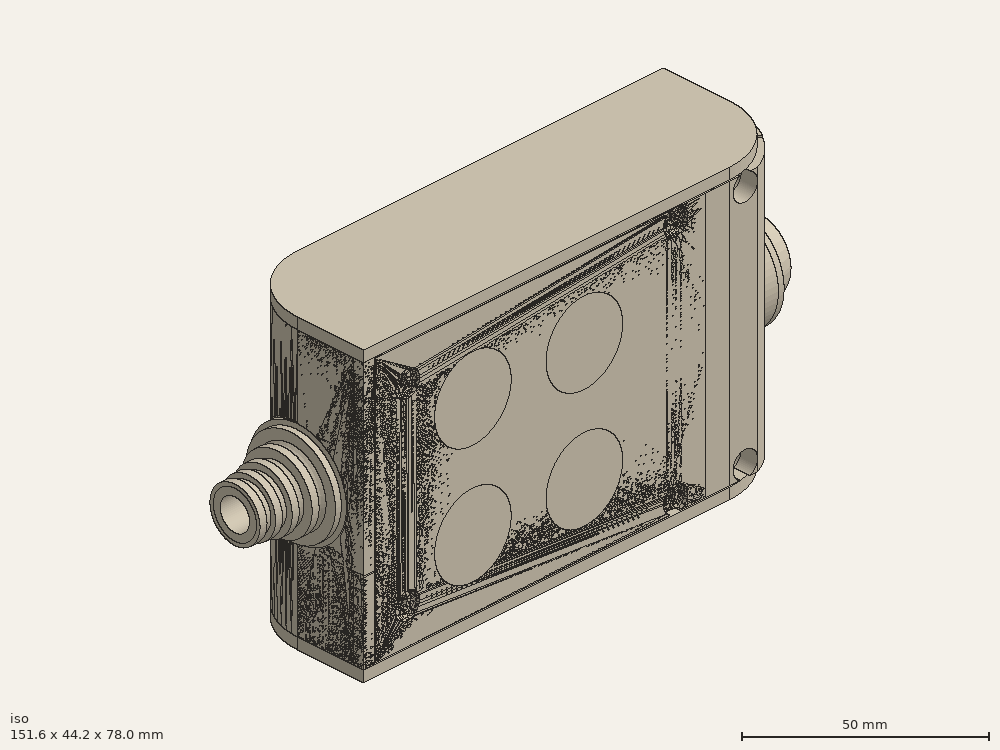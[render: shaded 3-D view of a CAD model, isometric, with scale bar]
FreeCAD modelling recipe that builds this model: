
FCSTD DOCUMENT  (FreeCAD 0.19R0.19.2)
Label: enclosure_159
License: All rights reserved
LicenseURL: http://en.wikipedia.org/wiki/All_rights_reserved
objects: Part::Feature×138, Part::Revolution×138, Part::MultiFuse×111, Sketcher::SketchObject×66, Part::Extrusion×51, Part::Cut×48, Part::Cylinder×44, Part::Fillet×43, Part::Box×28, App::MeasureDistance×4
note: 667 computed .brp shape members not serialized (recipe doc carries the construction recipe); baked Part::Feature solids carry a one-line shape summary decoded from their .brp

FEATURE [Sketcher::SketchObject] Sketch  label="topSketch"
  FullyConstrained = true
  sketch-geometry (20):
    g0: LineSegment StartX=5.21097e-06 StartY=3 StartZ=0 EndX=5.21097e-06 EndY=19 EndZ=0
    g1: ArcOfCircle CenterX=19 CenterY=19 CenterZ=0 NormalX=0 NormalY=0 NormalZ=1 AngleXU=0 Radius=19 StartAngle=1.5708 EndAngle=3.14159
    g2: ArcOfCircle CenterX=19 CenterY=19 CenterZ=0 NormalX=0 NormalY=0 NormalZ=1 AngleXU=0 Radius=16 StartAngle=1.5708 EndAngle=3.14159
    g3: LineSegment StartX=114 StartY=35 StartZ=0 EndX=19 EndY=35 EndZ=0
    g4: LineSegment StartX=5.21097e-06 StartY=3 StartZ=0 EndX=5.21097e-06 EndY=0 EndZ=0
    g5: LineSegment StartX=3 StartY=0 StartZ=0 EndX=5.21097e-06 EndY=0 EndZ=0
    g6: LineSegment StartX=3 StartY=19 StartZ=0 EndX=3 EndY=0 EndZ=0
    g7: LineSegment StartX=19 StartY=38 StartZ=0 EndX=124 EndY=38 EndZ=0
    g8: Circle CenterX=119 CenterY=35 CenterZ=0 NormalX=0 NormalY=0 NormalZ=1 AngleXU=0 Radius=1
    g9: Circle CenterX=121 CenterY=35 CenterZ=0 NormalX=0 NormalY=0 NormalZ=1 AngleXU=0 Radius=1
    g10: Circle CenterX=121 CenterY=33 CenterZ=0 NormalX=0 NormalY=0 NormalZ=1 AngleXU=0 Radius=1
    g11: BSplineCurve PolesCount=3 KnotsCount=2 Degree=2 IsPeriodic=0
    g12: GeomPoint X=119 Y=35 Z=0
    g13: GeomPoint X=121 Y=33 Z=0
    g14: LineSegment StartX=119 StartY=35 StartZ=0 EndX=114 EndY=35 EndZ=0
    g15: ArcOfCircle CenterX=105 CenterY=19 CenterZ=0 NormalX=0 NormalY=0 NormalZ=1 AngleXU=0 Radius=19 StartAngle=5.7297 EndAngle=6.28319
    g16: ArcOfCircle CenterX=105 CenterY=19 CenterZ=0 NormalX=0 NormalY=0 NormalZ=1 AngleXU=0 Radius=16 StartAngle=5.60905 EndAngle=6.28319
    g17: LineSegment StartX=121 StartY=33 StartZ=0 EndX=121 EndY=19 EndZ=0
    g18: LineSegment StartX=124 StartY=38 StartZ=0 EndX=124 EndY=19 EndZ=0
    g19: LineSegment StartX=117.5 StartY=9.01251 StartZ=0 EndX=121.163 EndY=9.0125 EndZ=0
  constraints (46):
    c: Vertical(g0)
    c: Block(g0)
    c: Coincident(g1,g0)
    c: Block(g1)
    c: Coincident(g2,g1)
    c: Block(g2)
    c: Coincident(g3,g2)
    c: Horizontal(g3)
    c: Tangent(g3,g2)
    c: Coincident(g4,g0)
    c: Distance(g4) = 3
    c: Vertical(g4)
    c: Coincident(g5,g4)
    c: Horizontal(g5)
    c: Coincident(g6,g2)
    c: Coincident(g6,g5)
    c: Vertical(g6)
    c: Horizontal(g7)
    c: Distance(g7) = 105
    c: Coincident(g7,g1)
    c: Block(g3)
    c: Weight(g8) = 1
    c: Equal(g8,g9)
    c: Equal(g8,g10)
    c: InternalAlignment(g8,g11)
    c: InternalAlignment(g9,g11)
    c: InternalAlignment(g10,g11)
    c: InternalAlignment(g12,g11)
    c: InternalAlignment(g13,g11)
    c: Block(g11)
    c: Coincident(g14,g11)
    c: Coincident(g14,g3)
    c: Horizontal(g14)
    c: Block(g15)
    c: Coincident(g16,g15)
    c: Block(g16)
    c: Coincident(g17,g11)
    c: Coincident(g17,g16)
    c: Vertical(g17)
    c: Distance(g17) = 14
    c: Coincident(g18,g7)
    c: Coincident(g18,g15)
    c: Vertical(g18)
    c: Distance(g18) = 19
    c: Coincident(g19,g16)
    c: Coincident(g19,g15)
FEATURE [Sketcher::SketchObject] Sketch001  label="bottomSketch"
  FullyConstrained = true
  sketch-geometry (32):
    g0: LineSegment StartX=3.3 StartY=-6.03275e-07 StartZ=0 EndX=98 EndY=-6.03275e-07 EndZ=0
    g1: ArcOfCircle CenterX=98 CenterY=19 CenterZ=0 NormalX=0 NormalY=0 NormalZ=1 AngleXU=0 Radius=19 StartAngle=4.71239 EndAngle=5.71103
    g2: LineSegment StartX=6.3 StartY=8 StartZ=0 EndX=3.3 EndY=8 EndZ=0
    g3: LineSegment StartX=3.3 StartY=8 StartZ=0 EndX=3.3 EndY=-6.03275e-07 EndZ=0
    g4: ArcOfCircle CenterX=8.3 CenterY=5 CenterZ=0 NormalX=0 NormalY=0 NormalZ=1 AngleXU=0 Radius=2 StartAngle=3.14159 EndAngle=4.71239
    g5: LineSegment StartX=6.3 StartY=8 StartZ=0 EndX=6.3 EndY=5 EndZ=0
    g6: ArcOfCircle CenterX=98 CenterY=19 CenterZ=0 NormalX=0 NormalY=0 NormalZ=1 AngleXU=0 Radius=12.7 StartAngle=4.71239 EndAngle=6.28319
    g7: LineSegment StartX=94.7 StartY=3 StartZ=0 EndX=8.3 EndY=3 EndZ=0
    g8-g12: Circle x5 (B-spline internal-alignment scaffolding for g13; pole/knot coordinates omitted)
    g13: BSplineCurve PolesCount=5 KnotsCount=3 Degree=3 IsPeriodic=0
    g14: GeomPoint X=98 Y=6.3 Z=0
    g15: GeomPoint X=96.3938 Y=4.71946 Z=0
    g16: GeomPoint X=94.7 Y=3 Z=0
    g17-g23: Circle x7 (B-spline internal-alignment scaffolding for g24; pole/knot coordinates omitted)
    g24: BSplineCurve PolesCount=7 KnotsCount=5 Degree=3 IsPeriodic=0
    g25-g29: GeomPoint x5 (B-spline internal-alignment scaffolding for g24; pole/knot coordinates omitted)
    g30: ArcOfCircle CenterX=98 CenterY=19 CenterZ=0 NormalX=0 NormalY=0 NormalZ=1 AngleXU=0 Radius=15.7 StartAngle=5.81226 EndAngle=6.28319
    g31: LineSegment StartX=110.7 StartY=19 StartZ=0 EndX=113.7 EndY=19 EndZ=0
  constraints (41):
    c: Horizontal(g0)
    c: Coincident(g1,g0)
    c: Block(g1)
    c: Horizontal(g2)
    c: Distance(g2) = 3
    c: Coincident(g3,g2)
    c: Vertical(g3)
    c: Coincident(g3,g0)
    c: Block(g4)
    c: Block(g2)
    c: Coincident(g5,g2)
    c: Coincident(g5,g4)
    c: Vertical(g5)
    c: Coincident(g6,g1)
    c: Block(g6)
    c: Coincident(g7,g4)
    c: Horizontal(g7)
    c: Block(g0)
    c: Block(g7)
    c: Block(g3)
    c: Coincident(g13,g6)
    c: Weight(g8) = 1
    c: Equal(g8, g9-g12) x4
    c: Coincident(g13,g7)
    c: InternalAlignment(g8-g12 -> g13) x5
    c: InternalAlignment(g14,g13)
    c: InternalAlignment(g15,g13)
    c: InternalAlignment(g16,g13)
    c: Block(g13)
    c: Weight(g17) = 1
    c: Equal(g17, g18-g23) x6
    c: Coincident(g24,g1)
    c: InternalAlignment(g17-g23 -> g24) x7
    c: InternalAlignment(g25-g29 -> g24) x5
    c: Block(g24)
    c: Coincident(g30,g24)
    c: Coincident(g31,g6)
    c: Coincident(g31,g30)
    c: Horizontal(g31)
    c: Block(g31)
    c: Block(g30)
FEATURE [Part::Extrusion] Extrude  label="top"
  Base = -> Sketch
  Dir = (0,0,1)
  DirMode = 2
  FaceMakerClass = Part::FaceMakerBullseye
  LengthFwd = 72
  LengthRev = 0
  Solid = true
  Symmetric = false
FEATURE [Part::Extrusion] Extrude001  label="bottom"
  Base = -> Sketch001
  Dir = (0,0,1)
  DirMode = 2
  FaceMakerClass = Part::FaceMakerBullseye
  LengthFwd = 71.4
  LengthRev = 0
  Placement = pos=(0,0,0.3) rot=(0,0,1;0rad)
  Solid = true
  Symmetric = false
FEATURE [Sketcher::SketchObject] Sketch002  label="topSketch001"
  FullyConstrained = true
  sketch-geometry (6):
    g0: ArcOfCircle CenterX=19 CenterY=19 CenterZ=0 NormalX=0 NormalY=0 NormalZ=1 AngleXU=0 Radius=19 StartAngle=1.5708 EndAngle=3.14159
    g1: LineSegment StartX=5.22862e-06 StartY=19 StartZ=0 EndX=5.22862e-06 EndY=1.19904e-11 EndZ=0
    g2: LineSegment StartX=19 StartY=38 StartZ=0 EndX=124 EndY=38 EndZ=0
    g3: LineSegment StartX=5.22862e-06 StartY=1.19904e-11 StartZ=0 EndX=105 EndY=1.19904e-11 EndZ=0
    g4: ArcOfCircle CenterX=105 CenterY=19 CenterZ=0 NormalX=0 NormalY=0 NormalZ=1 AngleXU=0 Radius=19 StartAngle=4.71239 EndAngle=6.28319
    g5: LineSegment StartX=124 StartY=38 StartZ=0 EndX=124 EndY=19 EndZ=0
  constraints (16):
    c: Block(g0)
    c: Coincident(g1,g0)
    c: Vertical(g1)
    c: Horizontal(g2)
    c: Distance(g2) = 105
    c: Coincident(g2,g0)
    c: Distance(g1) = 19
    c: Coincident(g3,g1)
    c: Horizontal(g3)
    c: Distance(g3) = 105
    c: Block(g4)
    c: Coincident(g4,g3)
    c: Coincident(g5,g2)
    c: Coincident(g5,g4)
    c: Vertical(g5)
    c: Distance(g5) = 19
FEATURE [Part::Extrusion] Extrude002  label="sideA"
  Base = -> Sketch002
  Dir = (0,0,1)
  DirMode = 2
  FaceMakerClass = Part::FaceMakerBullseye
  LengthFwd = 3
  LengthRev = 0
  Placement = pos=(0,0,-3) rot=(0,0,1;0rad)
  Solid = true
  Symmetric = false
FEATURE [Sketcher::SketchObject] Sketch003  label="topSketch002"
  FullyConstrained = true
  sketch-geometry (6):
    g0: LineSegment StartX=19 StartY=38 StartZ=0 EndX=117 EndY=38 EndZ=0
    g1: ArcOfCircle CenterX=19 CenterY=19 CenterZ=0 NormalX=0 NormalY=0 NormalZ=1 AngleXU=0 Radius=19 StartAngle=1.5708 EndAngle=3.14159
    g2: LineSegment StartX=117 StartY=38 StartZ=0 EndX=117 EndY=19 EndZ=0
    g3: LineSegment StartX=98 StartY=1.0161e-12 StartZ=0 EndX=5.22862e-06 EndY=1.0161e-12 EndZ=0
    g4: LineSegment StartX=5.22862e-06 StartY=19 StartZ=0 EndX=5.22862e-06 EndY=1.0161e-12 EndZ=0
    g5: ArcOfCircle CenterX=98 CenterY=19 CenterZ=0 NormalX=0 NormalY=0 NormalZ=1 AngleXU=0 Radius=19 StartAngle=4.71239 EndAngle=6.28319
  constraints (16):
    c: Horizontal(g0)
    c: Distance(g0) = 98
    c: Coincident(g1,g0)
    c: Block(g1)
    c: Coincident(g2,g0)
    c: Vertical(g2)
    c: Distance(g2) = 19
    c: Horizontal(g3)
    c: Coincident(g4,g1)
    c: Vertical(g4)
    c: Coincident(g3,g4)
    c: Block(g3)
    c: Coincident(g5,g2)
    c: Coincident(g5,g3)
    c: Block(g0)
    c: Block(g5)
FEATURE [Sketcher::SketchObject] Sketch004
  FullyConstrained = true
  MapMode = 3
  Placement = pos=(0,0,0) rot=(1,0,0;1.5708rad)
  Support = -> [Extrude]
  sketch-geometry (8):
    g0: Circle CenterX=80.351 CenterY=-67.6202 CenterZ=0 NormalX=0 NormalY=0 NormalZ=1 AngleXU=0 Radius=2
    g1: Circle CenterX=80.351 CenterY=-67.6202 CenterZ=0 NormalX=0 NormalY=0 NormalZ=1 AngleXU=0 Radius=3
    g2: Circle CenterX=80.351 CenterY=-4.92017 CenterZ=0 NormalX=0 NormalY=0 NormalZ=1 AngleXU=0 Radius=2
    g3: Circle CenterX=80.351 CenterY=-4.92017 CenterZ=0 NormalX=0 NormalY=0 NormalZ=1 AngleXU=0 Radius=3
    g4: Circle CenterX=23.851 CenterY=-4.92017 CenterZ=0 NormalX=0 NormalY=0 NormalZ=1 AngleXU=0 Radius=2
    g5: Circle CenterX=23.851 CenterY=-4.92017 CenterZ=0 NormalX=0 NormalY=0 NormalZ=1 AngleXU=0 Radius=3
    g6: Circle CenterX=23.851 CenterY=-67.6202 CenterZ=0 NormalX=0 NormalY=0 NormalZ=1 AngleXU=0 Radius=2
    g7: Circle CenterX=23.851 CenterY=-67.6202 CenterZ=0 NormalX=0 NormalY=0 NormalZ=1 AngleXU=0 Radius=3
  constraints (8):
    c: Block(g3)
    c: Block(g2)
    c: Block(g1)
    c: Block(g0)
    c: Block(g6)
    c: Block(g7)
    c: Block(g4)
    c: Block(g5)
FEATURE [Part::Extrusion] Extrude004
  Base = -> Sketch004
  Dir = (0,-1,2e-16)
  DirMode = 2
  FaceMakerClass = Part::FaceMakerBullseye
  LengthFwd = 6
  LengthRev = 0
  Placement = pos=(0,9,0) rot=(0,0,1;0rad)
  Solid = true
  Symmetric = false
FEATURE [Sketcher::SketchObject] Sketch005
  FullyConstrained = true
  MapMode = 3
  Placement = pos=(0,0,0) rot=(1,0,0;1.5708rad)
  Support = -> [Extrude]
  sketch-geometry (8):
    g0: Circle CenterX=80.351 CenterY=-67.6202 CenterZ=0 NormalX=0 NormalY=0 NormalZ=1 AngleXU=0 Radius=3
    g1: Circle CenterX=80.351 CenterY=-4.92017 CenterZ=0 NormalX=0 NormalY=0 NormalZ=1 AngleXU=0 Radius=3
    g2: Circle CenterX=23.851 CenterY=-4.92017 CenterZ=0 NormalX=0 NormalY=0 NormalZ=1 AngleXU=0 Radius=3
    g3: Circle CenterX=23.851 CenterY=-67.6202 CenterZ=0 NormalX=0 NormalY=0 NormalZ=1 AngleXU=0 Radius=3
    g4: Circle CenterX=23.851 CenterY=-67.6202 CenterZ=0 NormalX=0 NormalY=0 NormalZ=1 AngleXU=0 Radius=5
    g5: Circle CenterX=80.351 CenterY=-67.6202 CenterZ=0 NormalX=0 NormalY=0 NormalZ=1 AngleXU=0 Radius=5
    g6: Circle CenterX=23.851 CenterY=-4.92017 CenterZ=0 NormalX=0 NormalY=0 NormalZ=1 AngleXU=0 Radius=5
    g7: Circle CenterX=80.351 CenterY=-4.92017 CenterZ=0 NormalX=0 NormalY=0 NormalZ=1 AngleXU=0 Radius=5
  constraints (8):
    c: Block(g1)
    c: Block(g0)
    c: Block(g3)
    c: Block(g2)
    c: Block(g5)
    c: Block(g4)
    c: Block(g6)
    c: Block(g7)
FEATURE [Part::Extrusion] Extrude005
  Base = -> Sketch005
  Dir = (0,-1,2e-16)
  DirMode = 2
  FaceMakerClass = Part::FaceMakerBullseye
  LengthFwd = 2
  LengthRev = 0
  Solid = true
  Symmetric = false
FEATURE [Sketcher::SketchObject] Sketch006
  FullyConstrained = true
  MapMode = 3
  Placement = pos=(0,0,0) rot=(1,0,0;1.5708rad)
  sketch-geometry (8):
    g0: Circle CenterX=80.351 CenterY=-67.6202 CenterZ=0 NormalX=0 NormalY=0 NormalZ=1 AngleXU=0 Radius=3
    g1: Circle CenterX=80.351 CenterY=-4.92017 CenterZ=0 NormalX=0 NormalY=0 NormalZ=1 AngleXU=0 Radius=3
    g2: Circle CenterX=23.851 CenterY=-4.92017 CenterZ=0 NormalX=0 NormalY=0 NormalZ=1 AngleXU=0 Radius=3
    g3: Circle CenterX=23.851 CenterY=-67.6202 CenterZ=0 NormalX=0 NormalY=0 NormalZ=1 AngleXU=0 Radius=3
    g4: Circle CenterX=23.851 CenterY=-67.6202 CenterZ=0 NormalX=0 NormalY=0 NormalZ=1 AngleXU=0 Radius=5
    g5: Circle CenterX=80.351 CenterY=-67.6202 CenterZ=0 NormalX=0 NormalY=0 NormalZ=1 AngleXU=0 Radius=5
    g6: Circle CenterX=23.851 CenterY=-4.92017 CenterZ=0 NormalX=0 NormalY=0 NormalZ=1 AngleXU=0 Radius=5
    g7: Circle CenterX=80.351 CenterY=-4.92017 CenterZ=0 NormalX=0 NormalY=0 NormalZ=1 AngleXU=0 Radius=5
  constraints (8):
    c: Block(g1)
    c: Block(g0)
    c: Block(g3)
    c: Block(g2)
    c: Block(g5)
    c: Block(g4)
    c: Block(g6)
    c: Block(g7)
FEATURE [Part::Extrusion] Extrude007
  Base = -> Sketch006
  Dir = (0,-1,2e-16)
  DirMode = 2
  FaceMakerClass = Part::FaceMakerBullseye
  LengthFwd = 2
  LengthRev = 0
  Solid = true
  Symmetric = false
FEATURE [Part::Fillet] Fillet
  Base = -> Extrude007
  Edges = 4 edges r=1.99: [Edge6,Edge12,Edge18,Edge24]
FEATURE [Part::Cut] Cut
  Base = -> Extrude005
  Placement = pos=(0,5,0) rot=(0,0,1;0rad)
  Tool = -> Fillet
FEATURE [Part::MultiFuse] Fusion  label="pCBScrews"
  Placement = pos=(-2.5,0,72.3) rot=(0,0,1;0rad)
  Shapes = -> [Extrude004,Cut]
FEATURE [App::MeasureDistance] Distance  label="Distance: 0.69 mm"
  Distance = 0.685967
  P1 = (24.0138,2.9647,0.3)
  P2 = (23.8901,3,-0.373787)
FEATURE [App::MeasureDistance] Distance001  label="Distance: 0.53 mm"
  Distance = 0.533607
  P1 = (80.2939,3,72.2334)
  P2 = (80.281,2.99661,71.7)
FEATURE [Part::Fillet] Fillet001
  Base = -> Extrude001
  Edges = 1 edges r=2.4: [Edge17]
FEATURE [Part::Fillet] Fillet002  label="bottom001"
  Base = -> Fillet001
  Edges = 1 edges r=2.4: [Edge36]
FEATURE [Part::Fillet] Fillet003  label="top001"
  Base = -> Extrude
  Edges = 1 edges r=2: [Edge1]
FEATURE [Sketcher::SketchObject] Sketch007
  FullyConstrained = true
  sketch-geometry (16):
    g0: LineSegment StartX=4 StartY=0 StartZ=0 EndX=4 EndY=2.4 EndZ=0
    g1: LineSegment StartX=4 StartY=2.4 StartZ=0 EndX=7 EndY=2.4 EndZ=0
    g2: LineSegment StartX=4 StartY=0 StartZ=0 EndX=5.7 EndY=0 EndZ=0
    g3: LineSegment StartX=5.7 StartY=0 StartZ=0 EndX=5.7 EndY=-5.6 EndZ=0
    g4-g8: Circle x5 (B-spline internal-alignment scaffolding for g9; pole/knot coordinates omitted)
    g9: BSplineCurve PolesCount=5 KnotsCount=3 Degree=3 IsPeriodic=0
    g10: GeomPoint X=7 Y=2.4 Z=0
    g11: GeomPoint X=10.4582 Y=-1.55472 Z=0
    g12: GeomPoint X=14 Y=-5.6 Z=0
    g13: LineSegment StartX=14 StartY=-5.6 StartZ=0 EndX=14 EndY=-14.1 EndZ=0
    g14: LineSegment StartX=14 StartY=-14.1 StartZ=0 EndX=6.5 EndY=-14.1 EndZ=0
    g15: LineSegment StartX=5.7 StartY=-5.6 StartZ=0 EndX=6.5 EndY=-14.1 EndZ=0
  constraints (28):
    c: Distance(g0) = 2.4
    c: Vertical(g0)
    c: Block(g0)
    c: Coincident(g1,g0)
    c: Horizontal(g1)
    c: Distance(g1) = 3
    c: Coincident(g2,g0)
    c: Horizontal(g2)
    c: Distance(g2) = 1.7
    c: Coincident(g3,g2)
    c: Vertical(g3)
    c: Distance(g3) = 5.6
    c: Coincident(g9,g1)
    c: Weight(g4) = 1
    c: Equal(g4, g5-g8) x4
    c: InternalAlignment(g4-g8 -> g9) x5
    c: InternalAlignment(g10,g9)
    c: InternalAlignment(g11,g9)
    c: InternalAlignment(g12,g9)
    c: Block(g9)
    c: Coincident(g13,g9)
    c: Vertical(g13)
    c: Distance(g13) = 8.5
    c: Coincident(g14,g13)
    c: Horizontal(g14)
    c: Distance(g14) = 7.5
    c: Coincident(g15,g3)
    c: Coincident(g15,g14)
FEATURE [Part::Feature] Face
  shape: bbox 10 x 16.5 x 2e-07 mm, 1 faces, 0 solids (baked)
FEATURE [Part::Revolution] Revolve  label="plugHousing"
  Angle = 360
  Axis = (0,1,0)
  Base = (0,0,0)
  FaceMakerClass = Part::FaceMakerBullseye
  Placement = pos=(0,0,36.15) rot=(0,0,1;0rad)
  Solid = false
  Source = -> Face
  Symmetric = false
FEATURE [Part::Feature] Face001
  shape: bbox 10 x 16.5 x 2e-07 mm, 1 faces, 0 solids (baked)
FEATURE [Part::Revolution] Revolve001  label="plugHousing001"
  Angle = 360
  Axis = (0,1,0)
  Base = (0,0,0)
  FaceMakerClass = Part::FaceMakerBullseye
  Placement = pos=(0,0,36.15) rot=(0,0,1;0rad)
  Solid = false
  Source = -> Face001
  Symmetric = false
FEATURE [Part::MultiFuse] Fusion001  label="plugHousing002"
  Placement = pos=(0,0,0) rot=(0,0,1;1.5708rad)
  Shapes = -> [Revolve001,Revolve]
FEATURE [Part::Feature] Face002
  shape: bbox 10 x 16.5 x 2e-07 mm, 1 faces, 0 solids (baked)
FEATURE [Part::Revolution] Revolve003  label="plugHousing005"
  Angle = 360
  Axis = (0,1,0)
  Base = (0,0,0)
  FaceMakerClass = Part::FaceMakerBullseye
  Placement = pos=(0,0,36.15) rot=(0,0,1;0rad)
  Solid = false
  Source = -> Face002
  Symmetric = false
FEATURE [Part::Feature] Face003
  shape: bbox 10 x 16.5 x 2e-07 mm, 1 faces, 0 solids (baked)
FEATURE [Part::Revolution] Revolve002  label="plugHousing003"
  Angle = 360
  Axis = (0,1,0)
  Base = (0,0,0)
  FaceMakerClass = Part::FaceMakerBullseye
  Placement = pos=(0,0,36.15) rot=(0,0,1;0rad)
  Solid = false
  Source = -> Face003
  Symmetric = false
FEATURE [Part::MultiFuse] Fusion002  label="plugHousing004"
  Placement = pos=(0,0,0) rot=(0,0,1;1.5708rad)
  Shapes = -> [Revolve002,Revolve003]
FEATURE [Part::MultiFuse] Fusion003  label="plugHousing006"
  Placement = pos=(0,19,0) rot=(0,0,1;3.14159rad)
  Shapes = -> [Fusion002,Fusion001]
FEATURE [Part::Feature] Face004
  shape: bbox 10 x 16.5 x 2e-07 mm, 1 faces, 0 solids (baked)
FEATURE [Part::Revolution] Revolve006  label="plugHousing010"
  Angle = 360
  Axis = (0,1,0)
  Base = (0,0,0)
  FaceMakerClass = Part::FaceMakerBullseye
  Placement = pos=(0,0,36.15) rot=(0,0,1;0rad)
  Solid = false
  Source = -> Face004
  Symmetric = false
FEATURE [Part::Feature] Face005
  shape: bbox 10 x 16.5 x 2e-07 mm, 1 faces, 0 solids (baked)
FEATURE [Part::Revolution] Revolve007  label="plugHousing011"
  Angle = 360
  Axis = (0,1,0)
  Base = (0,0,0)
  FaceMakerClass = Part::FaceMakerBullseye
  Placement = pos=(0,0,36.15) rot=(0,0,1;0rad)
  Solid = false
  Source = -> Face005
  Symmetric = false
FEATURE [Part::Feature] Face006
  shape: bbox 10 x 16.5 x 2e-07 mm, 1 faces, 0 solids (baked)
FEATURE [Part::Revolution] Revolve004  label="plugHousing007"
  Angle = 360
  Axis = (0,1,0)
  Base = (0,0,0)
  FaceMakerClass = Part::FaceMakerBullseye
  Placement = pos=(0,0,36.15) rot=(0,0,1;0rad)
  Solid = false
  Source = -> Face006
  Symmetric = false
FEATURE [Part::MultiFuse] Fusion004  label="plugHousing009"
  Placement = pos=(0,0,0) rot=(0,0,1;1.5708rad)
  Shapes = -> [Revolve004,Revolve007]
FEATURE [Part::Feature] Face007
  shape: bbox 10 x 16.5 x 2e-07 mm, 1 faces, 0 solids (baked)
FEATURE [Part::Revolution] Revolve005  label="plugHousing008"
  Angle = 360
  Axis = (0,1,0)
  Base = (0,0,0)
  FaceMakerClass = Part::FaceMakerBullseye
  Placement = pos=(0,0,36.15) rot=(0,0,1;0rad)
  Solid = false
  Source = -> Face007
  Symmetric = false
FEATURE [Part::MultiFuse] Fusion005  label="plugHousing012"
  Placement = pos=(0,0,0) rot=(0,0,1;1.5708rad)
  Shapes = -> [Revolve006,Revolve005]
FEATURE [Part::MultiFuse] Fusion006  label="plugHousing013"
  Placement = pos=(0,19,0) rot=(0,0,1;3.14159rad)
  Shapes = -> [Fusion005,Fusion004]
FEATURE [Part::MultiFuse] Fusion007  label="plugHousing014"
  Placement = pos=(122.621,0,-0.15) rot=(0,0,1;0rad)
  Shapes = -> [Fusion003,Fusion006]
FEATURE [Part::Cylinder] Cylinder002
  Angle = 360
  AttacherType = Attacher::AttachEngine3D
  Height = 20
  Placement = pos=(0,0,36.15) rot=(0,0,1;0rad)
  Radius = 4
FEATURE [Part::Cylinder] Cylinder003
  Angle = 360
  AttacherType = Attacher::AttachEngine3D
  Height = 10
  Placement = pos=(0,0,36.15) rot=(0,0,1;0rad)
  Radius = 4
FEATURE [Part::MultiFuse] Fusion009  label="removeToCreateHoleForPlugHousing"
  Placement = pos=(70,19,36.15) rot=(0,1,0;1.5708rad)
  Shapes = -> [Cylinder002,Cylinder003]
FEATURE [Part::Cylinder] Cylinder004
  Angle = 360
  AttacherType = Attacher::AttachEngine3D
  Height = 20
  Placement = pos=(0,0,36.15) rot=(0,0,1;0rad)
  Radius = 4
FEATURE [Part::Cylinder] Cylinder005
  Angle = 360
  AttacherType = Attacher::AttachEngine3D
  Height = 10
  Placement = pos=(0,0,36.15) rot=(0,0,1;0rad)
  Radius = 4
FEATURE [Part::MultiFuse] Fusion010  label="removeToCreateHoleForPlugHousing001"
  Placement = pos=(70,19,36.15) rot=(0,1,0;1.5708rad)
  Shapes = -> [Cylinder004,Cylinder005]
FEATURE [Part::Cut] Cut001
  Base = -> Fillet003
  Tool = -> Fusion010
FEATURE [Part::Cut] Cut002  label="Bottom"
  Base = -> Fillet002
  Tool = -> Fusion009
FEATURE [Part::Feature] Face008
  shape: bbox 10 x 16.5 x 2e-07 mm, 1 faces, 0 solids (baked)
FEATURE [Part::Revolution] Revolve011  label="plugHousing021"
  Angle = 360
  Axis = (0,1,0)
  Base = (0,0,0)
  FaceMakerClass = Part::FaceMakerBullseye
  Placement = pos=(0,0,36.15) rot=(0,0,1;0rad)
  Solid = false
  Source = -> Face008
  Symmetric = false
FEATURE [Part::Feature] Face009
  shape: bbox 10 x 16.5 x 2e-07 mm, 1 faces, 0 solids (baked)
FEATURE [Part::Revolution] Revolve012  label="plugHousing022"
  Angle = 360
  Axis = (0,1,0)
  Base = (0,0,0)
  FaceMakerClass = Part::FaceMakerBullseye
  Placement = pos=(0,0,36.15) rot=(0,0,1;0rad)
  Solid = false
  Source = -> Face009
  Symmetric = false
FEATURE [Part::Feature] Face010 .. Face013  x4 (patterned run collapsed; names and placements below)
  shape: bbox 10 x 16.5 x 2e-07 mm, 1 faces, 0 solids (baked)
FEATURE [Part::Revolution] Revolve015  label="plugHousing027"
  Angle = 360
  Axis = (0,1,0)
  Base = (0,0,0)
  FaceMakerClass = Part::FaceMakerBullseye
  Placement = pos=(0,0,36.15) rot=(0,0,1;0rad)
  Solid = false
  Source = -> Face013
  Symmetric = false
FEATURE [Part::Feature] Face014
  shape: bbox 10 x 16.5 x 2e-07 mm, 1 faces, 0 solids (baked)
FEATURE [Part::Feature] Face015
  shape: bbox 10 x 16.5 x 2e-07 mm, 1 faces, 0 solids (baked)
FEATURE [Part::Feature] Face016
  shape: bbox 10 x 16.5 x 2e-07 mm, 1 faces, 0 solids (baked)
FEATURE [Part::Revolution] Revolve019  label="plugHousing033"
  Angle = 360
  Axis = (0,1,0)
  Base = (0,0,0)
  FaceMakerClass = Part::FaceMakerBullseye
  Placement = pos=(0,0,36.15) rot=(0,0,1;0rad)
  Solid = false
  Source = -> Face016
  Symmetric = false
FEATURE [Part::Feature] Face017
  shape: bbox 10 x 16.5 x 2e-07 mm, 1 faces, 0 solids (baked)
FEATURE [Part::Revolution] Revolve020  label="plugHousing034"
  Angle = 360
  Axis = (0,1,0)
  Base = (0,0,0)
  FaceMakerClass = Part::FaceMakerBullseye
  Placement = pos=(0,0,36.15) rot=(0,0,1;0rad)
  Solid = false
  Source = -> Face017
  Symmetric = false
FEATURE [Part::Feature] Face018
  shape: bbox 10 x 16.5 x 2e-07 mm, 1 faces, 0 solids (baked)
FEATURE [Part::Revolution] Revolve016  label="plugHousing030"
  Angle = 360
  Axis = (0,1,0)
  Base = (0,0,0)
  FaceMakerClass = Part::FaceMakerBullseye
  Placement = pos=(0,0,36.15) rot=(0,0,1;0rad)
  Solid = false
  Source = -> Face018
  Symmetric = false
FEATURE [Part::MultiFuse] Fusion020  label="plugHousing038"
  Placement = pos=(0,0,0) rot=(0,0,1;1.5708rad)
  Shapes = -> [Revolve016,Revolve020]
FEATURE [Part::Feature] Face019
  shape: bbox 10 x 16.5 x 2e-07 mm, 1 faces, 0 solids (baked)
FEATURE [Part::Feature] Face020
  shape: bbox 10 x 16.5 x 2e-07 mm, 1 faces, 0 solids (baked)
FEATURE [Part::Revolution] Revolve017  label="plugHousing031"
  Angle = 360
  Axis = (0,1,0)
  Base = (0,0,0)
  FaceMakerClass = Part::FaceMakerBullseye
  Placement = pos=(0,0,36.15) rot=(0,0,1;0rad)
  Solid = false
  Source = -> Face020
  Symmetric = false
FEATURE [Part::MultiFuse] Fusion021  label="plugHousing039"
  Placement = pos=(0,0,0) rot=(0,0,1;1.5708rad)
  Shapes = -> [Revolve019,Revolve017]
FEATURE [Part::MultiFuse] Fusion023  label="plugHousing041"
  Placement = pos=(0,19,0) rot=(0,0,1;3.14159rad)
  Shapes = -> [Fusion021,Fusion020]
FEATURE [Part::Revolution] Revolve022  label="plugHousing043"
  Angle = 360
  Axis = (0,1,0)
  Base = (0,0,0)
  FaceMakerClass = Part::FaceMakerBullseye
  Placement = pos=(0,0,36.15) rot=(0,0,1;0rad)
  Solid = false
  Source = -> Face019
  Symmetric = false
FEATURE [Part::Feature] Face021
  shape: bbox 10 x 16.5 x 2e-07 mm, 1 faces, 0 solids (baked)
FEATURE [Part::Revolution] Revolve023  label="plugHousing044"
  Angle = 360
  Axis = (0,1,0)
  Base = (0,0,0)
  FaceMakerClass = Part::FaceMakerBullseye
  Placement = pos=(0,0,36.15) rot=(0,0,1;0rad)
  Solid = false
  Source = -> Face021
  Symmetric = false
FEATURE [Part::Feature] Face022
  shape: bbox 10 x 16.5 x 2e-07 mm, 1 faces, 0 solids (baked)
FEATURE [Part::Revolution] Revolve018  label="plugHousing032"
  Angle = 360
  Axis = (0,1,0)
  Base = (0,0,0)
  FaceMakerClass = Part::FaceMakerBullseye
  Placement = pos=(0,0,36.15) rot=(0,0,1;0rad)
  Solid = false
  Source = -> Face022
  Symmetric = false
FEATURE [Part::MultiFuse] Fusion022  label="plugHousing040"
  Placement = pos=(0,0,0) rot=(0,0,1;1.5708rad)
  Shapes = -> [Revolve018,Revolve023]
FEATURE [Part::Feature] Face023
  shape: bbox 10 x 16.5 x 2e-07 mm, 1 faces, 0 solids (baked)
FEATURE [Part::Revolution] Revolve021  label="plugHousing035"
  Angle = 360
  Axis = (0,1,0)
  Base = (0,0,0)
  FaceMakerClass = Part::FaceMakerBullseye
  Placement = pos=(0,0,36.15) rot=(0,0,1;0rad)
  Solid = false
  Source = -> Face023
  Symmetric = false
FEATURE [Part::MultiFuse] Fusion018  label="plugHousing036"
  Placement = pos=(0,0,0) rot=(0,0,1;1.5708rad)
  Shapes = -> [Revolve022,Revolve021]
FEATURE [Part::MultiFuse] Fusion019  label="plugHousing037"
  Placement = pos=(0,19,0) rot=(0,0,1;3.14159rad)
  Shapes = -> [Fusion018,Fusion022]
FEATURE [Part::MultiFuse] Fusion024  label="plugHousing042"
  Placement = pos=(122.621,0,-0.15) rot=(0,0,1;0rad)
  Shapes = -> [Fusion023,Fusion019]
FEATURE [Part::Cylinder] Cylinder006
  Angle = 360
  AttacherType = Attacher::AttachEngine3D
  Height = 20
  Placement = pos=(0,0,36.15) rot=(0,0,1;0rad)
  Radius = 14.3
FEATURE [Part::Cylinder] Cylinder007
  Angle = 360
  AttacherType = Attacher::AttachEngine3D
  Height = 10
  Placement = pos=(0,0,36.15) rot=(0,0,1;0rad)
  Radius = 4
FEATURE [Part::MultiFuse] Fusion026  label="removeToCreteHoleForPlugHousing"
  Placement = pos=(70,19,36) rot=(0,1,0;1.5708rad)
  Shapes = -> [Cylinder006,Cylinder007]
FEATURE [Part::Box] Box001  label="Cube001"
  AttacherType = Attacher::AttachEngine3D
  Height = 28
  Length = 3
  Placement = pos=(110.7,19,22) rot=(0,0,1;0rad)
  Width = 15.7
FEATURE [Part::Cut] Cut003  label="top002"
  Base = -> Cut001
  Tool = -> Fusion007
FEATURE [Part::Revolution] Revolve008  label="plugHousing015"
  Angle = 360
  Axis = (0,1,0)
  Base = (0,0,0)
  FaceMakerClass = Part::FaceMakerBullseye
  Placement = pos=(0,0,36.15) rot=(0,0,1;0rad)
  Solid = false
  Source = -> Face010
  Symmetric = false
FEATURE [Part::MultiFuse] Fusion013  label="plugHousing020"
  Placement = pos=(0,0,0) rot=(0,0,1;1.5708rad)
  Shapes = -> [Revolve008,Revolve012]
FEATURE [Part::Cut] Cut004  label="top003"
  Base = -> Cut003
  Placement = pos=(1,0,0) rot=(0,0,1;0rad)
  Tool = -> Fusion026
FEATURE [Part::Cylinder] Cylinder008
  Angle = 360
  AttacherType = Attacher::AttachEngine3D
  Height = 20
  Placement = pos=(0,0,36.15) rot=(0,0,1;0rad)
  Radius = 10.3
FEATURE [Part::Cylinder] Cylinder009
  Angle = 360
  AttacherType = Attacher::AttachEngine3D
  Height = 10
  Placement = pos=(0,0,36.15) rot=(0,0,1;0rad)
  Radius = 4
FEATURE [Part::MultiFuse] Fusion027  label="removeToCreteHoleForPlugHousing001"
  Placement = pos=(70,19,36) rot=(0,1,0;1.5708rad)
  Shapes = -> [Cylinder008,Cylinder009]
FEATURE [Part::Cut] Cut005  label="plugHousingTab"
  Base = -> Box001
  Tool = -> Fusion027
FEATURE [Part::MultiFuse] Fusion028  label="plugHousing045"
  Shapes = -> [Fusion024,Cut005]
FEATURE [Part::Box] Box002  label="Cube002"
  AttacherType = Attacher::AttachEngine3D
  Height = 28.8
  Length = 3
  Placement = pos=(107.3,28,21.6) rot=(0,0,1;0rad)
  Width = 7
FEATURE [Part::Box] Box003  label="Cube003"
  AttacherType = Attacher::AttachEngine3D
  Height = 3
  Length = 6.4
  Placement = pos=(107.3,28,18.6) rot=(0,0,1;0rad)
  Width = 7
FEATURE [Part::Box] Box004  label="Cube004"
  AttacherType = Attacher::AttachEngine3D
  Height = 3
  Length = 6.4
  Placement = pos=(107.3,28,50.4) rot=(0,0,1;0rad)
  Width = 7
FEATURE [Part::MultiFuse] Fusion029  label="plugHousingBracketHolder"
  Shapes = -> [Box004,Box002,Box003]
FEATURE [Part::Cylinder] Cylinder010
  Angle = 360
  AttacherType = Attacher::AttachEngine3D
  Height = 20
  Placement = pos=(0,0,36.15) rot=(0,0,1;0rad)
  Radius = 14.3
FEATURE [Part::Cylinder] Cylinder011
  Angle = 360
  AttacherType = Attacher::AttachEngine3D
  Height = 10
  Placement = pos=(0,0,36.15) rot=(0,0,1;0rad)
  Radius = 4
FEATURE [Part::MultiFuse] Fusion030  label="removeToCreteHoleForPlugHousing002"
  Placement = pos=(70,19,36) rot=(0,1,0;1.5708rad)
  Shapes = -> [Cylinder010,Cylinder011]
FEATURE [Part::Cut] Cut006  label="plugHousingBracketHolder001"
  Base = -> Fusion029
  Tool = -> Fusion030
FEATURE [Part::Cylinder] Cylinder012
  Angle = 360
  AttacherType = Attacher::AttachEngine3D
  Height = 20
  Placement = pos=(0,0,36.15) rot=(0,0,1;0rad)
  Radius = 7
FEATURE [Part::Cylinder] Cylinder013
  Angle = 360
  AttacherType = Attacher::AttachEngine3D
  Height = 10
  Placement = pos=(0,0,36.15) rot=(0,0,1;0rad)
  Radius = 4
FEATURE [Part::MultiFuse] Fusion032  label="removeToCreteHoleForPlugHousing003"
  Placement = pos=(70,19,36) rot=(0,1,0;1.5708rad)
  Shapes = -> [Cylinder012,Cylinder013]
FEATURE [Part::Cut] Cut007  label="bottom002"
  Base = -> Cut002
  Tool = -> Fusion032
FEATURE [Sketcher::SketchObject] Sketch008
  FullyConstrained = true
  sketch-geometry (54):
    g0: LineSegment StartX=-4.2 StartY=0 StartZ=0 EndX=-6.2 EndY=0 EndZ=0
    g1: LineSegment StartX=-14 StartY=-18 StartZ=0 EndX=-14 EndY=-26.5 EndZ=0
    g2: LineSegment StartX=-4.2 StartY=0 StartZ=0 EndX=-4.2 EndY=-13.4877 EndZ=0
    g3: Circle CenterX=-4.2 CenterY=-13.4877 CenterZ=0 NormalX=0 NormalY=0 NormalZ=1 AngleXU=0 Radius=1
    g4: Circle CenterX=-4.2 CenterY=-26.5 CenterZ=0 NormalX=0 NormalY=0 NormalZ=1 AngleXU=0 Radius=1
    g5: Circle CenterX=-8.2 CenterY=-26.5 CenterZ=0 NormalX=0 NormalY=0 NormalZ=1 AngleXU=0 Radius=1
    g6: BSplineCurve PolesCount=3 KnotsCount=2 Degree=2 IsPeriodic=0
    g7: GeomPoint X=-4.2 Y=-13.4877 Z=0
    g8: GeomPoint X=-8.2 Y=-26.5 Z=0
    g9: LineSegment StartX=-14 StartY=-26.5 StartZ=0 EndX=-8.2 EndY=-26.5 EndZ=0
    g10: LineSegment StartX=-10.15 StartY=-12 StartZ=0 EndX=-10.15 EndY=-14 EndZ=0
    g11: LineSegment StartX=-12.8401 StartY=-16 StartZ=0 EndX=-10.1571 EndY=-16 EndZ=0
    g12: LineSegment StartX=-10.15 StartY=-14 StartZ=0 EndX=-8.70761 EndY=-14 EndZ=0
    g13: LineSegment StartX=-12.8401 StartY=-16 StartZ=0 EndX=-12.8401 EndY=-17.6958 EndZ=0
    g14: LineSegment StartX=-10.15 StartY=-12 StartZ=0 EndX=-7.79258 EndY=-12 EndZ=0
    g15: Circle CenterX=-6.2215 CenterY=-2 CenterZ=0 NormalX=0 NormalY=0 NormalZ=1 AngleXU=0 Radius=1
    g16: Circle CenterX=-6.22762 CenterY=-2.58724 CenterZ=0 NormalX=0 NormalY=0 NormalZ=1 AngleXU=0 Radius=1
    g17: Circle CenterX=-6.32538 CenterY=-4 CenterZ=0 NormalX=0 NormalY=0 NormalZ=1 AngleXU=0 Radius=1
    g18: BSplineCurve PolesCount=3 KnotsCount=2 Degree=2 IsPeriodic=0
    g19: GeomPoint X=-6.2215 Y=-2 Z=0
    g20: GeomPoint X=-6.32538 Y=-4 Z=0
    g21: Circle CenterX=-6.48644 CenterY=-5.99526 CenterZ=0 NormalX=0 NormalY=0 NormalZ=1 AngleXU=0 Radius=1
    g22: Circle CenterX=-6.58486 CenterY=-6.99526 CenterZ=0 NormalX=0 NormalY=0 NormalZ=1 AngleXU=0 Radius=1
    g23: Circle CenterX=-6.77343 CenterY=-8 CenterZ=0 NormalX=0 NormalY=0 NormalZ=1 AngleXU=0 Radius=1
    g24: BSplineCurve PolesCount=3 KnotsCount=2 Degree=2 IsPeriodic=0
    g25: GeomPoint X=-6.48644 Y=-5.99526 Z=0
    g26: GeomPoint X=-6.77343 Y=-8 Z=0
    g27: Circle CenterX=-7.19003 CenterY=-10 CenterZ=0 NormalX=0 NormalY=0 NormalZ=1 AngleXU=0 Radius=1
    g28: Circle CenterX=-7.44407 CenterY=-11.0915 CenterZ=0 NormalX=0 NormalY=0 NormalZ=1 AngleXU=0 Radius=1
    g29: Circle CenterX=-7.79258 CenterY=-12 CenterZ=0 NormalX=0 NormalY=0 NormalZ=1 AngleXU=0 Radius=1
    g30: BSplineCurve PolesCount=3 KnotsCount=2 Degree=2 IsPeriodic=0
    g31: GeomPoint X=-7.19003 Y=-10 Z=0
    g32: GeomPoint X=-7.79258 Y=-12 Z=0
    g33: Circle CenterX=-8.70761 CenterY=-14 CenterZ=0 NormalX=0 NormalY=0 NormalZ=1 AngleXU=0 Radius=1
    g34: Circle CenterX=-9.33087 CenterY=-15.1837 CenterZ=0 NormalX=0 NormalY=0 NormalZ=1 AngleXU=0 Radius=1
    g35: Circle CenterX=-10.1571 CenterY=-16 CenterZ=0 NormalX=0 NormalY=0 NormalZ=1 AngleXU=0 Radius=1
    g36: BSplineCurve PolesCount=3 KnotsCount=2 Degree=2 IsPeriodic=0
    g37: GeomPoint X=-8.70761 Y=-14 Z=0
    g38: GeomPoint X=-10.1571 Y=-16 Z=0
    g39: Circle CenterX=-12.8401 CenterY=-17.6958 CenterZ=0 NormalX=0 NormalY=0 NormalZ=1 AngleXU=0 Radius=1
    g40: Circle CenterX=-13.3521 CenterY=-17.9027 CenterZ=0 NormalX=0 NormalY=0 NormalZ=1 AngleXU=0 Radius=1
    g41: Circle CenterX=-14 CenterY=-18 CenterZ=0 NormalX=0 NormalY=0 NormalZ=1 AngleXU=0 Radius=1
    g42: BSplineCurve PolesCount=3 KnotsCount=2 Degree=2 IsPeriodic=0
    g43: GeomPoint X=-12.8401 Y=-17.6958 Z=0
    g44: GeomPoint X=-14 Y=-18 Z=0
    g45: LineSegment StartX=-6.2 StartY=0 StartZ=0 EndX=-7.2 EndY=0 EndZ=0
    g46: LineSegment StartX=-7.2 StartY=0 StartZ=0 EndX=-7.2 EndY=-2 EndZ=0
    g47: LineSegment StartX=-7.2 StartY=-2 StartZ=0 EndX=-6.2215 EndY=-2 EndZ=0
    g48: LineSegment StartX=-6.32538 StartY=-4 StartZ=0 EndX=-7.65538 EndY=-4 EndZ=0
    g49: LineSegment StartX=-7.65538 StartY=-4 StartZ=0 EndX=-7.65538 EndY=-5.99526 EndZ=0
    g50: LineSegment StartX=-7.65538 StartY=-5.99526 StartZ=0 EndX=-6.48644 EndY=-5.99526 EndZ=0
    g51: LineSegment StartX=-6.77343 StartY=-8 StartZ=0 EndX=-8.43343 EndY=-8 EndZ=0
    g52: LineSegment StartX=-8.43343 StartY=-8 StartZ=0 EndX=-8.43343 EndY=-10 EndZ=0
    g53: LineSegment StartX=-8.43343 StartY=-10 StartZ=0 EndX=-7.19003 EndY=-10 EndZ=0
  constraints (112):
    c: Horizontal(g0)
    c: Distance(g0) = 2
    c: Block(g0)
    c: Vertical(g1)
    c: Coincident(g2,g0)
    c: Vertical(g2)
    c: Block(g2)
    c: Coincident(g6,g2)
    c: Weight(g3) = 1
    c: Equal(g3,g4)
    c: Equal(g3,g5)
    c: InternalAlignment(g3,g6)
    c: InternalAlignment(g4,g6)
    c: InternalAlignment(g5,g6)
    c: InternalAlignment(g7,g6)
    c: InternalAlignment(g8,g6)
    c: Block(g6)
    c: Coincident(g9,g1)
    c: Coincident(g9,g6)
    c: Horizontal(g9)
    c: Vertical(g10)
    c: Block(g10)
    c: Horizontal(g11)
    c: Block(g11)
    c: Coincident(g12,g10)
    c: Horizontal(g12)
    c: Block(g12)
    c: Coincident(g13,g11)
    c: Vertical(g13)
    c: Block(g13)
    c: Coincident(g14,g10)
    c: Horizontal(g14)
    c: Block(g14)
    c: Block(g9)
    c: Block(g1)
    c: Weight(g15) = 1
    c: Equal(g15,g16)
    c: Equal(g15,g17)
    c: InternalAlignment(g15,g18)
    c: InternalAlignment(g16,g18)
    c: InternalAlignment(g17,g18)
    c: InternalAlignment(g19,g18)
    c: InternalAlignment(g20,g18)
    c: Weight(g21) = 1
    c: Equal(g21,g22)
    c: Equal(g21,g23)
    c: InternalAlignment(g21,g24)
    c: InternalAlignment(g22,g24)
    c: InternalAlignment(g23,g24)
    c: InternalAlignment(g25,g24)
    c: InternalAlignment(g26,g24)
    c: Weight(g27) = 1
    c: Equal(g27,g28)
    c: Equal(g27,g29)
    c: Coincident(g30,g14)
    c: InternalAlignment(g27,g30)
    c: InternalAlignment(g28,g30)
    c: InternalAlignment(g29,g30)
    c: InternalAlignment(g31,g30)
    c: InternalAlignment(g32,g30)
    c: Coincident(g36,g12)
    c: Weight(g33) = 1
    c: Equal(g33,g34)
    c: Equal(g33,g35)
    c: Coincident(g36,g11)
    c: InternalAlignment(g33,g36)
    c: InternalAlignment(g34,g36)
    c: InternalAlignment(g35,g36)
    c: InternalAlignment(g37,g36)
    c: InternalAlignment(g38,g36)
    c: Coincident(g42,g13)
    c: Weight(g39) = 1
    c: Equal(g39,g40)
    c: Equal(g39,g41)
    c: Coincident(g42,g1)
    c: InternalAlignment(g39,g42)
    c: InternalAlignment(g40,g42)
    c: InternalAlignment(g41,g42)
    c: InternalAlignment(g43,g42)
    c: InternalAlignment(g44,g42)
    c: Block(g18)
    c: Block(g24)
    c: Block(g30)
    c: Block(g36)
    c: Block(g42)
    c: Horizontal(g45)
    c: Coincident(g45,g0)
    c: Vertical(g46)
    c: Coincident(g46,g45)
    c: Coincident(g47,g46)
    c: Coincident(g47,g18)
    c: Horizontal(g47)
    c: Block(g46)
    c: Coincident(g48,g18)
    c: Horizontal(g48)
    c: Distance(g48) = 1.33
    c: Vertical(g49)
    c: Coincident(g49,g48)
    c: Coincident(g50,g49)
    c: Coincident(g50,g24)
    c: Horizontal(g50)
    c: Tangent(g50,g22)
    c: Horizontal(g51)
    c: Coincident(g51,g24)
    c: Block(g51)
    c: Vertical(g52)
    c: Block(g52)
    c: Coincident(g52,g51)
    c: Coincident(g53,g52)
    c: Coincident(g53,g30)
    c: Horizontal(g53)
    c: Distance(g1) = 8.5
FEATURE [Part::Feature] Face024
  shape: bbox 9.8 x 26.5 x 2e-07 mm, 1 faces, 0 solids (baked)
FEATURE [Part::Revolution] Revolve024
  Angle = 360
  Axis = (0,1,0)
  Base = (0,0,0)
  FaceMakerClass = Part::FaceMakerBullseye
  Placement = pos=(0,0,0) rot=(0,0,1;1.5708rad)
  Solid = false
  Source = -> Face024
  Symmetric = false
FEATURE [Part::Feature] Face025
  shape: bbox 9.8 x 26.5 x 2e-07 mm, 1 faces, 0 solids (baked)
FEATURE [Part::Revolution] Revolve025
  Angle = 360
  Axis = (0,1,0)
  Base = (0,0,0)
  FaceMakerClass = Part::FaceMakerBullseye
  Placement = pos=(0,0,0) rot=(0,0,1;1.5708rad)
  Solid = false
  Source = -> Face025
  Symmetric = false
FEATURE [Part::MultiFuse] Fusion033
  Placement = pos=(-18,19,36) rot=(0,0,1;0rad)
  Shapes = -> [Revolve025,Revolve024]
FEATURE [Part::Cylinder] Cylinder014
  Angle = 360
  AttacherType = Attacher::AttachEngine3D
  Height = 20
  Placement = pos=(0,0,36.15) rot=(0,0,1;0rad)
  Radius = 14.3
FEATURE [Part::Cylinder] Cylinder015
  Angle = 360
  AttacherType = Attacher::AttachEngine3D
  Height = 10
  Placement = pos=(0,0,36.15) rot=(0,0,1;0rad)
  Radius = 4
FEATURE [Part::MultiFuse] Fusion034  label="removeToCreteHoleForPlugHousing004"
  Placement = pos=(-42,19,36) rot=(0,1,0;1.5708rad)
  Shapes = -> [Cylinder014,Cylinder015]
FEATURE [Part::Cut] Cut008  label="top004"
  Base = -> Cut004
  Placement = pos=(-1,0,0) rot=(0,0,1;0rad)
  Tool = -> Fusion034
FEATURE [Part::Box] Box005  label="Cube005"
  AttacherType = Attacher::AttachEngine3D
  Height = 28
  Length = 3
  Placement = pos=(110.7,19,22) rot=(0,0,1;0rad)
  Width = 15.7
FEATURE [Part::Cylinder] Cylinder016
  Angle = 360
  AttacherType = Attacher::AttachEngine3D
  Height = 10
  Placement = pos=(0,0,36.15) rot=(0,0,1;0rad)
  Radius = 4
FEATURE [Part::Cylinder] Cylinder017
  Angle = 360
  AttacherType = Attacher::AttachEngine3D
  Height = 20
  Placement = pos=(0,0,36.15) rot=(0,0,1;0rad)
  Radius = 10.3
FEATURE [Part::MultiFuse] Fusion035  label="removeToCreteHoleForPlugHousing005"
  Placement = pos=(70,19,36) rot=(0,1,0;1.5708rad)
  Shapes = -> [Cylinder017,Cylinder016]
FEATURE [Part::Cut] Cut009  label="plugHousingTab001"
  Base = -> Box005
  Placement = pos=(-107.4,-14,0) rot=(0,0,1;0rad)
  Tool = -> Fusion035
FEATURE [Part::Box] Box006  label="Cube006"
  AttacherType = Attacher::AttachEngine3D
  Height = 28
  Length = 3
  Placement = pos=(110.7,19,22) rot=(0,0,1;0rad)
  Width = 15.7
FEATURE [Part::Cylinder] Cylinder018
  Angle = 360
  AttacherType = Attacher::AttachEngine3D
  Height = 10
  Placement = pos=(0,0,36.15) rot=(0,0,1;0rad)
  Radius = 4
FEATURE [Part::Cylinder] Cylinder019
  Angle = 360
  AttacherType = Attacher::AttachEngine3D
  Height = 20
  Placement = pos=(0,0,36.15) rot=(0,0,1;0rad)
  Radius = 10.3
FEATURE [Part::MultiFuse] Fusion036  label="removeToCreteHoleForPlugHousing006"
  Placement = pos=(70,19,36) rot=(0,1,0;1.5708rad)
  Shapes = -> [Cylinder019,Cylinder018]
FEATURE [Part::Cut] Cut010  label="plugHousingTab002"
  Base = -> Box006
  Placement = pos=(-107.4,-14,0) rot=(0,0,1;0rad)
  Tool = -> Fusion036
FEATURE [Part::MultiFuse] Fusion037
  Placement = pos=(9.6,23,0) rot=(0,0,1;3.14159rad)
  Shapes = -> [Cut009,Cut010]
FEATURE [Part::Box] Box  label="Cube"
  AttacherType = Attacher::AttachEngine3D
  Height = 10
  Length = 3
  Placement = pos=(3.3,4,12) rot=(0,0,1;0rad)
  Width = 10
FEATURE [Part::Fillet] Fillet004
  Base = -> Fusion028
  Edges = 1 edges r=2: [Edge25]
FEATURE [Part::Fillet] Fillet005  label="plugHousing046"
  Base = -> Fillet004
  Edges = 1 edges r=2: [Edge8]
FEATURE [Part::Fillet] Fillet006
  Base = -> Box
  Edges = 1 edges r=2: [Edge11]
FEATURE [Part::Box] Box007  label="Cube007"
  AttacherType = Attacher::AttachEngine3D
  Height = 10
  Length = 3
  Placement = pos=(3.3,4,50) rot=(0,0,1;0rad)
  Width = 10
FEATURE [Part::Fillet] Fillet007
  Base = -> Box007
  Edges = 1 edges r=2: [Edge12]
FEATURE [Part::Box] Box008  label="Cube008"
  AttacherType = Attacher::AttachEngine3D
  Height = 28
  Length = 4
  Placement = pos=(5,0,22) rot=(0,0,1;0rad)
  Width = 10
FEATURE [Part::Fillet] Fillet008
  Base = -> Box008
  Edges = 1 edges r=1: [Edge7]
FEATURE [Part::Fillet] Fillet009
  Base = -> Fillet008
  Edges = 1 edges r=2: [Edge5]
FEATURE [Part::Fillet] Fillet010
  Base = -> Fillet009
  Edges = 1 edges r=2: [Edge2]
FEATURE [Sketcher::SketchObject] Sketch009  label="topSketch003"
  FullyConstrained = true
  sketch-geometry (4):
    g0: LineSegment StartX=16.8446 StartY=31.512 StartZ=0 EndX=16.3251 EndY=34.4666 EndZ=0
    g1: ArcOfCircle CenterX=19 CenterY=19.2524 CenterZ=0 NormalX=0 NormalY=0 NormalZ=1 AngleXU=0 Radius=15.4476 StartAngle=1.74483 EndAngle=2.72717
    g2: ArcOfCircle CenterX=19 CenterY=19.2524 CenterZ=0 NormalX=0 NormalY=0 NormalZ=1 AngleXU=0 Radius=12.4476 StartAngle=1.74483 EndAngle=2.73189
    g3: LineSegment StartX=4.86004 StartY=25.4725 StartZ=0 EndX=7.58253 EndY=24.2107 EndZ=0
  constraints (7):
    c: Block(g0)
    c: Coincident(g1,g0)
    c: Coincident(g2,g0)
    c: Coincident(g3,g1)
    c: Coincident(g3,g2)
    c: Block(g1)
    c: Block(g2)
FEATURE [Part::Extrusion] Extrude008
  Base = -> Sketch009
  Dir = (0,0,1)
  DirMode = 2
  FaceMakerClass = Part::FaceMakerBullseye
  LengthFwd = 10
  LengthRev = 0
  Placement = pos=(0,0,31) rot=(0,0,1;0rad)
  Solid = true
  Symmetric = false
FEATURE [Part::Cylinder] Cylinder020
  Angle = 360
  AttacherType = Attacher::AttachEngine3D
  Height = 20
  Placement = pos=(0,0,36.15) rot=(0,0,1;0rad)
  Radius = 8.2
FEATURE [Part::Cylinder] Cylinder021
  Angle = 360
  AttacherType = Attacher::AttachEngine3D
  Height = 10
  Placement = pos=(0,0,36.15) rot=(0,0,1;0rad)
  Radius = 4
FEATURE [Part::MultiFuse] Fusion038  label="removeToCreteHoleForPlugHousing007"
  Placement = pos=(-42,19,36) rot=(0,1,0;1.5708rad)
  Shapes = -> [Cylinder020,Cylinder021]
FEATURE [Part::Cut] Cut011
  Base = -> Extrude008
  Tool = -> Fusion038
FEATURE [Part::Fillet] Fillet011
  Base = -> Cut011
  Edges = 1 edges r=2: [Edge1]
FEATURE [Part::Fillet] Fillet012
  Base = -> Fillet011
  Edges = 1 edges r=2.5: [Edge1]
FEATURE [Part::Fillet] Fillet013
  Base = -> Fillet012
  Edges = 1 edges r=2.5: [Edge2]
FEATURE [Part::Box] Box010  label="Cube010"
  AttacherType = Attacher::AttachEngine3D
  Height = 16
  Length = 8
  Placement = pos=(12.7,31.52,28) rot=(0,0,1;0rad)
  Width = 4
FEATURE [Sketcher::SketchObject] Sketch010  label="topSketch004"
  FullyConstrained = true
  sketch-geometry (4):
    g0: LineSegment StartX=16.8446 StartY=31.512 StartZ=0 EndX=16.3251 EndY=34.4666 EndZ=0
    g1: ArcOfCircle CenterX=19 CenterY=19.2524 CenterZ=0 NormalX=0 NormalY=0 NormalZ=1 AngleXU=0 Radius=15.4476 StartAngle=1.74483 EndAngle=2.72717
    g2: ArcOfCircle CenterX=19 CenterY=19.2524 CenterZ=0 NormalX=0 NormalY=0 NormalZ=1 AngleXU=0 Radius=12.4476 StartAngle=1.74483 EndAngle=2.73189
    g3: LineSegment StartX=4.86004 StartY=25.4725 StartZ=0 EndX=7.58253 EndY=24.2107 EndZ=0
  constraints (7):
    c: Block(g0)
    c: Coincident(g1,g0)
    c: Coincident(g2,g0)
    c: Coincident(g3,g1)
    c: Coincident(g3,g2)
    c: Block(g1)
    c: Block(g2)
FEATURE [Part::Cylinder] Cylinder022
  Angle = 360
  AttacherType = Attacher::AttachEngine3D
  Height = 10
  Placement = pos=(0,0,36.15) rot=(0,0,1;0rad)
  Radius = 4
FEATURE [Sketcher::SketchObject] Sketch011  label="topSketch005"
  FullyConstrained = true
  sketch-geometry (4):
    g0: LineSegment StartX=16.8446 StartY=31.512 StartZ=0 EndX=16.3251 EndY=34.4666 EndZ=0
    g1: ArcOfCircle CenterX=19 CenterY=19.2524 CenterZ=0 NormalX=0 NormalY=0 NormalZ=1 AngleXU=0 Radius=15.4476 StartAngle=1.74483 EndAngle=2.72717
    g2: ArcOfCircle CenterX=19 CenterY=19.2524 CenterZ=0 NormalX=0 NormalY=0 NormalZ=1 AngleXU=0 Radius=12.4476 StartAngle=1.74483 EndAngle=2.73189
    g3: LineSegment StartX=4.86004 StartY=25.4725 StartZ=0 EndX=7.58253 EndY=24.2107 EndZ=0
  constraints (7):
    c: Block(g0)
    c: Coincident(g1,g0)
    c: Coincident(g2,g0)
    c: Coincident(g3,g1)
    c: Coincident(g3,g2)
    c: Block(g1)
    c: Block(g2)
FEATURE [Part::Extrusion] Extrude010
  Base = -> Sketch011
  Dir = (0,0,1)
  DirMode = 2
  FaceMakerClass = Part::FaceMakerBullseye
  LengthFwd = 10.6
  LengthRev = 0
  Placement = pos=(0,0,31) rot=(0,0,1;0rad)
  Solid = true
  Symmetric = false
FEATURE [Part::Cylinder] Cylinder023
  Angle = 360
  AttacherType = Attacher::AttachEngine3D
  Height = 20
  Placement = pos=(0,0,36.15) rot=(0,0,1;0rad)
  Radius = 8.2
FEATURE [Part::MultiFuse] Fusion039  label="removeToCreteHoleForPlugHousing008"
  Placement = pos=(-42,19,36) rot=(0,1,0;1.5708rad)
  Shapes = -> [Cylinder023,Cylinder022]
FEATURE [Part::Cut] Cut012
  Base = -> Extrude010
  Placement = pos=(0,0,-0.3) rot=(0,0,1;0rad)
  Tool = -> Fusion039
FEATURE [Part::Cut] Cut013
  Base = -> Box010
  Tool = -> Cut012
FEATURE [Part::Fillet] Fillet014
  Base = -> Cut013
  Edges = 1 edges r=0.7: [Edge13]
FEATURE [Part::Fillet] Fillet015
  Base = -> Fillet014
  Edges = 1 edges r=0.7: [Edge13]
FEATURE [Part::Fillet] Fillet016
  Base = -> Fillet015
  Edges = 1 edges r=0.7: [Edge16]
FEATURE [Part::Fillet] Fillet017
  Base = -> Fillet016
  Edges = 1 edges r=0.7: [Edge11]
FEATURE [Part::Fillet] Fillet018
  Base = -> Fillet017
  Edges = 1 edges r=0.7: [Edge10]
FEATURE [Part::Fillet] Fillet019
  Base = -> Fillet018
  Edges = 1 edges r=1.2: [Edge5]
FEATURE [Part::Fillet] Fillet020
  Base = -> Fillet019
  Edges = 1 edges r=1.2: [Edge12]
FEATURE [Part::Fillet] Fillet021
  Base = -> Fillet020
  Edges = 1 edges r=2: [Edge1]
  Placement = pos=(0.3,0,0) rot=(0,0,1;0rad)
FEATURE [Part::MultiFuse] Fusion040  label="top005"
  Shapes = -> [Cut008,Fillet021]
FEATURE [Part::MultiFuse] Fusion041  label="wireHolder"
  Shapes = -> [Fusion033,Fillet013]
FEATURE [Part::MultiFuse] Fusion042
  Shapes = -> [Fillet007,Fusion041]
FEATURE [Part::MultiFuse] Fusion043  label="wireHolder001"
  Shapes = -> [Fusion042,Fillet010]
FEATURE [Part::MultiFuse] Fusion044  label="wireHolder002"
  Shapes = -> [Fillet006,Fusion037,Fusion043]
FEATURE [Part::Feature] Face026
  shape: bbox 11 x 6 x 2e-07 mm, 1 faces, 0 solids (baked)
FEATURE [Part::Revolution] Revolve026
  Angle = 360
  Axis = (0,1,0)
  Base = (0,0,0)
  FaceMakerClass = Part::FaceMakerBullseye
  Placement = pos=(30.3,-1,19.7) rot=(0,0,1;0rad)
  Solid = false
  Source = -> Face026
  Symmetric = false
FEATURE [Sketcher::SketchObject] Sketch013  label="topSketch006"
  FullyConstrained = true
  sketch-geometry (13):
    g0: LineSegment StartX=117 StartY=19 StartZ=0 EndX=117 EndY=38 EndZ=0
    g1: ArcOfCircle CenterX=98 CenterY=19 CenterZ=0 NormalX=0 NormalY=0 NormalZ=1 AngleXU=0 Radius=19 StartAngle=5.7297 EndAngle=6.28319
    g2: LineSegment StartX=0 StartY=3 StartZ=0 EndX=0 EndY=19 EndZ=0
    g3: LineSegment StartX=19 StartY=38 StartZ=0 EndX=117 EndY=38 EndZ=0
    g4: ArcOfCircle CenterX=19 CenterY=19 CenterZ=0 NormalX=0 NormalY=0 NormalZ=1 AngleXU=0 Radius=19 StartAngle=1.5708 EndAngle=3.14159
    g5: ArcOfCircle CenterX=19 CenterY=19 CenterZ=0 NormalX=0 NormalY=0 NormalZ=1 AngleXU=0 Radius=16 StartAngle=1.5708 EndAngle=3.14159
    g6: ArcOfCircle CenterX=98 CenterY=19 CenterZ=0 NormalX=0 NormalY=0 NormalZ=1 AngleXU=0 Radius=16 StartAngle=5.60905 EndAngle=6.28319
    g7: LineSegment StartX=114 StartY=19 StartZ=0 EndX=114 EndY=35 EndZ=0
    g8: LineSegment StartX=110.5 StartY=9.01251 StartZ=0 EndX=114.163 EndY=9.01251 EndZ=0
    g9: LineSegment StartX=114 StartY=35 StartZ=0 EndX=19 EndY=35 EndZ=0
    g10: LineSegment StartX=0 StartY=3 StartZ=0 EndX=0 EndY=0 EndZ=0
    g11: LineSegment StartX=3 StartY=0 StartZ=0 EndX=0 EndY=0 EndZ=0
    g12: LineSegment StartX=3 StartY=19 StartZ=0 EndX=3 EndY=0 EndZ=0
  constraints (33):
    c: Vertical(g0)
    c: Distance(g0) = 19
    c: Block(g0)
    c: Coincident(g1,g0)
    c: Block(g1)
    c: Vertical(g2)
    c: Block(g2)
    c: Coincident(g3,g0)
    c: Horizontal(g3)
    c: Distance(g3) = 98
    c: Coincident(g4,g3)
    c: Coincident(g4,g2)
    c: Block(g4)
    c: Coincident(g5,g4)
    c: Coincident(g6,g1)
    c: Block(g6)
    c: Block(g5)
    c: Coincident(g7,g6)
    c: Vertical(g7)
    c: Coincident(g8,g6)
    c: Coincident(g8,g1)
    c: Coincident(g9,g7)
    c: Coincident(g9,g5)
    c: Horizontal(g9)
    c: Tangent(g9,g5)
    c: Coincident(g10,g2)
    c: Distance(g10) = 3
    c: Vertical(g10)
    c: Coincident(g11,g10)
    c: Horizontal(g11)
    c: Coincident(g12,g5)
    c: Coincident(g12,g11)
    c: Vertical(g12)
FEATURE [Part::Extrusion] Extrude011  label="top006"
  Base = -> Sketch013
  Dir = (0,0,1)
  DirMode = 2
  FaceMakerClass = Part::FaceMakerBullseye
  LengthFwd = 72
  LengthRev = 0
  Solid = true
  Symmetric = false
FEATURE [Sketcher::SketchObject] Sketch014
  FullyConstrained = true
  MapMode = 3
  Placement = pos=(0,0,0) rot=(1,0,0;1.5708rad)
  Support = -> [Extrude011]
  sketch-geometry (8):
    g0: Circle CenterX=80.351 CenterY=-67.6202 CenterZ=0 NormalX=0 NormalY=0 NormalZ=1 AngleXU=0 Radius=2
    g1: Circle CenterX=80.351 CenterY=-67.6202 CenterZ=0 NormalX=0 NormalY=0 NormalZ=1 AngleXU=0 Radius=3
    g2: Circle CenterX=80.351 CenterY=-4.92017 CenterZ=0 NormalX=0 NormalY=0 NormalZ=1 AngleXU=0 Radius=2
    g3: Circle CenterX=80.351 CenterY=-4.92017 CenterZ=0 NormalX=0 NormalY=0 NormalZ=1 AngleXU=0 Radius=3
    g4: Circle CenterX=23.851 CenterY=-4.92017 CenterZ=0 NormalX=0 NormalY=0 NormalZ=1 AngleXU=0 Radius=2
    g5: Circle CenterX=23.851 CenterY=-4.92017 CenterZ=0 NormalX=0 NormalY=0 NormalZ=1 AngleXU=0 Radius=3
    g6: Circle CenterX=23.851 CenterY=-67.6202 CenterZ=0 NormalX=0 NormalY=0 NormalZ=1 AngleXU=0 Radius=2
    g7: Circle CenterX=23.851 CenterY=-67.6202 CenterZ=0 NormalX=0 NormalY=0 NormalZ=1 AngleXU=0 Radius=3
  constraints (8):
    c: Block(g3)
    c: Block(g2)
    c: Block(g1)
    c: Block(g0)
    c: Block(g6)
    c: Block(g7)
    c: Block(g4)
    c: Block(g5)
FEATURE [Part::Feature] Face027
  shape: bbox 11 x 6 x 2e-07 mm, 1 faces, 0 solids (baked)
FEATURE [Part::Revolution] Revolve027
  Angle = 360
  Axis = (0,1,0)
  Base = (0,0,0)
  FaceMakerClass = Part::FaceMakerBullseye
  Placement = pos=(30.3,-1,51.7) rot=(0,0,1;0rad)
  Solid = false
  Source = -> Face027
  Symmetric = false
FEATURE [Part::Feature] Face028
  shape: bbox 11 x 6 x 2e-07 mm, 1 faces, 0 solids (baked)
FEATURE [Part::Revolution] Revolve028
  Angle = 360
  Axis = (0,1,0)
  Base = (0,0,0)
  FaceMakerClass = Part::FaceMakerBullseye
  Placement = pos=(62.3,-1,19.7) rot=(0,0,1;0rad)
  Solid = false
  Source = -> Face028
  Symmetric = false
FEATURE [Part::Feature] Face029
  shape: bbox 11 x 6 x 2e-07 mm, 1 faces, 0 solids (baked)
FEATURE [Part::Revolution] Revolve029
  Angle = 360
  Axis = (0,1,0)
  Base = (0,0,0)
  FaceMakerClass = Part::FaceMakerBullseye
  Placement = pos=(62.3,-1,51.7) rot=(0,0,1;0rad)
  Solid = false
  Source = -> Face029
  Symmetric = false
FEATURE [Part::Feature] Wire
  shape: bbox 11 x 5.2 x 2e-07 mm, 0 faces, 0 solids (baked)
FEATURE [Part::Revolution] Revolve030
  Angle = 360
  Axis = (0,1,0)
  Base = (0,0,0)
  FaceMakerClass = Part::FaceMakerBullseye
  Placement = pos=(30.3,38,19.7) rot=(0,0,1;0rad)
  Solid = true
  Source = -> Wire
  Symmetric = false
FEATURE [Part::Feature] Wire001
  shape: bbox 11 x 5.2 x 2e-07 mm, 0 faces, 0 solids (baked)
FEATURE [Part::Revolution] Revolve031
  Angle = 360
  Axis = (0,1,0)
  Base = (0,0,0)
  FaceMakerClass = Part::FaceMakerBullseye
  Placement = pos=(30.3,38,51.7) rot=(0,0,1;0rad)
  Solid = true
  Source = -> Wire001
  Symmetric = false
FEATURE [Part::Feature] Wire002
  shape: bbox 11 x 5.2 x 2e-07 mm, 0 faces, 0 solids (baked)
FEATURE [Part::Revolution] Revolve032
  Angle = 360
  Axis = (0,1,0)
  Base = (0,0,0)
  FaceMakerClass = Part::FaceMakerBullseye
  Placement = pos=(62.3,38,51.7) rot=(0,0,1;0rad)
  Solid = true
  Source = -> Wire002
  Symmetric = false
FEATURE [Part::Feature] Wire003
  shape: bbox 11 x 5.2 x 2e-07 mm, 0 faces, 0 solids (baked)
FEATURE [Part::Revolution] Revolve033
  Angle = 360
  Axis = (0,1,0)
  Base = (0,0,0)
  FaceMakerClass = Part::FaceMakerBullseye
  Placement = pos=(62.3,38,19.7) rot=(0,0,1;0rad)
  Solid = true
  Source = -> Wire003
  Symmetric = false
FEATURE [Part::MultiFuse] Fusion045  label="altRandScrewHousing"
  Shapes = -> [Revolve029,Revolve027,Revolve028,Revolve026]
FEATURE [Part::MultiFuse] Fusion046  label="fanScrewHousing"
  Shapes = -> [Revolve033,Revolve032,Revolve031,Revolve030]
FEATURE [Sketcher::SketchObject] Sketch015
  FullyConstrained = true
  sketch-geometry (17):
    g0: Circle CenterX=-3.5 CenterY=23.5 CenterZ=0 NormalX=0 NormalY=0 NormalZ=1 AngleXU=0 Radius=1
    g1: Circle CenterX=-1 CenterY=15.25 CenterZ=0 NormalX=0 NormalY=0 NormalZ=1 AngleXU=0 Radius=1
    g2: Circle CenterX=-3.5 CenterY=7 CenterZ=0 NormalX=0 NormalY=0 NormalZ=1 AngleXU=0 Radius=1
    g3: BSplineCurve PolesCount=3 KnotsCount=2 Degree=2 IsPeriodic=0
    g4: GeomPoint X=-3.5 Y=23.5 Z=0
    g5: GeomPoint X=-3.5 Y=7 Z=0
    g6: Circle CenterX=-4.8 CenterY=30.5 CenterZ=0 NormalX=0 NormalY=0 NormalZ=1 AngleXU=0 Radius=1
    g7: Circle CenterX=-3.5 CenterY=30.5 CenterZ=0 NormalX=0 NormalY=0 NormalZ=1 AngleXU=0 Radius=1
    g8: Circle CenterX=-3.5 CenterY=29.2 CenterZ=0 NormalX=0 NormalY=0 NormalZ=1 AngleXU=0 Radius=1
    g9: BSplineCurve PolesCount=3 KnotsCount=2 Degree=2 IsPeriodic=0
    g10: GeomPoint X=-4.8 Y=30.5 Z=0
    g11: GeomPoint X=-3.5 Y=29.2 Z=0
    g12: LineSegment StartX=-3.5 StartY=29.2 StartZ=0 EndX=-3.5 EndY=23.5 EndZ=0
    g13: LineSegment StartX=-4.8 StartY=30.5 StartZ=0 EndX=0 EndY=30.5 EndZ=0
    g14: LineSegment StartX=-3.5 StartY=0.3 StartZ=0 EndX=0 EndY=0.3 EndZ=0
    g15: LineSegment StartX=-3.5 StartY=0.3 StartZ=0 EndX=-3.5 EndY=7 EndZ=0
    g16: LineSegment StartX=0 StartY=0.3 StartZ=0 EndX=0 EndY=30.5 EndZ=0
  constraints (33):
    c: Weight(g0) = 1
    c: Equal(g0,g1)
    c: Equal(g0,g2)
    c: InternalAlignment(g0,g3)
    c: InternalAlignment(g1,g3)
    c: InternalAlignment(g2,g3)
    c: InternalAlignment(g4,g3)
    c: InternalAlignment(g5,g3)
    c: Block(g3)
    c: Weight(g6) = 1
    c: Equal(g6,g7)
    c: Equal(g6,g8)
    c: InternalAlignment(g6,g9)
    c: InternalAlignment(g7,g9)
    c: InternalAlignment(g8,g9)
    c: InternalAlignment(g10,g9)
    c: InternalAlignment(g11,g9)
    c: Block(g9)
    c: Coincident(g12,g9)
    c: Coincident(g12,g3)
    c: Vertical(g12)
    c: Coincident(g13,g9)
    c: Horizontal(g13)
    c: Distance(g13) = 4.8
    c: Horizontal(g14)
    c: Block(g14)
    c: Coincident(g15,g14)
    c: Coincident(g15,g3)
    c: Vertical(g15)
    c: Coincident(g16,g14)
    c: Coincident(g16,g13)
    c: Vertical(g16)
    c: Tangent(g16,g1)
FEATURE [Sketcher::SketchObject] Sketch016
  FullyConstrained = true
  sketch-geometry (16):
    g0: Circle CenterX=-3.5 CenterY=23.5 CenterZ=0 NormalX=0 NormalY=0 NormalZ=1 AngleXU=0 Radius=1
    g1: Circle CenterX=-1 CenterY=15.25 CenterZ=0 NormalX=0 NormalY=0 NormalZ=1 AngleXU=0 Radius=1
    g2: Circle CenterX=-3.5 CenterY=7 CenterZ=0 NormalX=0 NormalY=0 NormalZ=1 AngleXU=0 Radius=1
    g3: BSplineCurve PolesCount=3 KnotsCount=2 Degree=2 IsPeriodic=0
    g4: GeomPoint X=-3.5 Y=23.5 Z=0
    g5: GeomPoint X=-3.5 Y=7 Z=0
    g6: LineSegment StartX=-3.5 StartY=28.2 StartZ=0 EndX=-3.5 EndY=23.5 EndZ=0
    g7: LineSegment StartX=0 StartY=29.5 StartZ=0 EndX=0 EndY=30 EndZ=0
    g8: LineSegment StartX=-3.5 StartY=28.2 StartZ=0 EndX=-3.5 EndY=30 EndZ=0
    g9: LineSegment StartX=0 StartY=30 StartZ=0 EndX=0 EndY=30.5 EndZ=0
    g10: LineSegment StartX=0 StartY=30.5 StartZ=0 EndX=-3.5 EndY=30.5 EndZ=0
    g11: LineSegment StartX=-3.5 StartY=30.5 StartZ=0 EndX=-3.5 EndY=30 EndZ=0
    g12: LineSegment StartX=0 StartY=29.5 StartZ=0 EndX=0 EndY=5 EndZ=0
    g13: LineSegment StartX=-3.5 StartY=0.3 StartZ=0 EndX=-3.5 EndY=7 EndZ=0
    g14: LineSegment StartX=-3.5 StartY=0.3 StartZ=0 EndX=0 EndY=0.3 EndZ=0
    g15: LineSegment StartX=0 StartY=5 StartZ=0 EndX=0 EndY=0.3 EndZ=0
  constraints (39):
    c: Weight(g0) = 1
    c: Equal(g0,g1)
    c: Equal(g0,g2)
    c: InternalAlignment(g0,g3)
    c: InternalAlignment(g1,g3)
    c: InternalAlignment(g2,g3)
    c: InternalAlignment(g4,g3)
    c: InternalAlignment(g5,g3)
    c: Block(g3)
    c: Coincident(g6,g3)
    c: Vertical(g6)
    c: Vertical(g7)
    c: Distance(g7) = 0.5
    c: Coincident(g8,g6)
    c: Vertical(g8)
    c: Block(g6)
    c: Block(g7)
    c: Vertical(g9)
    c: Equal(g7,g9) = 0.5
    c: Block(g9)
    c: Coincident(g9,g7)
    c: Horizontal(g10)
    c: Coincident(g10,g9)
    c: Coincident(g11,g10)
    c: Coincident(g11,g8)
    c: Vertical(g11)
    c: Block(g11)
    c: Coincident(g12,g7)
    c: Vertical(g12)
    c: Coincident(g13,g3)
    c: Vertical(g13)
    c: Distance(g13) = 6.7
    c: Coincident(g14,g13)
    c: Horizontal(g14)
    c: Block(g14)
    c: Coincident(g15,g12)
    c: Coincident(g15,g14)
    c: Vertical(g15)
    c: Block(g15)
FEATURE [Sketcher::SketchObject] Sketch017
  FullyConstrained = true
  sketch-geometry (11):
    g0: LineSegment StartX=-3.5 StartY=1e-16 StartZ=0 EndX=-1.6 EndY=1e-16 EndZ=0
    g1: LineSegment StartX=-1.6 StartY=1e-16 StartZ=0 EndX=-1.6 EndY=1.5 EndZ=0
    g2: LineSegment StartX=-3.5 StartY=1.5 StartZ=0 EndX=-1.6 EndY=1.5 EndZ=0
    g3: LineSegment StartX=-3.5 StartY=1e-16 StartZ=0 EndX=-4.8 EndY=1e-16 EndZ=0
    g4: Circle CenterX=-3.5 CenterY=1.3 CenterZ=0 NormalX=0 NormalY=0 NormalZ=1 AngleXU=0 Radius=1
    g5: Circle CenterX=-3.5 CenterY=1e-16 CenterZ=0 NormalX=0 NormalY=0 NormalZ=1 AngleXU=0 Radius=1
    g6: Circle CenterX=-4.8 CenterY=1e-16 CenterZ=0 NormalX=0 NormalY=0 NormalZ=1 AngleXU=0 Radius=1
    g7: BSplineCurve PolesCount=3 KnotsCount=2 Degree=2 IsPeriodic=0
    g8: GeomPoint X=-3.5 Y=1.3 Z=0
    g9: GeomPoint X=-4.8 Y=1e-16 Z=0
    g10: LineSegment StartX=-3.5 StartY=1.3 StartZ=0 EndX=-3.5 EndY=1.5 EndZ=0
  constraints (24):
    c: Horizontal(g0)
    c: Distance(g0) = 1.9
    c: Block(g0)
    c: Coincident(g1,g0)
    c: Vertical(g1)
    c: Coincident(g2,g1)
    c: Horizontal(g2)
    c: Coincident(g3,g0)
    c: Horizontal(g3)
    c: Distance(g3) = 1.3
    c: Weight(g4) = 1
    c: Equal(g4,g5)
    c: Coincident(g5,g0)
    c: Equal(g4,g6)
    c: Coincident(g7,g3)
    c: InternalAlignment(g4,g7)
    c: InternalAlignment(g5,g7)
    c: InternalAlignment(g6,g7)
    c: InternalAlignment(g8,g7)
    c: InternalAlignment(g9,g7)
    c: Coincident(g10,g7)
    c: Coincident(g10,g2)
    c: Vertical(g10)
    c: Block(g10)
FEATURE [Part::Feature] Face035
  shape: bbox 3.2 x 1.5 x 2e-07 mm, 1 faces, 0 solids (baked)
FEATURE [Part::Revolution] Revolve039  label="backCaseScrewRetainer"
  Angle = 360
  Axis = (0,1,0)
  Base = (0,0,0)
  FaceMakerClass = Part::FaceMakerBullseye
  Placement = pos=(12.5,3,62) rot=(0,0,1;0rad)
  Solid = false
  Source = -> Face035
  Symmetric = false
FEATURE [Part::Feature] Face036
  shape: bbox 3.2 x 1.5 x 2e-07 mm, 1 faces, 0 solids (baked)
FEATURE [Part::Feature] Face039
  shape: bbox 4.8 x 30.2 x 2e-07 mm, 1 faces, 0 solids (baked)
FEATURE [Part::Revolution] Revolve043  label="frontCaseScrewPost002"
  Angle = 360
  Axis = (0,1,0)
  Base = (0,0,0)
  FaceMakerClass = Part::FaceMakerBullseye
  Placement = pos=(89.5,4.5,3.5) rot=(0,0,1;0rad)
  Solid = false
  Source = -> Face039
  Symmetric = false
FEATURE [Part::Feature] Face042
  shape: bbox 4.8 x 30.2 x 2e-07 mm, 1 faces, 0 solids (baked)
FEATURE [Part::Revolution] Revolve046  label="frontCaseScrewPost003"
  Angle = 360
  Axis = (0,1,0)
  Base = (0,0,0)
  FaceMakerClass = Part::FaceMakerBullseye
  Placement = pos=(89.5,4.5,68.5) rot=(0,0,1;0rad)
  Solid = false
  Source = -> Face042
  Symmetric = false
FEATURE [Part::Feature] Face043
  shape: bbox 3.2 x 1.5 x 2e-07 mm, 1 faces, 0 solids (baked)
FEATURE [Part::Revolution] Revolve047  label="frontCaseScrewRetainer002"
  Angle = 360
  Axis = (0,1,0)
  Base = (0,0,0)
  FaceMakerClass = Part::FaceMakerBullseye
  Placement = pos=(89.5,3,68.5) rot=(0,0,1;0rad)
  Solid = false
  Source = -> Face043
  Symmetric = false
FEATURE [Part::Feature] Face044
  shape: bbox 3.2 x 1.5 x 2e-07 mm, 1 faces, 0 solids (baked)
FEATURE [Part::Revolution] Revolve048  label="frontCaseScrewRetainer003"
  Angle = 360
  Axis = (0,1,0)
  Base = (0,0,0)
  FaceMakerClass = Part::FaceMakerBullseye
  Placement = pos=(89.5,3,3.5) rot=(0,0,1;0rad)
  Solid = false
  Source = -> Face044
  Symmetric = false
FEATURE [App::MeasureDistance] Distance002  label="Distance: 1.67 mm"
  Distance = 1.66921
  P1 = (99.2361,4.7524,71.7)
  P2 = (99.2347,6.42161,71.7)
FEATURE [Sketcher::SketchObject] Sketch018
  FullyConstrained = true
  sketch-geometry (7):
    g0: LineSegment StartX=0 StartY=0 StartZ=0 EndX=0 EndY=6 EndZ=0
    g1: Circle CenterX=0 CenterY=0 CenterZ=0 NormalX=0 NormalY=0 NormalZ=1 AngleXU=0 Radius=1
    g2: Circle CenterX=8 CenterY=6 CenterZ=0 NormalX=0 NormalY=0 NormalZ=1 AngleXU=0 Radius=1
    g3: BSplineCurve PolesCount=3 KnotsCount=2 Degree=2 IsPeriodic=0
    g4: GeomPoint X=0 Y=0 Z=0
    g5: GeomPoint X=8 Y=6 Z=0
    g6: LineSegment StartX=0 StartY=6 StartZ=0 EndX=8 EndY=6 EndZ=0
  constraints (14):
    c: Coincident(g0,g-1)
    c: Distance(g0) = 6
    c: Vertical(g0)
    c: Coincident(g3,g0)
    c: Weight(g1) = 1
    c: Equal(g1,g2)
    c: InternalAlignment(g1,g3)
    c: InternalAlignment(g2,g3)
    c: InternalAlignment(g4,g3)
    c: InternalAlignment(g5,g3)
    c: Block(g3)
    c: Coincident(g6,g0)
    c: Coincident(g6,g3)
    c: Horizontal(g6)
FEATURE [Part::Extrusion] Extrude012  label="caseScrewPillarBracket"
  Base = -> Sketch018
  Dir = (0,0,1)
  DirMode = 2
  FaceMakerClass = Part::FaceMakerBullseye
  LengthFwd = 2.4
  LengthRev = 0
  Placement = pos=(15.76,29,8.8) rot=(0,1,0;0rad)
  Solid = true
  Symmetric = false
FEATURE [Sketcher::SketchObject] Sketch019
  FullyConstrained = true
  sketch-geometry (7):
    g0: LineSegment StartX=0 StartY=0 StartZ=0 EndX=0 EndY=6 EndZ=0
    g1: Circle CenterX=0 CenterY=0 CenterZ=0 NormalX=0 NormalY=0 NormalZ=1 AngleXU=0 Radius=1
    g2: Circle CenterX=8 CenterY=6 CenterZ=0 NormalX=0 NormalY=0 NormalZ=1 AngleXU=0 Radius=1
    g3: BSplineCurve PolesCount=3 KnotsCount=2 Degree=2 IsPeriodic=0
    g4: GeomPoint X=0 Y=0 Z=0
    g5: GeomPoint X=8 Y=6 Z=0
    g6: LineSegment StartX=0 StartY=6 StartZ=0 EndX=8 EndY=6 EndZ=0
  constraints (14):
    c: Coincident(g0,g-1)
    c: Distance(g0) = 6
    c: Vertical(g0)
    c: Coincident(g3,g0)
    c: Weight(g1) = 1
    c: Equal(g1,g2)
    c: InternalAlignment(g1,g3)
    c: InternalAlignment(g2,g3)
    c: InternalAlignment(g4,g3)
    c: InternalAlignment(g5,g3)
    c: Block(g3)
    c: Coincident(g6,g0)
    c: Coincident(g6,g3)
    c: Horizontal(g6)
FEATURE [Part::Extrusion] Extrude013  label="caseScrewPillarBracket001"
  Base = -> Sketch019
  Dir = (0,0,1)
  DirMode = 2
  FaceMakerClass = Part::FaceMakerBullseye
  LengthFwd = 2.4
  LengthRev = 0
  Placement = pos=(15.76,29,60.8) rot=(0,0,1;0rad)
  Solid = true
  Symmetric = false
FEATURE [Sketcher::SketchObject] Sketch020
  FullyConstrained = true
  sketch-geometry (7):
    g0: LineSegment StartX=0 StartY=0 StartZ=0 EndX=0 EndY=6 EndZ=0
    g1: Circle CenterX=0 CenterY=0 CenterZ=0 NormalX=0 NormalY=0 NormalZ=1 AngleXU=0 Radius=1
    g2: Circle CenterX=8 CenterY=6 CenterZ=0 NormalX=0 NormalY=0 NormalZ=1 AngleXU=0 Radius=1
    g3: BSplineCurve PolesCount=3 KnotsCount=2 Degree=2 IsPeriodic=0
    g4: GeomPoint X=0 Y=0 Z=0
    g5: GeomPoint X=8 Y=6 Z=0
    g6: LineSegment StartX=0 StartY=6 StartZ=0 EndX=8 EndY=6 EndZ=0
  constraints (14):
    c: Coincident(g0,g-1)
    c: Distance(g0) = 6
    c: Vertical(g0)
    c: Coincident(g3,g0)
    c: Weight(g1) = 1
    c: Equal(g1,g2)
    c: InternalAlignment(g1,g3)
    c: InternalAlignment(g2,g3)
    c: InternalAlignment(g4,g3)
    c: InternalAlignment(g5,g3)
    c: Block(g3)
    c: Coincident(g6,g0)
    c: Coincident(g6,g3)
    c: Horizontal(g6)
FEATURE [Part::Extrusion] Extrude014  label="caseScrewPillarBracket002"
  Base = -> Sketch020
  Dir = (0,0,1)
  DirMode = 2
  FaceMakerClass = Part::FaceMakerBullseye
  LengthFwd = 2.4
  LengthRev = 0
  Placement = pos=(13.7,29,13.26) rot=(0,-1,0;1.5708rad)
  Solid = true
  Symmetric = false
FEATURE [Sketcher::SketchObject] Sketch021
  FullyConstrained = true
  sketch-geometry (7):
    g0: LineSegment StartX=0 StartY=0 StartZ=0 EndX=0 EndY=6 EndZ=0
    g1: Circle CenterX=0 CenterY=0 CenterZ=0 NormalX=0 NormalY=0 NormalZ=1 AngleXU=0 Radius=1
    g2: Circle CenterX=8 CenterY=6 CenterZ=0 NormalX=0 NormalY=0 NormalZ=1 AngleXU=0 Radius=1
    g3: BSplineCurve PolesCount=3 KnotsCount=2 Degree=2 IsPeriodic=0
    g4: GeomPoint X=0 Y=0 Z=0
    g5: GeomPoint X=8 Y=6 Z=0
    g6: LineSegment StartX=0 StartY=6 StartZ=0 EndX=8 EndY=6 EndZ=0
  constraints (14):
    c: Coincident(g0,g-1)
    c: Distance(g0) = 6
    c: Vertical(g0)
    c: Coincident(g3,g0)
    c: Weight(g1) = 1
    c: Equal(g1,g2)
    c: InternalAlignment(g1,g3)
    c: InternalAlignment(g2,g3)
    c: InternalAlignment(g4,g3)
    c: InternalAlignment(g5,g3)
    c: Block(g3)
    c: Coincident(g6,g0)
    c: Coincident(g6,g3)
    c: Horizontal(g6)
FEATURE [Part::Extrusion] Extrude015  label="caseScrewPillarBracket003"
  Base = -> Sketch021
  Dir = (0,0,1)
  DirMode = 2
  FaceMakerClass = Part::FaceMakerBullseye
  LengthFwd = 2.4
  LengthRev = 0
  Placement = pos=(11.3,29,58.74) rot=(0,1,0;1.5708rad)
  Solid = true
  Symmetric = false
FEATURE [Sketcher::SketchObject] Sketch022
  FullyConstrained = true
  sketch-geometry (7):
    g0: LineSegment StartX=0 StartY=0 StartZ=0 EndX=0 EndY=6 EndZ=0
    g1: Circle CenterX=0 CenterY=0 CenterZ=0 NormalX=0 NormalY=0 NormalZ=1 AngleXU=0 Radius=1
    g2: Circle CenterX=8 CenterY=6 CenterZ=0 NormalX=0 NormalY=0 NormalZ=1 AngleXU=0 Radius=1
    g3: BSplineCurve PolesCount=3 KnotsCount=2 Degree=2 IsPeriodic=0
    g4: GeomPoint X=0 Y=0 Z=0
    g5: GeomPoint X=8 Y=6 Z=0
    g6: LineSegment StartX=0 StartY=6 StartZ=0 EndX=8 EndY=6 EndZ=0
  constraints (14):
    c: Coincident(g0,g-1)
    c: Distance(g0) = 6
    c: Vertical(g0)
    c: Coincident(g3,g0)
    c: Weight(g1) = 1
    c: Equal(g1,g2)
    c: InternalAlignment(g1,g3)
    c: InternalAlignment(g2,g3)
    c: InternalAlignment(g4,g3)
    c: InternalAlignment(g5,g3)
    c: Block(g3)
    c: Coincident(g6,g0)
    c: Coincident(g6,g3)
    c: Horizontal(g6)
FEATURE [Part::Extrusion] Extrude016  label="caseScrewPillarBracket004"
  Base = -> Sketch022
  Dir = (0,0,1)
  DirMode = 2
  FaceMakerClass = Part::FaceMakerBullseye
  LengthFwd = 2.4
  LengthRev = 0
  Placement = pos=(88.3,29,65.23) rot=(0,1,0;1.5708rad)
  Solid = true
  Symmetric = false
FEATURE [Sketcher::SketchObject] Sketch023
  FullyConstrained = true
  sketch-geometry (7):
    g0: LineSegment StartX=0 StartY=0 StartZ=0 EndX=0 EndY=6 EndZ=0
    g1: Circle CenterX=0 CenterY=0 CenterZ=0 NormalX=0 NormalY=0 NormalZ=1 AngleXU=0 Radius=1
    g2: Circle CenterX=8 CenterY=6 CenterZ=0 NormalX=0 NormalY=0 NormalZ=1 AngleXU=0 Radius=1
    g3: BSplineCurve PolesCount=3 KnotsCount=2 Degree=2 IsPeriodic=0
    g4: GeomPoint X=0 Y=0 Z=0
    g5: GeomPoint X=8 Y=6 Z=0
    g6: LineSegment StartX=0 StartY=6 StartZ=0 EndX=8 EndY=6 EndZ=0
  constraints (14):
    c: Coincident(g0,g-1)
    c: Distance(g0) = 6
    c: Vertical(g0)
    c: Coincident(g3,g0)
    c: Weight(g1) = 1
    c: Equal(g1,g2)
    c: InternalAlignment(g1,g3)
    c: InternalAlignment(g2,g3)
    c: InternalAlignment(g4,g3)
    c: InternalAlignment(g5,g3)
    c: Block(g3)
    c: Coincident(g6,g0)
    c: Coincident(g6,g3)
    c: Horizontal(g6)
FEATURE [Part::Extrusion] Extrude017  label="caseScrewPillarBracket005"
  Base = -> Sketch023
  Dir = (0,0,1)
  DirMode = 2
  FaceMakerClass = Part::FaceMakerBullseye
  LengthFwd = 2.4
  LengthRev = 0
  Placement = pos=(90.7,29,6.77) rot=(0,-1,0;1.5708rad)
  Solid = true
  Symmetric = false
FEATURE [Sketcher::SketchObject] Sketch024
  FullyConstrained = true
  sketch-geometry (7):
    g0: LineSegment StartX=0 StartY=0 StartZ=0 EndX=0 EndY=6 EndZ=0
    g1: Circle CenterX=0 CenterY=0 CenterZ=0 NormalX=0 NormalY=0 NormalZ=1 AngleXU=0 Radius=1
    g2: Circle CenterX=8 CenterY=6 CenterZ=0 NormalX=0 NormalY=0 NormalZ=1 AngleXU=0 Radius=1
    g3: BSplineCurve PolesCount=3 KnotsCount=2 Degree=2 IsPeriodic=0
    g4: GeomPoint X=0 Y=0 Z=0
    g5: GeomPoint X=8 Y=6 Z=0
    g6: LineSegment StartX=0 StartY=6 StartZ=0 EndX=8 EndY=6 EndZ=0
  constraints (14):
    c: Coincident(g0,g-1)
    c: Distance(g0) = 6
    c: Vertical(g0)
    c: Coincident(g3,g0)
    c: Weight(g1) = 1
    c: Equal(g1,g2)
    c: InternalAlignment(g1,g3)
    c: InternalAlignment(g2,g3)
    c: InternalAlignment(g4,g3)
    c: InternalAlignment(g5,g3)
    c: Block(g3)
    c: Coincident(g6,g0)
    c: Coincident(g6,g3)
    c: Horizontal(g6)
FEATURE [Part::Extrusion] Extrude018  label="caseScrewPillarBracket006"
  Base = -> Sketch024
  Dir = (0,0,1)
  DirMode = 2
  FaceMakerClass = Part::FaceMakerBullseye
  LengthFwd = 2.4
  LengthRev = 0
  Placement = pos=(103.7,29,6.77) rot=(0,-1,0;1.5708rad)
  Solid = true
  Symmetric = false
FEATURE [Sketcher::SketchObject] Sketch025
  FullyConstrained = true
  sketch-geometry (7):
    g0: LineSegment StartX=0 StartY=0 StartZ=0 EndX=0 EndY=6 EndZ=0
    g1: Circle CenterX=0 CenterY=0 CenterZ=0 NormalX=0 NormalY=0 NormalZ=1 AngleXU=0 Radius=1
    g2: Circle CenterX=8 CenterY=6 CenterZ=0 NormalX=0 NormalY=0 NormalZ=1 AngleXU=0 Radius=1
    g3: BSplineCurve PolesCount=3 KnotsCount=2 Degree=2 IsPeriodic=0
    g4: GeomPoint X=0 Y=0 Z=0
    g5: GeomPoint X=8 Y=6 Z=0
    g6: LineSegment StartX=0 StartY=6 StartZ=0 EndX=8 EndY=6 EndZ=0
  constraints (14):
    c: Coincident(g0,g-1)
    c: Distance(g0) = 6
    c: Vertical(g0)
    c: Coincident(g3,g0)
    c: Weight(g1) = 1
    c: Equal(g1,g2)
    c: InternalAlignment(g1,g3)
    c: InternalAlignment(g2,g3)
    c: InternalAlignment(g4,g3)
    c: InternalAlignment(g5,g3)
    c: Block(g3)
    c: Coincident(g6,g0)
    c: Coincident(g6,g3)
    c: Horizontal(g6)
FEATURE [Part::Extrusion] Extrude019  label="caseScrewPillarBracket007"
  Base = -> Sketch025
  Dir = (0,0,1)
  DirMode = 2
  FaceMakerClass = Part::FaceMakerBullseye
  LengthFwd = 2.4
  LengthRev = 0
  Placement = pos=(101.3,29,65.23) rot=(0,1,0;1.5708rad)
  Solid = true
  Symmetric = false
FEATURE [Part::Box] Box011  label="frontCaseScrewPillarBracket"
  AttacherType = Attacher::AttachEngine3D
  Height = 2.4
  Length = 16
  Placement = pos=(87,28,2.3) rot=(0,0,1;0rad)
  Width = 7
FEATURE [Part::Box] Box012  label="frontCaseScrewPillarBracket001"
  AttacherType = Attacher::AttachEngine3D
  Height = 2.4
  Length = 16
  Placement = pos=(87,28,67.3) rot=(0,0,1;0rad)
  Width = 7
FEATURE [Sketcher::SketchObject] Sketch026
  FullyConstrained = true
  sketch-geometry (17):
    g0: Circle CenterX=-3.5 CenterY=23.5 CenterZ=0 NormalX=0 NormalY=0 NormalZ=1 AngleXU=0 Radius=1
    g1: Circle CenterX=-1 CenterY=15.25 CenterZ=0 NormalX=0 NormalY=0 NormalZ=1 AngleXU=0 Radius=1
    g2: Circle CenterX=-3.5 CenterY=7 CenterZ=0 NormalX=0 NormalY=0 NormalZ=1 AngleXU=0 Radius=1
    g3: BSplineCurve PolesCount=3 KnotsCount=2 Degree=2 IsPeriodic=0
    g4: GeomPoint X=-3.5 Y=23.5 Z=0
    g5: GeomPoint X=-3.5 Y=7 Z=0
    g6: Circle CenterX=-4.8 CenterY=30.5 CenterZ=0 NormalX=0 NormalY=0 NormalZ=1 AngleXU=0 Radius=1
    g7: Circle CenterX=-3.5 CenterY=30.5 CenterZ=0 NormalX=0 NormalY=0 NormalZ=1 AngleXU=0 Radius=1
    g8: Circle CenterX=-3.5 CenterY=29.2 CenterZ=0 NormalX=0 NormalY=0 NormalZ=1 AngleXU=0 Radius=1
    g9: BSplineCurve PolesCount=3 KnotsCount=2 Degree=2 IsPeriodic=0
    g10: GeomPoint X=-4.8 Y=30.5 Z=0
    g11: GeomPoint X=-3.5 Y=29.2 Z=0
    g12: LineSegment StartX=-3.5 StartY=29.2 StartZ=0 EndX=-3.5 EndY=23.5 EndZ=0
    g13: LineSegment StartX=-4.8 StartY=30.5 StartZ=0 EndX=0 EndY=30.5 EndZ=0
    g14: LineSegment StartX=-3.5 StartY=5 StartZ=0 EndX=-3.5 EndY=7 EndZ=0
    g15: LineSegment StartX=0 StartY=5 StartZ=0 EndX=0 EndY=30.5 EndZ=0
    g16: LineSegment StartX=-3.5 StartY=5 StartZ=0 EndX=0 EndY=5 EndZ=0
  constraints (33):
    c: Weight(g0) = 1
    c: Equal(g0,g1)
    c: Equal(g0,g2)
    c: InternalAlignment(g0,g3)
    c: InternalAlignment(g1,g3)
    c: InternalAlignment(g2,g3)
    c: InternalAlignment(g4,g3)
    c: InternalAlignment(g5,g3)
    c: Block(g3)
    c: Weight(g6) = 1
    c: Equal(g6,g7)
    c: Equal(g6,g8)
    c: InternalAlignment(g6,g9)
    c: InternalAlignment(g7,g9)
    c: InternalAlignment(g8,g9)
    c: InternalAlignment(g10,g9)
    c: InternalAlignment(g11,g9)
    c: Block(g9)
    c: Coincident(g12,g9)
    c: Coincident(g12,g3)
    c: Vertical(g12)
    c: Coincident(g13,g9)
    c: Horizontal(g13)
    c: Distance(g13) = 4.8
    c: Coincident(g14,g3)
    c: Vertical(g14)
    c: Coincident(g15,g13)
    c: Vertical(g15)
    c: Tangent(g15,g1)
    c: Distance(g14) = 2
    c: Coincident(g16,g14)
    c: Horizontal(g16)
    c: Coincident(g15,g16)
FEATURE [Part::Feature] Face050
  shape: bbox 4.8 x 25.5 x 2e-07 mm, 1 faces, 0 solids (baked)
FEATURE [Part::Revolution] Revolve054  label="moreFrontCaseScrewPost001"
  Angle = 360
  Axis = (0,1,0)
  Base = (0,0,0)
  FaceMakerClass = Part::FaceMakerBullseye
  Placement = pos=(102.5,4.5,3.5) rot=(0,0,1;0rad)
  Solid = false
  Source = -> Face050
  Symmetric = false
FEATURE [Part::Feature] Face051
  shape: bbox 4.8 x 25.5 x 2e-07 mm, 1 faces, 0 solids (baked)
FEATURE [Part::Revolution] Revolve055  label="moreFrontCaseScrewPost002"
  Angle = 360
  Axis = (0,1,0)
  Base = (0,0,0)
  FaceMakerClass = Part::FaceMakerBullseye
  Placement = pos=(102.5,4.5,68.5) rot=(0,0,1;0rad)
  Solid = false
  Source = -> Face051
  Symmetric = false
FEATURE [Sketcher::SketchObject] Sketch027
  FullyConstrained = true
  sketch-geometry (10):
    g0: LineSegment StartX=-1.6 StartY=4.7 StartZ=0 EndX=-1.6 EndY=1.7 EndZ=0
    g1: LineSegment StartX=-3.5 StartY=4.7 StartZ=0 EndX=-1.6 EndY=4.7 EndZ=0
    g2: LineSegment StartX=-1.6 StartY=1.7 StartZ=0 EndX=-1.6 EndY=1.5 EndZ=0
    g3: LineSegment StartX=-1.6 StartY=1.5 StartZ=0 EndX=-5.2 EndY=1.5 EndZ=0
    g4: Circle CenterX=-3.5 CenterY=4.7 CenterZ=0 NormalX=0 NormalY=0 NormalZ=1 AngleXU=0 Radius=1
    g5: Circle CenterX=-3.59627 CenterY=2.99743 CenterZ=0 NormalX=0 NormalY=0 NormalZ=1 AngleXU=0 Radius=1
    g6: Circle CenterX=-5.2 CenterY=1.5 CenterZ=0 NormalX=0 NormalY=0 NormalZ=1 AngleXU=0 Radius=1
    g7: BSplineCurve PolesCount=3 KnotsCount=2 Degree=2 IsPeriodic=0
    g8: GeomPoint X=-3.5 Y=4.7 Z=0
    g9: GeomPoint X=-5.2 Y=1.5 Z=0
  constraints (23):
    c: Vertical(g0)
    c: Distance(g0) = 3
    c: Coincident(g1,g0)
    c: Horizontal(g1)
    c: Block(g0)
    c: Block(g1)
    c: Coincident(g2,g0)
    c: Vertical(g2)
    c: Distance(g2) = 0.2
    c: Coincident(g3,g2)
    c: Horizontal(g3)
    c: Block(g3)
    c: Coincident(g7,g1)
    c: Weight(g4) = 1
    c: Equal(g4,g5)
    c: Equal(g4,g6)
    c: Coincident(g7,g3)
    c: InternalAlignment(g4,g7)
    c: InternalAlignment(g5,g7)
    c: InternalAlignment(g6,g7)
    c: InternalAlignment(g8,g7)
    c: InternalAlignment(g9,g7)
    c: Block(g7)
FEATURE [Sketcher::SketchObject] Sketch028
  FullyConstrained = true
  sketch-geometry (18):
    g0: LineSegment StartX=0 StartY=3e-16 StartZ=0 EndX=0 EndY=1.7 EndZ=0
    g1: LineSegment StartX=-3.5 StartY=0 StartZ=0 EndX=-3.5 EndY=0.9 EndZ=0
    g2: Circle CenterX=-2.7 CenterY=1.7 CenterZ=0 NormalX=0 NormalY=0 NormalZ=1 AngleXU=0 Radius=1
    g3: Circle CenterX=-3.5 CenterY=1.7 CenterZ=0 NormalX=0 NormalY=0 NormalZ=1 AngleXU=0 Radius=1
    g4: Circle CenterX=-3.5 CenterY=0.9 CenterZ=0 NormalX=0 NormalY=0 NormalZ=1 AngleXU=0 Radius=1
    g5: BSplineCurve PolesCount=3 KnotsCount=2 Degree=2 IsPeriodic=0
    g6: GeomPoint X=-2.7 Y=1.7 Z=0
    g7: GeomPoint X=-3.5 Y=0.9 Z=0
    g8: LineSegment StartX=-3.5 StartY=0 StartZ=0 EndX=-3.5 EndY=-7 EndZ=0
    g9: LineSegment StartX=0 StartY=3e-16 StartZ=0 EndX=0 EndY=-7 EndZ=0
    g10: LineSegment StartX=-3.5 StartY=-7 StartZ=0 EndX=0 EndY=-7 EndZ=0
    g11: LineSegment StartX=-2.7 StartY=1.7 StartZ=0 EndX=-1.6 EndY=1.7 EndZ=0
    g12: LineSegment StartX=0 StartY=1.7 StartZ=0 EndX=0 EndY=4.5 EndZ=0
    g13: LineSegment StartX=0 StartY=4.5 StartZ=0 EndX=0 EndY=10.8 EndZ=0
    g14: LineSegment StartX=0 StartY=10.8 StartZ=0 EndX=-2 EndY=10.8 EndZ=0
    g15: LineSegment StartX=-1.6 StartY=4.7 StartZ=0 EndX=-1.6 EndY=1.7 EndZ=0
    g16: LineSegment StartX=-1.6 StartY=4.7 StartZ=0 EndX=-2 EndY=4.7 EndZ=0
    g17: LineSegment StartX=-2 StartY=4.7 StartZ=0 EndX=-2 EndY=10.8 EndZ=0
  constraints (44):
    c: Vertical(g0)
    c: Vertical(g1)
    c: Distance(g1) = 0.9
    c: Block(g0)
    c: Distance(g0) = 1.7
    c: Weight(g2) = 1
    c: Equal(g2,g3)
    c: Equal(g2,g4)
    c: Coincident(g5,g1)
    c: InternalAlignment(g2,g5)
    c: InternalAlignment(g3,g5)
    c: InternalAlignment(g4,g5)
    c: InternalAlignment(g6,g5)
    c: InternalAlignment(g7,g5)
    c: Block(g5)
    c: Coincident(g8,g1)
    c: Vertical(g8)
    c: Distance(g8) = 7
    c: Vertical(g9)
    c: Equal(g8,g9) = 7
    c: Coincident(g9,g0)
    c: Coincident(g10,g8)
    c: Coincident(g10,g9)
    c: Horizontal(g10)
    c: Coincident(g11,g5)
    c: Horizontal(g11)
    c: Coincident(g12,g0)
    c: Vertical(g12)
    c: Distance(g12) = 2.8
    c: Coincident(g13,g12)
    c: Vertical(g13)
    c: Distance(g13) = 6.3
    c: Coincident(g14,g13)
    c: Horizontal(g14)
    c: Distance(g14) = 2
    c: Vertical(g15)
    c: Distance(g15) = 3
    c: Block(g11)
    c: Coincident(g15,g11)
    c: Coincident(g16,g15)
    c: Horizontal(g16)
    c: Coincident(g17,g16)
    c: Coincident(g17,g14)
    c: Vertical(g17)
FEATURE [Part::Revolution] Revolve040  label="backCaseScrewRetainer001"
  Angle = 360
  Axis = (0,1,0)
  Base = (0,0,0)
  FaceMakerClass = Part::FaceMakerBullseye
  Placement = pos=(12.5,3,10) rot=(0,0,1;0rad)
  Solid = false
  Source = -> Face036
  Symmetric = false
FEATURE [Part::Feature] Face055
  shape: bbox 3.5 x 30.2 x 2e-07 mm, 1 faces, 0 solids (baked)
FEATURE [Part::Revolution] Revolve059  label="backCaseScrewPost"
  Angle = 360
  Axis = (0,1,0)
  Base = (0,0,0)
  FaceMakerClass = Part::FaceMakerBullseye
  Placement = pos=(12.5,4.5,10) rot=(0,0,1;0rad)
  Solid = false
  Source = -> Face055
  Symmetric = false
FEATURE [Part::Feature] Face056
  shape: bbox 3.5 x 30.2 x 2e-07 mm, 1 faces, 0 solids (baked)
FEATURE [Part::Revolution] Revolve060  label="backCaseScrewPost001"
  Angle = 360
  Axis = (0,1,0)
  Base = (0,0,0)
  FaceMakerClass = Part::FaceMakerBullseye
  Placement = pos=(12.5,4.5,62) rot=(0,0,1;0rad)
  Solid = false
  Source = -> Face056
  Symmetric = false
FEATURE [Part::Feature] Face057
  shape: bbox 3.5 x 17.8 x 2e-07 mm, 1 faces, 0 solids (baked)
FEATURE [Part::Revolution] Revolve061  label="removeToCreateScrewAndThreadedInsertHole"
  Angle = 360
  Axis = (0,1,0)
  Base = (0,0,0)
  FaceMakerClass = Part::FaceMakerBullseye
  Placement = pos=(12.5,0,10) rot=(0,0,1;0rad)
  Solid = false
  Source = -> Face057
  Symmetric = false
FEATURE [Part::Feature] Face058
  shape: bbox 3.5 x 17.8 x 2e-07 mm, 1 faces, 0 solids (baked)
FEATURE [Part::Revolution] Revolve062  label="removeToCreateScrewAndThreadedInsertHole001"
  Angle = 360
  Axis = (0,1,0)
  Base = (0,0,0)
  FaceMakerClass = Part::FaceMakerBullseye
  Placement = pos=(12.5,0,62) rot=(0,0,1;0rad)
  Solid = false
  Source = -> Face058
  Symmetric = false
FEATURE [Part::Feature] Face059
  shape: bbox 3.5 x 17.8 x 2e-07 mm, 1 faces, 0 solids (baked)
FEATURE [Part::Revolution] Revolve063  label="removeToCreateScrewAndThreadedInsertHole002"
  Angle = 360
  Axis = (0,1,0)
  Base = (0,0,0)
  FaceMakerClass = Part::FaceMakerBullseye
  Placement = pos=(89.5,0,68.5) rot=(0,0,1;0rad)
  Solid = false
  Source = -> Face059
  Symmetric = false
FEATURE [Part::Feature] Face060
  shape: bbox 3.5 x 17.8 x 2e-07 mm, 1 faces, 0 solids (baked)
FEATURE [Part::Revolution] Revolve064  label="removeToCreateScrewAndThreadedInsertHole003"
  Angle = 360
  Axis = (0,1,0)
  Base = (0,0,0)
  FaceMakerClass = Part::FaceMakerBullseye
  Placement = pos=(89.5,0,3.5) rot=(0,0,1;0rad)
  Solid = false
  Source = -> Face060
  Symmetric = false
FEATURE [Part::Feature] Face061
  shape: bbox 3.5 x 17.8 x 2e-07 mm, 1 faces, 0 solids (baked)
FEATURE [Part::Revolution] Revolve065  label="removeToCreateScrewAndThreadedInsertHole004"
  Angle = 360
  Axis = (0,1,0)
  Base = (0,0,0)
  FaceMakerClass = Part::FaceMakerBullseye
  Placement = pos=(102.5,4.7,3.5) rot=(0,0,1;0rad)
  Solid = false
  Source = -> Face061
  Symmetric = false
FEATURE [Part::Feature] Face062
  shape: bbox 3.5 x 17.8 x 2e-07 mm, 1 faces, 0 solids (baked)
FEATURE [Part::Revolution] Revolve066  label="removeToCreateScrewAndThreadedInsertHole005"
  Angle = 360
  Axis = (0,1,0)
  Base = (0,0,0)
  FaceMakerClass = Part::FaceMakerBullseye
  Placement = pos=(102.5,4.7,68.5) rot=(0,0,1;0rad)
  Solid = false
  Source = -> Face062
  Symmetric = false
FEATURE [Part::MultiFuse] Fusion047  label="makeHoles"
  Shapes = -> [Revolve066,Revolve065,Revolve064,Revolve063,Revolve062,Revolve061]
FEATURE [Part::Feature] Face063
  shape: bbox 3.6 x 3.2 x 2e-07 mm, 1 faces, 0 solids (baked)
FEATURE [Part::Revolution] Revolve067  label="moreFrontCaseScrewRetainer002"
  Angle = 360
  Axis = (0,1,0)
  Base = (0,0,0)
  FaceMakerClass = Part::FaceMakerBullseye
  Placement = pos=(102.5,4.5,68.5) rot=(0,0,1;0rad)
  Solid = false
  Source = -> Face063
  Symmetric = false
FEATURE [Part::Feature] Face064
  shape: bbox 3.6 x 3.2 x 2e-07 mm, 1 faces, 0 solids (baked)
FEATURE [Part::Revolution] Revolve068  label="moreFrontCaseScrewRetainer003"
  Angle = 360
  Axis = (0,1,0)
  Base = (0,0,0)
  FaceMakerClass = Part::FaceMakerBullseye
  Placement = pos=(102.5,4.5,3.5) rot=(0,0,1;0rad)
  Solid = false
  Source = -> Face064
  Symmetric = false
FEATURE [Part::Feature] Face065
  shape: bbox 3.5 x 17.8 x 2e-07 mm, 1 faces, 0 solids (baked)
FEATURE [Part::Revolution] Revolve069  label="removeToCreateScrewAndThreadedInsertHole006"
  Angle = 360
  Axis = (0,1,0)
  Base = (0,0,0)
  FaceMakerClass = Part::FaceMakerBullseye
  Placement = pos=(12.5,0,10) rot=(0,0,1;0rad)
  Solid = false
  Source = -> Face065
  Symmetric = false
FEATURE [Part::Feature] Face066
  shape: bbox 3.5 x 17.8 x 2e-07 mm, 1 faces, 0 solids (baked)
FEATURE [Part::Revolution] Revolve070  label="removeToCreateScrewAndThreadedInsertHole007"
  Angle = 360
  Axis = (0,1,0)
  Base = (0,0,0)
  FaceMakerClass = Part::FaceMakerBullseye
  Placement = pos=(12.5,0,62) rot=(0,0,1;0rad)
  Solid = false
  Source = -> Face066
  Symmetric = false
FEATURE [Part::Feature] Face067
  shape: bbox 3.5 x 17.8 x 2e-07 mm, 1 faces, 0 solids (baked)
FEATURE [Part::Revolution] Revolve071  label="removeToCreateScrewAndThreadedInsertHole008"
  Angle = 360
  Axis = (0,1,0)
  Base = (0,0,0)
  FaceMakerClass = Part::FaceMakerBullseye
  Placement = pos=(89.5,0,68.5) rot=(0,0,1;0rad)
  Solid = false
  Source = -> Face067
  Symmetric = false
FEATURE [Part::Feature] Face068
  shape: bbox 3.5 x 17.8 x 2e-07 mm, 1 faces, 0 solids (baked)
FEATURE [Part::Revolution] Revolve072  label="removeToCreateScrewAndThreadedInsertHole009"
  Angle = 360
  Axis = (0,1,0)
  Base = (0,0,0)
  FaceMakerClass = Part::FaceMakerBullseye
  Placement = pos=(89.5,0,3.5) rot=(0,0,1;0rad)
  Solid = false
  Source = -> Face068
  Symmetric = false
FEATURE [Part::Feature] Face069
  shape: bbox 3.5 x 17.8 x 2e-07 mm, 1 faces, 0 solids (baked)
FEATURE [Part::Feature] Face070
  shape: bbox 3.5 x 17.8 x 2e-07 mm, 1 faces, 0 solids (baked)
FEATURE [Part::Revolution] Revolve073  label="removeToCreateScrewAndThreadedInsertHole010"
  Angle = 360
  Axis = (0,1,0)
  Base = (0,0,0)
  FaceMakerClass = Part::FaceMakerBullseye
  Placement = pos=(102.5,4.7,3.5) rot=(0,0,1;0rad)
  Solid = false
  Source = -> Face069
  Symmetric = false
FEATURE [Part::Revolution] Revolve074  label="removeToCreateScrewAndThreadedInsertHole011"
  Angle = 360
  Axis = (0,1,0)
  Base = (0,0,0)
  FaceMakerClass = Part::FaceMakerBullseye
  Placement = pos=(102.5,4.7,68.5) rot=(0,0,1;0rad)
  Solid = false
  Source = -> Face070
  Symmetric = false
FEATURE [Part::MultiFuse] Fusion048  label="makeHoles001"
  Shapes = -> [Revolve074,Revolve073,Revolve072,Revolve071,Revolve070,Revolve069]
FEATURE [Part::MultiFuse] Fusion049  label="caseScrewRetainers"
  Shapes = -> [Revolve067,Revolve068,Revolve048,Revolve047,Revolve039,Revolve040]
FEATURE [Part::Cut] Cut015  label="caseScrewRetainers001"
  Base = -> Fusion049
  Tool = -> Fusion048
FEATURE [Part::MultiFuse] Fusion050  label="casePillars"
  Shapes = -> [Revolve055,Revolve054,Revolve043,Revolve046,Revolve059,Revolve060]
FEATURE [Part::Feature] Face071 .. Face076  x6 (patterned run collapsed; names and placements below)
  shape: bbox 3.5 x 17.8 x 2e-07 mm, 1 faces, 0 solids (baked)
FEATURE [Part::Revolution] Revolve075  label="removeToCreateScrewAndThreadedInsertHole012"
  Angle = 360
  Axis = (0,1,0)
  Base = (0,0,0)
  FaceMakerClass = Part::FaceMakerBullseye
  Placement = pos=(12.5,0,10) rot=(0,0,1;0rad)
  Solid = false
  Source = -> Face071
  Symmetric = false
FEATURE [Part::Revolution] Revolve076  label="removeToCreateScrewAndThreadedInsertHole013"
  Angle = 360
  Axis = (0,1,0)
  Base = (0,0,0)
  FaceMakerClass = Part::FaceMakerBullseye
  Placement = pos=(12.5,0,62) rot=(0,0,1;0rad)
  Solid = false
  Source = -> Face072
  Symmetric = false
FEATURE [Part::Revolution] Revolve077  label="removeToCreateScrewAndThreadedInsertHole014"
  Angle = 360
  Axis = (0,1,0)
  Base = (0,0,0)
  FaceMakerClass = Part::FaceMakerBullseye
  Placement = pos=(89.5,0,68.5) rot=(0,0,1;0rad)
  Solid = false
  Source = -> Face073
  Symmetric = false
FEATURE [Part::Revolution] Revolve078  label="removeToCreateScrewAndThreadedInsertHole015"
  Angle = 360
  Axis = (0,1,0)
  Base = (0,0,0)
  FaceMakerClass = Part::FaceMakerBullseye
  Placement = pos=(89.5,0,3.5) rot=(0,0,1;0rad)
  Solid = false
  Source = -> Face074
  Symmetric = false
FEATURE [Part::Revolution] Revolve079  label="removeToCreateScrewAndThreadedInsertHole016"
  Angle = 360
  Axis = (0,1,0)
  Base = (0,0,0)
  FaceMakerClass = Part::FaceMakerBullseye
  Placement = pos=(102.5,4.7,3.5) rot=(0,0,1;0rad)
  Solid = false
  Source = -> Face075
  Symmetric = false
FEATURE [Part::Revolution] Revolve080  label="removeToCreateScrewAndThreadedInsertHole017"
  Angle = 360
  Axis = (0,1,0)
  Base = (0,0,0)
  FaceMakerClass = Part::FaceMakerBullseye
  Placement = pos=(102.5,4.7,68.5) rot=(0,0,1;0rad)
  Solid = false
  Source = -> Face076
  Symmetric = false
FEATURE [Part::MultiFuse] Fusion051  label="makeHoles002"
  Shapes = -> [Revolve080,Revolve079,Revolve078,Revolve077,Revolve076,Revolve075]
FEATURE [Part::Cut] Cut016  label="caesPillars"
  Base = -> Fusion050
  Tool = -> Fusion051
FEATURE [Part::Revolution] Revolve009  label="plugHousing016"
  Angle = 360
  Axis = (0,1,0)
  Base = (0,0,0)
  FaceMakerClass = Part::FaceMakerBullseye
  Placement = pos=(0,0,36.15) rot=(0,0,1;0rad)
  Solid = false
  Source = -> Face012
  Symmetric = false
FEATURE [Part::MultiFuse] Fusion014  label="plugHousing023"
  Placement = pos=(0,0,0) rot=(0,0,1;1.5708rad)
  Shapes = -> [Revolve011,Revolve009]
FEATURE [Part::Revolution] Revolve010  label="plugHousing017"
  Angle = 360
  Axis = (0,1,0)
  Base = (0,0,0)
  FaceMakerClass = Part::FaceMakerBullseye
  Placement = pos=(0,0,36.15) rot=(0,0,1;0rad)
  Solid = false
  Source = -> Face014
  Symmetric = false
FEATURE [Part::MultiFuse] Fusion015  label="plugHousing024"
  Placement = pos=(0,0,0) rot=(0,0,1;1.5708rad)
  Shapes = -> [Revolve010,Revolve015]
FEATURE [Part::Revolution] Revolve014  label="plugHousing026"
  Angle = 360
  Axis = (0,1,0)
  Base = (0,0,0)
  FaceMakerClass = Part::FaceMakerBullseye
  Placement = pos=(0,0,36.15) rot=(0,0,1;0rad)
  Solid = false
  Source = -> Face011
  Symmetric = false
FEATURE [Part::Revolution] Revolve013  label="plugHousing025"
  Angle = 360
  Axis = (0,1,0)
  Base = (0,0,0)
  FaceMakerClass = Part::FaceMakerBullseye
  Placement = pos=(0,0,36.15) rot=(0,0,1;0rad)
  Solid = false
  Source = -> Face015
  Symmetric = false
FEATURE [Part::MultiFuse] Fusion016  label="plugHousing028"
  Placement = pos=(0,19,0) rot=(0,0,1;3.14159rad)
  Shapes = -> [Fusion014,Fusion013]
FEATURE [Part::MultiFuse] Fusion011  label="plugHousing018"
  Placement = pos=(0,0,0) rot=(0,0,1;1.5708rad)
  Shapes = -> [Revolve014,Revolve013]
FEATURE [Part::MultiFuse] Fusion012  label="plugHousing019"
  Placement = pos=(0,19,0) rot=(0,0,1;3.14159rad)
  Shapes = -> [Fusion011,Fusion015]
FEATURE [Part::MultiFuse] Fusion017  label="plugHousing029"
  Placement = pos=(122.621,0,-0.15) rot=(0,0,1;0rad)
  Shapes = -> [Fusion016,Fusion012]
FEATURE [Part::MultiFuse] Fusion052  label="casePillarRetainers"
  Shapes = -> [Extrude012,Extrude013,Extrude014,Extrude015,Extrude016,Extrude017,Extrude018,Extrude019,Box011,Box012]
FEATURE [Part::Feature] Face077
  shape: bbox 3.5 x 17.8 x 2e-07 mm, 1 faces, 0 solids (baked)
FEATURE [Part::Revolution] Revolve081  label="removeToCreateScrewAndThreadedInsertHole018"
  Angle = 360
  Axis = (0,1,0)
  Base = (0,0,0)
  FaceMakerClass = Part::FaceMakerBullseye
  Placement = pos=(62.3,30.3,19.7) rot=(0,0,1;0rad)
  Solid = false
  Source = -> Face077
  Symmetric = false
FEATURE [Part::Feature] Face078
  shape: bbox 3.5 x 17.8 x 2e-07 mm, 1 faces, 0 solids (baked)
FEATURE [Part::Revolution] Revolve082  label="removeToCreateScrewAndThreadedInsertHole019"
  Angle = 360
  Axis = (0,1,0)
  Base = (0,0,0)
  FaceMakerClass = Part::FaceMakerBullseye
  Placement = pos=(62.3,30.3,51.7) rot=(0,0,1;0rad)
  Solid = false
  Source = -> Face078
  Symmetric = false
FEATURE [Part::Feature] Face079
  shape: bbox 3.5 x 17.8 x 2e-07 mm, 1 faces, 0 solids (baked)
FEATURE [Part::Revolution] Revolve083  label="removeToCreateScrewAndThreadedInsertHole020"
  Angle = 360
  Axis = (0,1,0)
  Base = (0,0,0)
  FaceMakerClass = Part::FaceMakerBullseye
  Placement = pos=(30.3,30.3,19.7) rot=(0,0,1;0rad)
  Solid = false
  Source = -> Face079
  Symmetric = false
FEATURE [Part::Feature] Face080
  shape: bbox 3.5 x 17.8 x 2e-07 mm, 1 faces, 0 solids (baked)
FEATURE [Part::Revolution] Revolve084  label="removeToCreateScrewAndThreadedInsertHole021"
  Angle = 360
  Axis = (0,1,0)
  Base = (0,0,0)
  FaceMakerClass = Part::FaceMakerBullseye
  Placement = pos=(30.3,30.3,51.7) rot=(0,0,1;0rad)
  Solid = false
  Source = -> Face080
  Symmetric = false
FEATURE [Part::MultiFuse] Fusion053  label="createThreadedInsertHolesForFan"
  Shapes = -> [Revolve081,Revolve082,Revolve083,Revolve084]
FEATURE [Part::Cut] Cut017  label="fanScrewHousing001"
  Base = -> Fusion046
  Tool = -> Fusion053
FEATURE [Part::Feature] Face081
  shape: bbox 3.5 x 17.8 x 2e-07 mm, 1 faces, 0 solids (baked)
FEATURE [Part::Revolution] Revolve085  label="removeToCreateScrewAndThreadedInsertHole022"
  Angle = 360
  Axis = (0,1,0)
  Base = (0,0,0)
  FaceMakerClass = Part::FaceMakerBullseye
  Placement = pos=(62.3,30.3,19.7) rot=(0,0,1;0rad)
  Solid = false
  Source = -> Face081
  Symmetric = false
FEATURE [Part::Feature] Face082
  shape: bbox 3.5 x 17.8 x 2e-07 mm, 1 faces, 0 solids (baked)
FEATURE [Part::Revolution] Revolve086  label="removeToCreateScrewAndThreadedInsertHole023"
  Angle = 360
  Axis = (0,1,0)
  Base = (0,0,0)
  FaceMakerClass = Part::FaceMakerBullseye
  Placement = pos=(62.3,30.3,51.7) rot=(0,0,1;0rad)
  Solid = false
  Source = -> Face082
  Symmetric = false
FEATURE [Part::Feature] Face083
  shape: bbox 3.5 x 17.8 x 2e-07 mm, 1 faces, 0 solids (baked)
FEATURE [Part::Revolution] Revolve087  label="removeToCreateScrewAndThreadedInsertHole024"
  Angle = 360
  Axis = (0,1,0)
  Base = (0,0,0)
  FaceMakerClass = Part::FaceMakerBullseye
  Placement = pos=(30.3,30.3,19.7) rot=(0,0,1;0rad)
  Solid = false
  Source = -> Face083
  Symmetric = false
FEATURE [Part::Feature] Face084
  shape: bbox 3.5 x 17.8 x 2e-07 mm, 1 faces, 0 solids (baked)
FEATURE [Part::Revolution] Revolve088  label="removeToCreateScrewAndThreadedInsertHole025"
  Angle = 360
  Axis = (0,1,0)
  Base = (0,0,0)
  FaceMakerClass = Part::FaceMakerBullseye
  Placement = pos=(30.3,30.3,51.7) rot=(0,0,1;0rad)
  Solid = false
  Source = -> Face084
  Symmetric = false
FEATURE [Part::MultiFuse] Fusion054  label="createThreadedInsertHolesForFan001"
  Shapes = -> [Revolve085,Revolve086,Revolve087,Revolve088]
FEATURE [Part::Cut] Cut018  label="top007"
  Base = -> Fusion040
  Tool = -> Fusion054
FEATURE [Sketcher::SketchObject] Sketch029
  FullyConstrained = false
  Placement = pos=(0,0,0) rot=(1,0,0;1.5708rad)
  sketch-geometry (24):
    g0: ArcOfCircle CenterX=-4 CenterY=-10.5 CenterZ=0 NormalX=0 NormalY=0 NormalZ=1 AngleXU=0 Radius=1.5 StartAngle=6e-16 EndAngle=3.14159
    g1: ArcOfCircle CenterX=-34.2 CenterY=-10.5 CenterZ=0 NormalX=0 NormalY=0 NormalZ=1 AngleXU=0 Radius=1.5 StartAngle=0 EndAngle=3.14159
    g2: ArcOfCircle CenterX=-34.2 CenterY=-27.7 CenterZ=0 NormalX=0 NormalY=0 NormalZ=1 AngleXU=0 Radius=1.5 StartAngle=3.14159 EndAngle=6.28319
    g3: ArcOfCircle CenterX=-4 CenterY=-27.7 CenterZ=0 NormalX=0 NormalY=0 NormalZ=1 AngleXU=0 Radius=1.5 StartAngle=3.1416 EndAngle=6.28319
    g4: ArcOfCircle CenterX=-10 CenterY=-4.3 CenterZ=0 NormalX=0 NormalY=0 NormalZ=1 AngleXU=0 Radius=1.5 StartAngle=2e-16 EndAngle=3.14159
    g5: ArcOfCircle CenterX=-16.1 CenterY=-1.8 CenterZ=0 NormalX=0 NormalY=0 NormalZ=1 AngleXU=0 Radius=1.5 StartAngle=5e-16 EndAngle=3.14159
    g6: ArcOfCircle CenterX=-22.1 CenterY=-1.8 CenterZ=0 NormalX=0 NormalY=0 NormalZ=1 AngleXU=0 Radius=1.5 StartAngle=5e-16 EndAngle=3.14159
    g7: ArcOfCircle CenterX=-28.2 CenterY=-4.3 CenterZ=0 NormalX=0 NormalY=0 NormalZ=1 AngleXU=0 Radius=1.5 StartAngle=2e-16 EndAngle=3.14159
    g8: ArcOfCircle CenterX=-10 CenterY=-33.9 CenterZ=0 NormalX=0 NormalY=0 NormalZ=1 AngleXU=0 Radius=1.5 StartAngle=3.14159 EndAngle=6.28319
    g9: ArcOfCircle CenterX=-16.1 CenterY=-36.4 CenterZ=0 NormalX=0 NormalY=0 NormalZ=1 AngleXU=0 Radius=1.5 StartAngle=3.14159 EndAngle=6.28319
    g10: ArcOfCircle CenterX=-22.1 CenterY=-36.4 CenterZ=0 NormalX=0 NormalY=0 NormalZ=1 AngleXU=0 Radius=1.5 StartAngle=3.14159 EndAngle=6.28319
    g11: ArcOfCircle CenterX=-28.2 CenterY=-33.9 CenterZ=0 NormalX=0 NormalY=0 NormalZ=1 AngleXU=0 Radius=1.5 StartAngle=3.14159 EndAngle=6.28319
    g12: LineSegment StartX=-35.7 StartY=-10.5 StartZ=0 EndX=-35.7 EndY=-27.7 EndZ=0
    g13: LineSegment StartX=-32.7 StartY=-10.5 StartZ=0 EndX=-32.7 EndY=-27.7 EndZ=0
    g14: LineSegment StartX=-29.7 StartY=-33.9 StartZ=0 EndX=-29.7 EndY=-4.3 EndZ=0
    g15: LineSegment StartX=-26.7 StartY=-33.9 StartZ=0 EndX=-26.7 EndY=-4.3 EndZ=0
    g16: LineSegment StartX=-2.5 StartY=-10.5 StartZ=0 EndX=-2.5 EndY=-27.7 EndZ=0
    g17: LineSegment StartX=-8.5 StartY=-4.3 StartZ=0 EndX=-8.5 EndY=-33.9 EndZ=0
    g18: LineSegment StartX=-5.5 StartY=-10.5 StartZ=0 EndX=-5.5 EndY=-27.7 EndZ=0
    g19: LineSegment StartX=-11.5 StartY=-4.3 StartZ=0 EndX=-11.5 EndY=-33.9 EndZ=0
    g20: LineSegment StartX=-14.6 StartY=-1.8 StartZ=0 EndX=-14.6 EndY=-36.4 EndZ=0
    g21: LineSegment StartX=-17.6 StartY=-1.8 StartZ=0 EndX=-17.6 EndY=-36.4 EndZ=0
    g22: LineSegment StartX=-20.6 StartY=-36.4 StartZ=0 EndX=-20.6 EndY=-1.8 EndZ=0
    g23: LineSegment StartX=-23.6 StartY=-1.8 StartZ=0 EndX=-23.6 EndY=-36.4 EndZ=0
  constraints (48):
    c: Block(g0)
    c: Block(g1)
    c: Block(g2)
    c: Block(g3)
    c: Block(g4)
    c: Block(g5)
    c: Block(g6)
    c: Block(g7)
    c: Block(g8)
    c: Block(g9)
    c: Block(g10)
    c: Block(g11)
    c: Coincident(g12,g1)
    c: Coincident(g12,g2)
    c: Vertical(g12)
    c: Coincident(g13,g1)
    c: Coincident(g13,g2)
    c: Vertical(g13)
    c: Coincident(g14,g11)
    c: Coincident(g14,g7)
    c: Vertical(g14)
    c: Coincident(g15,g11)
    c: Coincident(g15,g7)
    c: Vertical(g15)
    c: Coincident(g16,g0)
    c: Coincident(g16,g3)
    c: Vertical(g16)
    c: Coincident(g17,g4)
    c: Coincident(g17,g8)
    c: Vertical(g17)
    c: Coincident(g18,g0)
    c: Coincident(g18,g3)
    c: Vertical(g18)
    c: Coincident(g19,g4)
    c: Coincident(g19,g8)
    c: Vertical(g19)
    c: Coincident(g20,g5)
    c: Coincident(g20,g9)
    c: Vertical(g20)
    c: Coincident(g21,g5)
    c: Coincident(g21,g9)
    c: Vertical(g21)
    c: Coincident(g22,g10)
    c: Coincident(g22,g6)
    c: Vertical(g22)
    c: Coincident(g23,g6)
    c: Coincident(g23,g10)
    c: Vertical(g23)
FEATURE [Part::Extrusion] Extrude020  label="removeToCreateFanGrillHoles"
  Base = -> Sketch029
  Dir = (0,-1,6e-16)
  DirMode = 2
  FaceMakerClass = Part::FaceMakerBullseye
  LengthFwd = 10
  LengthRev = 0
  Placement = pos=(65.4,44,54.82) rot=(0,0,1;0rad)
  Solid = true
  Symmetric = false
FEATURE [Part::MultiFuse] Fusion055  label="top008"
  Shapes = -> [Cut017,Cut018]
FEATURE [Part::Cut] Cut019  label="top009"
  Base = -> Fusion055
  Tool = -> Extrude020
FEATURE [App::MeasureDistance] Distance003  label="Distance: 71.95 mm"
  Distance = 71.9513
  P1 = (117,38,72)
  P2 = (117,38,0.0487319)
FEATURE [Sketcher::SketchObject] Sketch030
  FullyConstrained = true
  Placement = pos=(117,19,0) rot=(0.57735,0.57735,0.57735;2.0944rad)
  sketch-geometry (48):
    g0: LineSegment StartX=-49.19 StartY=69.25 StartZ=0 EndX=-49.19 EndY=66.25 EndZ=0
    g1: LineSegment StartX=-49.19 StartY=63.5 StartZ=0 EndX=-49.19 EndY=60.5 EndZ=0
    g2: LineSegment StartX=-49.19 StartY=57.75 StartZ=0 EndX=-49.19 EndY=54.75 EndZ=0
    g3: LineSegment StartX=-49.19 StartY=52 StartZ=0 EndX=-49.19 EndY=49 EndZ=0
    g4: LineSegment StartX=-49.19 StartY=46.25 StartZ=0 EndX=-49.19 EndY=43.25 EndZ=0
    g5: LineSegment StartX=-49.19 StartY=40.5 StartZ=0 EndX=-49.19 EndY=37.5 EndZ=0
    g6: LineSegment StartX=-49.19 StartY=34.5 StartZ=0 EndX=-49.19 EndY=31.5 EndZ=0
    g7: LineSegment StartX=-49.19 StartY=28.75 StartZ=0 EndX=-49.19 EndY=25.75 EndZ=0
    g8: LineSegment StartX=-49.19 StartY=23 StartZ=0 EndX=-49.19 EndY=20 EndZ=0
    g9: LineSegment StartX=-49.19 StartY=17.25 StartZ=0 EndX=-49.19 EndY=14.25 EndZ=0
    g10: LineSegment StartX=-49.19 StartY=11.5 StartZ=0 EndX=-49.19 EndY=8.5 EndZ=0
    g11: LineSegment StartX=-49.19 StartY=5.75 StartZ=0 EndX=-49.19 EndY=2.75 EndZ=0
    g12: ArcOfCircle CenterX=-1.5 CenterY=67.75 CenterZ=0 NormalX=0 NormalY=0 NormalZ=1 AngleXU=0 Radius=1.5 StartAngle=4.71239 EndAngle=7.85398
    g13: ArcOfCircle CenterX=-1.5 CenterY=62 CenterZ=0 NormalX=0 NormalY=0 NormalZ=1 AngleXU=0 Radius=1.5 StartAngle=4.71239 EndAngle=7.85398
    g14: ArcOfCircle CenterX=-1.5 CenterY=56.25 CenterZ=0 NormalX=0 NormalY=0 NormalZ=1 AngleXU=0 Radius=1.5 StartAngle=4.71239 EndAngle=7.85398
    g15: ArcOfCircle CenterX=-11.49 CenterY=50.5 CenterZ=0 NormalX=0 NormalY=0 NormalZ=1 AngleXU=0 Radius=1.5 StartAngle=4.71239 EndAngle=7.85398
    g16: ArcOfCircle CenterX=-16.28 CenterY=44.75 CenterZ=0 NormalX=0 NormalY=0 NormalZ=1 AngleXU=0 Radius=1.5 StartAngle=4.71239 EndAngle=7.85398
    g17: ArcOfCircle CenterX=-18.2337 CenterY=39 CenterZ=0 NormalX=0 NormalY=0 NormalZ=1 AngleXU=0 Radius=1.5 StartAngle=4.71485 EndAngle=7.85398
    g18: ArcOfCircle CenterX=-16.2837 CenterY=27.25 CenterZ=0 NormalX=0 NormalY=0 NormalZ=1 AngleXU=0 Radius=1.5 StartAngle=4.71485 EndAngle=7.85398
    g19: ArcOfCircle CenterX=-18.2337 CenterY=33 CenterZ=0 NormalX=0 NormalY=0 NormalZ=1 AngleXU=0 Radius=1.5 StartAngle=4.71485 EndAngle=7.85398
    g20: ArcOfCircle CenterX=-11.49 CenterY=21.5 CenterZ=0 NormalX=0 NormalY=0 NormalZ=1 AngleXU=0 Radius=1.5 StartAngle=4.71239 EndAngle=7.85398
    g21: ArcOfCircle CenterX=-1.5 CenterY=4.25 CenterZ=0 NormalX=0 NormalY=0 NormalZ=1 AngleXU=0 Radius=1.5 StartAngle=4.71239 EndAngle=7.85398
    g22: ArcOfCircle CenterX=-1.5 CenterY=10 CenterZ=0 NormalX=0 NormalY=0 NormalZ=1 AngleXU=0 Radius=1.5 StartAngle=4.71239 EndAngle=7.85398
    g23: ArcOfCircle CenterX=-1.5 CenterY=15.75 CenterZ=0 NormalX=0 NormalY=0 NormalZ=1 AngleXU=0 Radius=1.5 StartAngle=4.71239 EndAngle=7.85398
    g24: LineSegment StartX=-49.19 StartY=69.25 StartZ=0 EndX=-1.5 EndY=69.25 EndZ=0
    g25: LineSegment StartX=-49.19 StartY=66.25 StartZ=0 EndX=-1.5 EndY=66.25 EndZ=0
    g26: LineSegment StartX=-49.19 StartY=63.5 StartZ=0 EndX=-1.5 EndY=63.5 EndZ=0
    g27: LineSegment StartX=-49.19 StartY=60.5 StartZ=0 EndX=-1.5 EndY=60.5 EndZ=0
    g28: LineSegment StartX=-49.19 StartY=57.75 StartZ=0 EndX=-1.5 EndY=57.75 EndZ=0
    g29: LineSegment StartX=-49.19 StartY=54.75 StartZ=0 EndX=-1.5 EndY=54.75 EndZ=0
    g30: LineSegment StartX=-49.19 StartY=52 StartZ=0 EndX=-11.49 EndY=52 EndZ=0
    g31: LineSegment StartX=-49.19 StartY=49 StartZ=0 EndX=-11.49 EndY=49 EndZ=0
    g32: LineSegment StartX=-49.19 StartY=46.25 StartZ=0 EndX=-16.28 EndY=46.25 EndZ=0
    g33: LineSegment StartX=-49.19 StartY=43.25 StartZ=0 EndX=-16.28 EndY=43.25 EndZ=0
    g34: LineSegment StartX=-49.19 StartY=40.5 StartZ=0 EndX=-18.2337 EndY=40.5 EndZ=0
    g35: LineSegment StartX=-49.19 StartY=37.5 StartZ=0 EndX=-18.23 EndY=37.5 EndZ=0
    g36: LineSegment StartX=-49.19 StartY=34.5 StartZ=0 EndX=-18.2337 EndY=34.5 EndZ=0
    g37: LineSegment StartX=-49.19 StartY=31.5 StartZ=0 EndX=-18.23 EndY=31.5 EndZ=0
    g38: LineSegment StartX=-49.19 StartY=28.75 StartZ=0 EndX=-16.2837 EndY=28.75 EndZ=0
    g39: LineSegment StartX=-49.19 StartY=25.75 StartZ=0 EndX=-16.28 EndY=25.75 EndZ=0
    g40: LineSegment StartX=-49.19 StartY=23 StartZ=0 EndX=-11.49 EndY=23 EndZ=0
    g41: LineSegment StartX=-49.19 StartY=20 StartZ=0 EndX=-11.49 EndY=20 EndZ=0
    g42: LineSegment StartX=-49.19 StartY=17.25 StartZ=0 EndX=-1.5 EndY=17.25 EndZ=0
    g43: LineSegment StartX=-49.19 StartY=14.25 StartZ=0 EndX=-1.5 EndY=14.25 EndZ=0
    g44: LineSegment StartX=-49.19 StartY=11.5 StartZ=0 EndX=-1.5 EndY=11.5 EndZ=0
    g45: LineSegment StartX=-49.19 StartY=8.5 StartZ=0 EndX=-1.5 EndY=8.5 EndZ=0
    g46: LineSegment StartX=-49.19 StartY=5.75 StartZ=0 EndX=-1.5 EndY=5.75 EndZ=0
    g47: LineSegment StartX=-49.19 StartY=2.75 StartZ=0 EndX=-1.5 EndY=2.75 EndZ=0
  constraints (120):
    c: Vertical(g0)
    c: Distance(g0) = 3
    c: Block(g0)
    c: Vertical(g1)
    c: Distance(g1) = 3
    c: Vertical(g2)
    c: Equal(g0,g2) = 3
    c: Block(g2)
    c: Vertical(g3)
    c: Equal(g1,g3) = 3
    c: Vertical(g4)
    c: Equal(g0,g4) = 3
    c: Block(g4)
    c: Vertical(g5)
    c: Equal(g1,g5) = 3
    c: Vertical(g6)
    c: Equal(g0,g6) = 3
    c: Block(g6)
    c: Vertical(g7)
    c: Equal(g1,g7) = 3
    c: Vertical(g8)
    c: Equal(g0,g8) = 3
    c: Block(g8)
    c: Vertical(g9)
    c: Equal(g1,g9) = 3
    c: Vertical(g10)
    c: Equal(g0,g10) = 3
    c: Block(g10)
    c: Vertical(g11)
    c: Equal(g1,g11) = 3
    c: Block(g12)
    c: Block(g13)
    c: Block(g14)
    c: Block(g15)
    c: Block(g16)
    c: Block(g17)
    c: Block(g18)
    c: Block(g19)
    c: Block(g20)
    c: Block(g21)
    c: Block(g22)
    c: Block(g23)
    c: Block(g11)
    c: Block(g9)
    c: Block(g7)
    c: Block(g5)
    c: Block(g3)
    c: Block(g1)
    c: Coincident(g24,g0)
    c: Coincident(g24,g12)
    c: Horizontal(g24)
    c: Coincident(g25,g0)
    c: Coincident(g25,g12)
    c: Horizontal(g25)
    c: Coincident(g26,g1)
    c: Coincident(g26,g13)
    c: Horizontal(g26)
    c: Coincident(g27,g1)
    c: Coincident(g27,g13)
    c: Horizontal(g27)
    c: Coincident(g28,g2)
    c: Coincident(g28,g14)
    c: Horizontal(g28)
    c: Coincident(g29,g2)
    c: Coincident(g29,g14)
    c: Horizontal(g29)
    c: Coincident(g30,g3)
    c: Coincident(g30,g15)
    c: Horizontal(g30)
    c: Coincident(g31,g3)
    c: Coincident(g31,g15)
    c: Horizontal(g31)
    c: Coincident(g32,g4)
    c: Coincident(g32,g16)
    c: Horizontal(g32)
    c: Coincident(g33,g4)
    c: Coincident(g33,g16)
    c: Horizontal(g33)
    c: Coincident(g34,g5)
    c: Coincident(g34,g17)
    c: Horizontal(g34)
    c: Coincident(g35,g5)
    c: Coincident(g35,g17)
    c: Horizontal(g35)
    c: Coincident(g36,g6)
    c: Coincident(g36,g19)
    c: Horizontal(g36)
    c: Coincident(g37,g6)
    c: Coincident(g37,g19)
    c: Horizontal(g37)
    c: Coincident(g38,g7)
    c: Coincident(g38,g18)
    c: Horizontal(g38)
    c: Coincident(g39,g7)
    c: Coincident(g39,g18)
    c: Horizontal(g39)
    c: Coincident(g40,g8)
    c: Coincident(g40,g20)
    c: Horizontal(g40)
    c: Coincident(g41,g8)
    c: Coincident(g41,g20)
    c: Horizontal(g41)
    c: Coincident(g42,g9)
    c: Coincident(g42,g23)
    c: Horizontal(g42)
    c: Coincident(g43,g9)
    c: Coincident(g43,g23)
    c: Horizontal(g43)
    c: Coincident(g44,g10)
    c: Coincident(g44,g22)
    c: Horizontal(g44)
    c: Coincident(g45,g10)
    c: Coincident(g45,g22)
    c: Horizontal(g45)
    c: Coincident(g46,g11)
    c: Coincident(g46,g21)
    c: Horizontal(g46)
    c: Coincident(g47,g11)
    c: Coincident(g47,g21)
    c: Horizontal(g47)
FEATURE [Sketcher::SketchObject] Sketch031
  FullyConstrained = true
  Placement = pos=(117,19,0) rot=(0.57735,0.57735,0.57735;2.0944rad)
  sketch-geometry (24):
    g0: ArcOfCircle CenterX=-49.19 CenterY=67.75 CenterZ=0 NormalX=0 NormalY=0 NormalZ=1 AngleXU=0 Radius=1.5 StartAngle=1.5708 EndAngle=4.71239
    g1: ArcOfCircle CenterX=-49.19 CenterY=62 CenterZ=0 NormalX=0 NormalY=0 NormalZ=1 AngleXU=0 Radius=1.5 StartAngle=1.5708 EndAngle=4.71239
    g2: ArcOfCircle CenterX=-49.19 CenterY=56.25 CenterZ=0 NormalX=0 NormalY=0 NormalZ=1 AngleXU=0 Radius=1.5 StartAngle=1.5708 EndAngle=4.71239
    g3: ArcOfCircle CenterX=-49.19 CenterY=50.5 CenterZ=0 NormalX=0 NormalY=0 NormalZ=1 AngleXU=0 Radius=1.5 StartAngle=1.5708 EndAngle=4.71239
    g4: ArcOfCircle CenterX=-49.19 CenterY=44.75 CenterZ=0 NormalX=0 NormalY=0 NormalZ=1 AngleXU=0 Radius=1.5 StartAngle=1.5708 EndAngle=4.71239
    g5: ArcOfCircle CenterX=-49.19 CenterY=39 CenterZ=0 NormalX=0 NormalY=0 NormalZ=1 AngleXU=0 Radius=1.5 StartAngle=1.5708 EndAngle=4.71239
    g6: ArcOfCircle CenterX=-49.19 CenterY=33 CenterZ=0 NormalX=0 NormalY=0 NormalZ=1 AngleXU=0 Radius=1.5 StartAngle=1.5708 EndAngle=4.71239
    g7: ArcOfCircle CenterX=-49.19 CenterY=27.25 CenterZ=0 NormalX=0 NormalY=0 NormalZ=1 AngleXU=0 Radius=1.5 StartAngle=1.5708 EndAngle=4.71239
    g8: ArcOfCircle CenterX=-49.19 CenterY=21.5 CenterZ=0 NormalX=0 NormalY=0 NormalZ=1 AngleXU=0 Radius=1.5 StartAngle=1.5708 EndAngle=4.71239
    g9: ArcOfCircle CenterX=-49.19 CenterY=15.75 CenterZ=0 NormalX=0 NormalY=0 NormalZ=1 AngleXU=0 Radius=1.5 StartAngle=1.5708 EndAngle=4.71239
    g10: ArcOfCircle CenterX=-49.19 CenterY=10 CenterZ=0 NormalX=0 NormalY=0 NormalZ=1 AngleXU=0 Radius=1.5 StartAngle=1.5708 EndAngle=4.71239
    g11: ArcOfCircle CenterX=-49.19 CenterY=4.25 CenterZ=0 NormalX=0 NormalY=0 NormalZ=1 AngleXU=0 Radius=1.5 StartAngle=1.5708 EndAngle=4.71239
    g12: LineSegment StartX=-49.19 StartY=69.25 StartZ=0 EndX=-49.19 EndY=66.25 EndZ=0
    g13: LineSegment StartX=-49.19 StartY=63.5 StartZ=0 EndX=-49.19 EndY=60.5 EndZ=0
    g14: LineSegment StartX=-49.19 StartY=57.75 StartZ=0 EndX=-49.19 EndY=54.75 EndZ=0
    g15: LineSegment StartX=-49.19 StartY=52 StartZ=0 EndX=-49.19 EndY=49 EndZ=0
    g16: LineSegment StartX=-49.19 StartY=46.25 StartZ=0 EndX=-49.19 EndY=43.25 EndZ=0
    g17: LineSegment StartX=-49.19 StartY=40.5 StartZ=0 EndX=-49.19 EndY=37.5 EndZ=0
    g18: LineSegment StartX=-49.19 StartY=34.5 StartZ=0 EndX=-49.19 EndY=31.5 EndZ=0
    g19: LineSegment StartX=-49.19 StartY=28.75 StartZ=0 EndX=-49.19 EndY=25.75 EndZ=0
    g20: LineSegment StartX=-49.19 StartY=23 StartZ=0 EndX=-49.19 EndY=20 EndZ=0
    g21: LineSegment StartX=-49.19 StartY=17.25 StartZ=0 EndX=-49.19 EndY=14.25 EndZ=0
    g22: LineSegment StartX=-49.19 StartY=11.5 StartZ=0 EndX=-49.19 EndY=8.5 EndZ=0
    g23: LineSegment StartX=-49.19 StartY=5.75 StartZ=0 EndX=-49.19 EndY=2.75 EndZ=0
  constraints (48):
    c: Block(g0)
    c: Block(g1)
    c: Block(g2)
    c: Block(g3)
    c: Block(g4)
    c: Block(g5)
    c: Block(g6)
    c: Block(g7)
    c: Block(g8)
    c: Block(g9)
    c: Block(g10)
    c: Block(g11)
    c: Coincident(g12,g0)
    c: Coincident(g12,g0)
    c: Vertical(g12)
    c: Vertical(g13)
    c: Coincident(g13,g1)
    c: Vertical(g14)
    c: Coincident(g14,g2)
    c: Vertical(g15)
    c: Coincident(g15,g3)
    c: Vertical(g16)
    c: Coincident(g16,g4)
    c: Vertical(g17)
    c: Coincident(g17,g5)
    c: Vertical(g18)
    c: Coincident(g18,g6)
    c: Vertical(g19)
    c: Coincident(g19,g7)
    c: Vertical(g20)
    c: Coincident(g20,g8)
    c: Vertical(g21)
    c: Coincident(g21,g9)
    c: Vertical(g22)
    c: Coincident(g22,g10)
    c: Vertical(g23)
    c: Coincident(g23,g11)
    c: Block(g23)
    c: Block(g22)
    c: Block(g21)
    c: Block(g20)
    c: Block(g13)
    c: Block(g14)
    c: Block(g15)
    c: Block(g16)
    c: Block(g17)
    c: Block(g18)
    c: Block(g19)
FEATURE [Part::Extrusion] Extrude022
  Base = -> Sketch030
  Dir = (1,-2e-16,2e-16)
  DirMode = 2
  FaceMakerClass = Part::FaceMakerBullseye
  LengthFwd = 19
  LengthRev = 0
  Placement = pos=(-19,0,0) rot=(0,0,1;0rad)
  Solid = true
  Symmetric = false
FEATURE [Part::Fillet] Fillet022
  Base = -> Extrude022
  Edges = 24 edges r=1.49: [Edge6,Edge11,Edge18,Edge23,Edge30,Edge35,Edge42,Edge47,Edge54,Edge59,Edge66,Edge71,Edge78,Edge83,Edge90,Edge95,Edge102,Edge107,Edge114,Edge119,Edge126,Edge131,Edge138,Edge143]
FEATURE [Part::Cut] Cut020  label="top010"
  Base = -> Cut019
  Tool = -> Fillet022
FEATURE [Sketcher::SketchObject] Sketch032
  FullyConstrained = true
  Placement = pos=(117,19,0) rot=(0.57735,0.57735,0.57735;2.0944rad)
  sketch-geometry (48):
    g0: LineSegment StartX=-49.19 StartY=69.25 StartZ=0 EndX=-49.19 EndY=66.25 EndZ=0
    g1: LineSegment StartX=-49.19 StartY=63.5 StartZ=0 EndX=-49.19 EndY=60.5 EndZ=0
    g2: LineSegment StartX=-49.19 StartY=57.75 StartZ=0 EndX=-49.19 EndY=54.75 EndZ=0
    g3: LineSegment StartX=-49.19 StartY=52 StartZ=0 EndX=-49.19 EndY=49 EndZ=0
    g4: LineSegment StartX=-49.19 StartY=46.25 StartZ=0 EndX=-49.19 EndY=43.25 EndZ=0
    g5: LineSegment StartX=-49.19 StartY=40.5 StartZ=0 EndX=-49.19 EndY=37.5 EndZ=0
    g6: LineSegment StartX=-49.19 StartY=34.5 StartZ=0 EndX=-49.19 EndY=31.5 EndZ=0
    g7: LineSegment StartX=-49.19 StartY=28.75 StartZ=0 EndX=-49.19 EndY=25.75 EndZ=0
    g8: LineSegment StartX=-49.19 StartY=23 StartZ=0 EndX=-49.19 EndY=20 EndZ=0
    g9: LineSegment StartX=-49.19 StartY=17.25 StartZ=0 EndX=-49.19 EndY=14.25 EndZ=0
    g10: LineSegment StartX=-49.19 StartY=11.5 StartZ=0 EndX=-49.19 EndY=8.5 EndZ=0
    g11: LineSegment StartX=-49.19 StartY=5.75 StartZ=0 EndX=-49.19 EndY=2.75 EndZ=0
    g12: ArcOfCircle CenterX=-1.5 CenterY=67.75 CenterZ=0 NormalX=0 NormalY=0 NormalZ=1 AngleXU=0 Radius=1.5 StartAngle=4.71239 EndAngle=7.85398
    g13: ArcOfCircle CenterX=-1.5 CenterY=62 CenterZ=0 NormalX=0 NormalY=0 NormalZ=1 AngleXU=0 Radius=1.5 StartAngle=4.71239 EndAngle=7.85398
    g14: ArcOfCircle CenterX=-1.5 CenterY=56.25 CenterZ=0 NormalX=0 NormalY=0 NormalZ=1 AngleXU=0 Radius=1.5 StartAngle=4.71239 EndAngle=7.85398
    g15: ArcOfCircle CenterX=-11.49 CenterY=50.5 CenterZ=0 NormalX=0 NormalY=0 NormalZ=1 AngleXU=0 Radius=1.5 StartAngle=4.71239 EndAngle=7.85398
    g16: ArcOfCircle CenterX=-16.28 CenterY=44.75 CenterZ=0 NormalX=0 NormalY=0 NormalZ=1 AngleXU=0 Radius=1.5 StartAngle=4.71239 EndAngle=7.85398
    g17: ArcOfCircle CenterX=-18.2337 CenterY=39 CenterZ=0 NormalX=0 NormalY=0 NormalZ=1 AngleXU=0 Radius=1.5 StartAngle=4.71485 EndAngle=7.85398
    g18: ArcOfCircle CenterX=-16.2837 CenterY=27.25 CenterZ=0 NormalX=0 NormalY=0 NormalZ=1 AngleXU=0 Radius=1.5 StartAngle=4.71485 EndAngle=7.85398
    g19: ArcOfCircle CenterX=-18.2337 CenterY=33 CenterZ=0 NormalX=0 NormalY=0 NormalZ=1 AngleXU=0 Radius=1.5 StartAngle=4.71485 EndAngle=7.85398
    g20: ArcOfCircle CenterX=-11.49 CenterY=21.5 CenterZ=0 NormalX=0 NormalY=0 NormalZ=1 AngleXU=0 Radius=1.5 StartAngle=4.71239 EndAngle=7.85398
    g21: ArcOfCircle CenterX=-1.5 CenterY=4.25 CenterZ=0 NormalX=0 NormalY=0 NormalZ=1 AngleXU=0 Radius=1.5 StartAngle=4.71239 EndAngle=7.85398
    g22: ArcOfCircle CenterX=-1.5 CenterY=10 CenterZ=0 NormalX=0 NormalY=0 NormalZ=1 AngleXU=0 Radius=1.5 StartAngle=4.71239 EndAngle=7.85398
    g23: ArcOfCircle CenterX=-1.5 CenterY=15.75 CenterZ=0 NormalX=0 NormalY=0 NormalZ=1 AngleXU=0 Radius=1.5 StartAngle=4.71239 EndAngle=7.85398
    g24: LineSegment StartX=-49.19 StartY=69.25 StartZ=0 EndX=-1.5 EndY=69.25 EndZ=0
    g25: LineSegment StartX=-49.19 StartY=66.25 StartZ=0 EndX=-1.5 EndY=66.25 EndZ=0
    g26: LineSegment StartX=-49.19 StartY=63.5 StartZ=0 EndX=-1.5 EndY=63.5 EndZ=0
    g27: LineSegment StartX=-49.19 StartY=60.5 StartZ=0 EndX=-1.5 EndY=60.5 EndZ=0
    g28: LineSegment StartX=-49.19 StartY=57.75 StartZ=0 EndX=-1.5 EndY=57.75 EndZ=0
    g29: LineSegment StartX=-49.19 StartY=54.75 StartZ=0 EndX=-1.5 EndY=54.75 EndZ=0
    g30: LineSegment StartX=-49.19 StartY=52 StartZ=0 EndX=-11.49 EndY=52 EndZ=0
    g31: LineSegment StartX=-49.19 StartY=49 StartZ=0 EndX=-11.49 EndY=49 EndZ=0
    g32: LineSegment StartX=-49.19 StartY=46.25 StartZ=0 EndX=-16.28 EndY=46.25 EndZ=0
    g33: LineSegment StartX=-49.19 StartY=43.25 StartZ=0 EndX=-16.28 EndY=43.25 EndZ=0
    g34: LineSegment StartX=-49.19 StartY=40.5 StartZ=0 EndX=-18.2337 EndY=40.5 EndZ=0
    g35: LineSegment StartX=-49.19 StartY=37.5 StartZ=0 EndX=-18.23 EndY=37.5 EndZ=0
    g36: LineSegment StartX=-49.19 StartY=34.5 StartZ=0 EndX=-18.2337 EndY=34.5 EndZ=0
    g37: LineSegment StartX=-49.19 StartY=31.5 StartZ=0 EndX=-18.23 EndY=31.5 EndZ=0
    g38: LineSegment StartX=-49.19 StartY=28.75 StartZ=0 EndX=-16.2837 EndY=28.75 EndZ=0
    g39: LineSegment StartX=-49.19 StartY=25.75 StartZ=0 EndX=-16.28 EndY=25.75 EndZ=0
    g40: LineSegment StartX=-49.19 StartY=23 StartZ=0 EndX=-11.49 EndY=23 EndZ=0
    g41: LineSegment StartX=-49.19 StartY=20 StartZ=0 EndX=-11.49 EndY=20 EndZ=0
    g42: LineSegment StartX=-49.19 StartY=17.25 StartZ=0 EndX=-1.5 EndY=17.25 EndZ=0
    g43: LineSegment StartX=-49.19 StartY=14.25 StartZ=0 EndX=-1.5 EndY=14.25 EndZ=0
    g44: LineSegment StartX=-49.19 StartY=11.5 StartZ=0 EndX=-1.5 EndY=11.5 EndZ=0
    g45: LineSegment StartX=-49.19 StartY=8.5 StartZ=0 EndX=-1.5 EndY=8.5 EndZ=0
    g46: LineSegment StartX=-49.19 StartY=5.75 StartZ=0 EndX=-1.5 EndY=5.75 EndZ=0
    g47: LineSegment StartX=-49.19 StartY=2.75 StartZ=0 EndX=-1.5 EndY=2.75 EndZ=0
  constraints (120):
    c: Vertical(g0)
    c: Distance(g0) = 3
    c: Block(g0)
    c: Vertical(g1)
    c: Distance(g1) = 3
    c: Vertical(g2)
    c: Equal(g0,g2) = 3
    c: Block(g2)
    c: Vertical(g3)
    c: Equal(g1,g3) = 3
    c: Vertical(g4)
    c: Equal(g0,g4) = 3
    c: Block(g4)
    c: Vertical(g5)
    c: Equal(g1,g5) = 3
    c: Vertical(g6)
    c: Equal(g0,g6) = 3
    c: Block(g6)
    c: Vertical(g7)
    c: Equal(g1,g7) = 3
    c: Vertical(g8)
    c: Equal(g0,g8) = 3
    c: Block(g8)
    c: Vertical(g9)
    c: Equal(g1,g9) = 3
    c: Vertical(g10)
    c: Equal(g0,g10) = 3
    c: Block(g10)
    c: Vertical(g11)
    c: Equal(g1,g11) = 3
    c: Block(g12)
    c: Block(g13)
    c: Block(g14)
    c: Block(g15)
    c: Block(g16)
    c: Block(g17)
    c: Block(g18)
    c: Block(g19)
    c: Block(g20)
    c: Block(g21)
    c: Block(g22)
    c: Block(g23)
    c: Block(g11)
    c: Block(g9)
    c: Block(g7)
    c: Block(g5)
    c: Block(g3)
    c: Block(g1)
    c: Coincident(g24,g0)
    c: Coincident(g24,g12)
    c: Horizontal(g24)
    c: Coincident(g25,g0)
    c: Coincident(g25,g12)
    c: Horizontal(g25)
    c: Coincident(g26,g1)
    c: Coincident(g26,g13)
    c: Horizontal(g26)
    c: Coincident(g27,g1)
    c: Coincident(g27,g13)
    c: Horizontal(g27)
    c: Coincident(g28,g2)
    c: Coincident(g28,g14)
    c: Horizontal(g28)
    c: Coincident(g29,g2)
    c: Coincident(g29,g14)
    c: Horizontal(g29)
    c: Coincident(g30,g3)
    c: Coincident(g30,g15)
    c: Horizontal(g30)
    c: Coincident(g31,g3)
    c: Coincident(g31,g15)
    c: Horizontal(g31)
    c: Coincident(g32,g4)
    c: Coincident(g32,g16)
    c: Horizontal(g32)
    c: Coincident(g33,g4)
    c: Coincident(g33,g16)
    c: Horizontal(g33)
    c: Coincident(g34,g5)
    c: Coincident(g34,g17)
    c: Horizontal(g34)
    c: Coincident(g35,g5)
    c: Coincident(g35,g17)
    c: Horizontal(g35)
    c: Coincident(g36,g6)
    c: Coincident(g36,g19)
    c: Horizontal(g36)
    c: Coincident(g37,g6)
    c: Coincident(g37,g19)
    c: Horizontal(g37)
    c: Coincident(g38,g7)
    c: Coincident(g38,g18)
    c: Horizontal(g38)
    c: Coincident(g39,g7)
    c: Coincident(g39,g18)
    c: Horizontal(g39)
    c: Coincident(g40,g8)
    c: Coincident(g40,g20)
    c: Horizontal(g40)
    c: Coincident(g41,g8)
    c: Coincident(g41,g20)
    c: Horizontal(g41)
    c: Coincident(g42,g9)
    c: Coincident(g42,g23)
    c: Horizontal(g42)
    c: Coincident(g43,g9)
    c: Coincident(g43,g23)
    c: Horizontal(g43)
    c: Coincident(g44,g10)
    c: Coincident(g44,g22)
    c: Horizontal(g44)
    c: Coincident(g45,g10)
    c: Coincident(g45,g22)
    c: Horizontal(g45)
    c: Coincident(g46,g11)
    c: Coincident(g46,g21)
    c: Horizontal(g46)
    c: Coincident(g47,g11)
    c: Coincident(g47,g21)
    c: Horizontal(g47)
FEATURE [Part::Extrusion] Extrude023
  Base = -> Sketch032
  Dir = (1,-2e-16,2e-16)
  DirMode = 2
  FaceMakerClass = Part::FaceMakerBullseye
  LengthFwd = 19
  LengthRev = 0
  Placement = pos=(-19,0,0) rot=(0,0,1;0rad)
  Solid = true
  Symmetric = false
FEATURE [Part::Fillet] Fillet023
  Base = -> Extrude023
  Edges = <same value as first occurrence — deduplicated (x4 in doc)>
  Placement = pos=(0,0.05,0) rot=(0,0,1;0rad)
FEATURE [Part::Cut] Cut014  label="bottom003"
  Base = -> Cut007
  Tool = -> Fusion047
FEATURE [Part::Cut] Cut021  label="bottom004"
  Base = -> Cut014
  Tool = -> Fillet023
FEATURE [Sketcher::SketchObject] Sketch033
  FullyConstrained = true
  Placement = pos=(117,19,0) rot=(0.57735,0.57735,0.57735;2.0944rad)
  sketch-geometry (8):
    g0: LineSegment StartX=-49.19 StartY=69.25 StartZ=0 EndX=-49.19 EndY=66.25 EndZ=0
    g1: LineSegment StartX=-49.19 StartY=5.75 StartZ=0 EndX=-49.19 EndY=2.75 EndZ=0
    g2: ArcOfCircle CenterX=-1.5 CenterY=67.75 CenterZ=0 NormalX=0 NormalY=0 NormalZ=1 AngleXU=0 Radius=1.5 StartAngle=4.71239 EndAngle=7.85398
    g3: ArcOfCircle CenterX=-1.5 CenterY=4.25 CenterZ=0 NormalX=0 NormalY=0 NormalZ=1 AngleXU=0 Radius=1.5 StartAngle=4.71239 EndAngle=7.85398
    g4: LineSegment StartX=-49.19 StartY=69.25 StartZ=0 EndX=-1.5 EndY=69.25 EndZ=0
    g5: LineSegment StartX=-49.19 StartY=66.25 StartZ=0 EndX=-1.5 EndY=66.25 EndZ=0
    g6: LineSegment StartX=-49.19 StartY=5.75 StartZ=0 EndX=-1.5 EndY=5.75 EndZ=0
    g7: LineSegment StartX=-49.19 StartY=2.75 StartZ=0 EndX=-1.5 EndY=2.75 EndZ=0
  constraints (19):
    c: Vertical(g0)
    c: Distance(g0) = 3
    c: Block(g0)
    c: Vertical(g1)
    c: Block(g2)
    c: Block(g3)
    c: Block(g1)
    c: Coincident(g4,g0)
    c: Coincident(g4,g2)
    c: Horizontal(g4)
    c: Coincident(g5,g0)
    c: Coincident(g5,g2)
    c: Horizontal(g5)
    c: Coincident(g6,g1)
    c: Coincident(g6,g3)
    c: Horizontal(g6)
    c: Coincident(g7,g1)
    c: Coincident(g7,g3)
    c: Horizontal(g7)
FEATURE [Sketcher::SketchObject] Sketch034
  FullyConstrained = true
  Placement = pos=(117,19,0) rot=(0.57735,0.57735,0.57735;2.0944rad)
  sketch-geometry (8):
    g0: LineSegment StartX=-49.19 StartY=63.5 StartZ=0 EndX=-49.19 EndY=60.5 EndZ=0
    g1: LineSegment StartX=-49.19 StartY=11.5 StartZ=0 EndX=-49.19 EndY=8.5 EndZ=0
    g2: ArcOfCircle CenterX=-1.5 CenterY=62 CenterZ=0 NormalX=0 NormalY=0 NormalZ=1 AngleXU=0 Radius=1.5 StartAngle=4.71239 EndAngle=7.85398
    g3: ArcOfCircle CenterX=-1.5 CenterY=10 CenterZ=0 NormalX=0 NormalY=0 NormalZ=1 AngleXU=0 Radius=1.5 StartAngle=4.71239 EndAngle=7.85398
    g4: LineSegment StartX=-49.19 StartY=63.5 StartZ=0 EndX=-1.5 EndY=63.5 EndZ=0
    g5: LineSegment StartX=-49.19 StartY=60.5 StartZ=0 EndX=-1.5 EndY=60.5 EndZ=0
    g6: LineSegment StartX=-49.19 StartY=11.5 StartZ=0 EndX=-1.5 EndY=11.5 EndZ=0
    g7: LineSegment StartX=-49.19 StartY=8.5 StartZ=0 EndX=-1.5 EndY=8.5 EndZ=0
  constraints (19):
    c: Vertical(g0)
    c: Distance(g0) = 3
    c: Vertical(g1)
    c: Block(g1)
    c: Block(g2)
    c: Block(g3)
    c: Block(g0)
    c: Coincident(g4,g0)
    c: Coincident(g4,g2)
    c: Horizontal(g4)
    c: Coincident(g5,g0)
    c: Coincident(g5,g2)
    c: Horizontal(g5)
    c: Coincident(g6,g1)
    c: Coincident(g6,g3)
    c: Horizontal(g6)
    c: Coincident(g7,g1)
    c: Coincident(g7,g3)
    c: Horizontal(g7)
FEATURE [Part::Extrusion] Extrude024
  Base = -> Sketch033
  Dir = (1,0,0)
  DirMode = 2
  FaceMakerClass = Part::FaceMakerBullseye
  LengthFwd = 10
  LengthRev = 0
  Solid = true
  Symmetric = false
FEATURE [Part::Extrusion] Extrude025
  Base = -> Sketch034
  Dir = (1,0,0)
  DirMode = 2
  FaceMakerClass = Part::FaceMakerBullseye
  LengthFwd = 10
  LengthRev = 0
  Solid = true
  Symmetric = false
FEATURE [Part::Fillet] Fillet024  label="removeFromtMoreFrontCaseScrewRetainers"
  Base = -> Extrude024
  Edges = 4 edges r=1.49: [Edge6,Edge11,Edge18,Edge23]
  Placement = pos=(-11,0,0) rot=(0,0,1;0rad)
FEATURE [Part::Fillet] Fillet025  label="removeFromtMoreFrontCaseScrewRetainers001"
  Base = -> Extrude025
  Edges = 4 edges r=1.49: [Edge6,Edge11,Edge18,Edge23]
  Placement = pos=(-19,0,0) rot=(0,0,1;0rad)
FEATURE [Part::Cut] Cut022
  Base = -> Cut015
  Tool = -> Fillet025
FEATURE [Part::Cut] Cut023  label="screwRetainers"
  Base = -> Cut022
  Tool = -> Fillet024
FEATURE [Part::MultiFuse] Fusion056  label="bottom005"
  Shapes = -> [Fusion044,Cut021]
FEATURE [Part::MultiFuse] Fusion057  label="casePillars001"
  Shapes = -> [Cut016,Fusion052]
FEATURE [Part::MultiFuse] Fusion058  label="bottom006"
  Shapes = -> [Fusion056,Cut023]
FEATURE [Part::MultiFuse] Fusion059  label="bottom007"
  Shapes = -> [Fusion058,Fillet005]
FEATURE [Part::MultiFuse] Fusion060  label="bottom008"
  Shapes = -> [Fusion059,Fusion]
FEATURE [Part::MultiFuse] Fusion061  label="top011"
  Shapes = -> [Cut006,Cut020]
FEATURE [Part::MultiFuse] Fusion062  label="top012"
  Shapes = -> [Fusion057,Fusion061]
FEATURE [Sketcher::SketchObject] Sketch035  label="topSketch007"
  FullyConstrained = true
  sketch-geometry (6):
    g0: LineSegment StartX=19 StartY=38 StartZ=0 EndX=117 EndY=38 EndZ=0
    g1: ArcOfCircle CenterX=19 CenterY=19 CenterZ=0 NormalX=0 NormalY=0 NormalZ=1 AngleXU=0 Radius=19 StartAngle=1.5708 EndAngle=3.14159
    g2: LineSegment StartX=117 StartY=38 StartZ=0 EndX=117 EndY=19 EndZ=0
    g3: LineSegment StartX=98 StartY=1.0161e-12 StartZ=0 EndX=5.22862e-06 EndY=1.0161e-12 EndZ=0
    g4: LineSegment StartX=5.22862e-06 StartY=19 StartZ=0 EndX=5.22862e-06 EndY=1.0161e-12 EndZ=0
    g5: ArcOfCircle CenterX=98 CenterY=19 CenterZ=0 NormalX=0 NormalY=0 NormalZ=1 AngleXU=0 Radius=19 StartAngle=4.71239 EndAngle=6.28319
  constraints (16):
    c: Horizontal(g0)
    c: Distance(g0) = 98
    c: Coincident(g1,g0)
    c: Block(g1)
    c: Coincident(g2,g0)
    c: Vertical(g2)
    c: Distance(g2) = 19
    c: Horizontal(g3)
    c: Coincident(g4,g1)
    c: Vertical(g4)
    c: Coincident(g3,g4)
    c: Block(g3)
    c: Coincident(g5,g2)
    c: Coincident(g5,g3)
    c: Block(g0)
    c: Block(g5)
FEATURE [Part::Extrusion] Extrude026  label="sideA001"
  Base = -> Sketch035
  Dir = (0,0,1)
  DirMode = 2
  FaceMakerClass = Part::FaceMakerBullseye
  LengthFwd = 3
  LengthRev = 0
  Placement = pos=(0,0,-2.7) rot=(0,0,1;0rad)
  Solid = true
  Symmetric = false
FEATURE [Sketcher::SketchObject] Sketch036  label="topSketch008"
  FullyConstrained = true
  sketch-geometry (6):
    g0: LineSegment StartX=19 StartY=38 StartZ=0 EndX=117 EndY=38 EndZ=0
    g1: ArcOfCircle CenterX=19 CenterY=19 CenterZ=0 NormalX=0 NormalY=0 NormalZ=1 AngleXU=0 Radius=19 StartAngle=1.5708 EndAngle=3.14159
    g2: LineSegment StartX=117 StartY=38 StartZ=0 EndX=117 EndY=19 EndZ=0
    g3: LineSegment StartX=98 StartY=1.0161e-12 StartZ=0 EndX=5.22862e-06 EndY=1.0161e-12 EndZ=0
    g4: LineSegment StartX=5.22862e-06 StartY=19 StartZ=0 EndX=5.22862e-06 EndY=1.0161e-12 EndZ=0
    g5: ArcOfCircle CenterX=98 CenterY=19 CenterZ=0 NormalX=0 NormalY=0 NormalZ=1 AngleXU=0 Radius=19 StartAngle=4.71239 EndAngle=6.28319
  constraints (16):
    c: Horizontal(g0)
    c: Distance(g0) = 98
    c: Coincident(g1,g0)
    c: Block(g1)
    c: Coincident(g2,g0)
    c: Vertical(g2)
    c: Distance(g2) = 19
    c: Horizontal(g3)
    c: Coincident(g4,g1)
    c: Vertical(g4)
    c: Coincident(g3,g4)
    c: Block(g3)
    c: Coincident(g5,g2)
    c: Coincident(g5,g3)
    c: Block(g0)
    c: Block(g5)
FEATURE [Part::Extrusion] Extrude027  label="sideB001"
  Base = -> Sketch036
  Dir = (0,0,1)
  DirMode = 2
  FaceMakerClass = Part::FaceMakerBullseye
  LengthFwd = 3
  LengthRev = 0
  Placement = pos=(0,0,71.7) rot=(0,0,1;0rad)
  Solid = true
  Symmetric = false
FEATURE [Part::MultiFuse] Fusion064  label="removeFromBottom"
  Shapes = -> [Extrude026,Extrude027]
FEATURE [Part::Cut] Cut024  label="bottom009"
  Base = -> Fusion060
  Tool = -> Fusion064
FEATURE [Sketcher::SketchObject] Sketch037  label="topSketch009"
  FullyConstrained = true
  sketch-geometry (6):
    g0: ArcOfCircle CenterX=19 CenterY=19 CenterZ=0 NormalX=0 NormalY=0 NormalZ=1 AngleXU=0 Radius=19 StartAngle=1.5708 EndAngle=3.14159
    g1: LineSegment StartX=5.22862e-06 StartY=19 StartZ=0 EndX=5.22862e-06 EndY=1.19904e-11 EndZ=0
    g2: LineSegment StartX=19 StartY=38 StartZ=0 EndX=124 EndY=38 EndZ=0
    g3: LineSegment StartX=5.22862e-06 StartY=1.19904e-11 StartZ=0 EndX=105 EndY=1.19904e-11 EndZ=0
    g4: ArcOfCircle CenterX=105 CenterY=19 CenterZ=0 NormalX=0 NormalY=0 NormalZ=1 AngleXU=0 Radius=19 StartAngle=4.71239 EndAngle=6.28319
    g5: LineSegment StartX=124 StartY=38 StartZ=0 EndX=124 EndY=19 EndZ=0
  constraints (16):
    c: Block(g0)
    c: Coincident(g1,g0)
    c: Vertical(g1)
    c: Horizontal(g2)
    c: Distance(g2) = 105
    c: Coincident(g2,g0)
    c: Distance(g1) = 19
    c: Coincident(g3,g1)
    c: Horizontal(g3)
    c: Distance(g3) = 105
    c: Block(g4)
    c: Coincident(g4,g3)
    c: Coincident(g5,g2)
    c: Coincident(g5,g4)
    c: Vertical(g5)
    c: Distance(g5) = 19
FEATURE [Part::Extrusion] Extrude028  label="sideB"
  Base = -> Sketch037
  Dir = (0,0,1)
  DirMode = 2
  FaceMakerClass = Part::FaceMakerBullseye
  LengthFwd = 3
  LengthRev = 0
  Placement = pos=(0,0,72) rot=(0,0,1;0rad)
  Solid = true
  Symmetric = false
FEATURE [Sketcher::SketchObject] Sketch038  label="topSketch010"
  FullyConstrained = true
  sketch-geometry (22):
    g0: LineSegment StartX=5.21097e-06 StartY=3 StartZ=0 EndX=5.21097e-06 EndY=19 EndZ=0
    g1: ArcOfCircle CenterX=19 CenterY=19 CenterZ=0 NormalX=0 NormalY=0 NormalZ=1 AngleXU=0 Radius=19 StartAngle=1.5708 EndAngle=3.14159
    g2: ArcOfCircle CenterX=19 CenterY=19 CenterZ=0 NormalX=0 NormalY=0 NormalZ=1 AngleXU=0 Radius=16 StartAngle=1.5708 EndAngle=3.14159
    g3: LineSegment StartX=114 StartY=35 StartZ=0 EndX=19 EndY=35 EndZ=0
    g4: LineSegment StartX=5.21097e-06 StartY=3 StartZ=0 EndX=5.21097e-06 EndY=0 EndZ=0
    g5: LineSegment StartX=3 StartY=0 StartZ=0 EndX=5.21097e-06 EndY=0 EndZ=0
    g6: LineSegment StartX=3 StartY=19 StartZ=0 EndX=3 EndY=0 EndZ=0
    g7: LineSegment StartX=19 StartY=38 StartZ=0 EndX=124 EndY=38 EndZ=0
    g8: Circle CenterX=119 CenterY=35 CenterZ=0 NormalX=0 NormalY=0 NormalZ=1 AngleXU=0 Radius=1
    g9: Circle CenterX=121 CenterY=35 CenterZ=0 NormalX=0 NormalY=0 NormalZ=1 AngleXU=0 Radius=1
    g10: Circle CenterX=121 CenterY=33 CenterZ=0 NormalX=0 NormalY=0 NormalZ=1 AngleXU=0 Radius=1
    g11: BSplineCurve PolesCount=3 KnotsCount=2 Degree=2 IsPeriodic=0
    g12: GeomPoint X=119 Y=35 Z=0
    g13: GeomPoint X=121 Y=33 Z=0
    g14: LineSegment StartX=119 StartY=35 StartZ=0 EndX=114 EndY=35 EndZ=0
    g15: ArcOfCircle CenterX=105 CenterY=19 CenterZ=0 NormalX=0 NormalY=0 NormalZ=1 AngleXU=0 Radius=16 StartAngle=5.60905 EndAngle=6.28319
    g16: LineSegment StartX=121 StartY=33 StartZ=0 EndX=121 EndY=19 EndZ=0
    g17: LineSegment StartX=117.5 StartY=9.01251 StartZ=0 EndX=121.163 EndY=9.0125 EndZ=0
    g18: ArcOfCircle CenterX=105 CenterY=19 CenterZ=0 NormalX=0 NormalY=0 NormalZ=1 AngleXU=0 Radius=20.6155 StartAngle=5.7297 EndAngle=6.28319
    g19: LineSegment StartX=121.163 StartY=9.0125 StartZ=0 EndX=122.538 EndY=8.16329 EndZ=0
    g20: LineSegment StartX=124 StartY=38 StartZ=0 EndX=125.616 EndY=38 EndZ=0
    g21: LineSegment StartX=125.616 StartY=19 StartZ=0 EndX=125.616 EndY=38 EndZ=0
  constraints (49):
    c: Vertical(g0)
    c: Block(g0)
    c: Coincident(g1,g0)
    c: Block(g1)
    c: Coincident(g2,g1)
    c: Block(g2)
    c: Coincident(g3,g2)
    c: Horizontal(g3)
    c: Tangent(g3,g2)
    c: Coincident(g4,g0)
    c: Distance(g4) = 3
    c: Vertical(g4)
    c: Coincident(g5,g4)
    c: Horizontal(g5)
    c: Coincident(g6,g2)
    c: Coincident(g6,g5)
    c: Vertical(g6)
    c: Horizontal(g7)
    c: Distance(g7) = 105
    c: Coincident(g7,g1)
    c: Block(g3)
    c: Weight(g8) = 1
    c: Equal(g8,g9)
    c: Equal(g8,g10)
    c: InternalAlignment(g8,g11)
    c: InternalAlignment(g9,g11)
    c: InternalAlignment(g10,g11)
    c: InternalAlignment(g12,g11)
    c: InternalAlignment(g13,g11)
    c: Block(g11)
    c: Coincident(g14,g11)
    c: Coincident(g14,g3)
    c: Horizontal(g14)
    c: Block(g15)
    c: Coincident(g16,g11)
    c: Coincident(g16,g15)
    c: Vertical(g16)
    c: Distance(g16) = 14
    c: Coincident(g17,g15)
    c: Block(g18)
    c: Coincident(g19,g18)
    c: Coincident(g20,g7)
    c: Horizontal(g20)
    c: Vertical(g21)
    c: Coincident(g20,g21)
    c: Block(g20)
    c: Block(g21)
    c: Block(g19)
    c: Block(g17)
FEATURE [Part::Extrusion] Extrude029
  Base = -> Sketch038
  Dir = (0,0,1)
  DirMode = 2
  FaceMakerClass = Part::FaceMakerBullseye
  LengthFwd = 72
  LengthRev = 0
  Solid = true
  Symmetric = false
FEATURE [Part::Feature] Face085
  shape: bbox 4.8 x 25.5 x 2e-07 mm, 1 faces, 0 solids (baked)
FEATURE [Part::Revolution] Revolve089  label="moreFrontCaseScrewPost003"
  Angle = 360
  Axis = (0,1,0)
  Base = (0,0,0)
  FaceMakerClass = Part::FaceMakerBullseye
  Placement = pos=(109.5,4.5,3.5) rot=(0,0,1;0rad)
  Solid = false
  Source = -> Face085
  Symmetric = false
FEATURE [Part::Feature] Face086
  shape: bbox 4.8 x 25.5 x 2e-07 mm, 1 faces, 0 solids (baked)
FEATURE [Part::Revolution] Revolve090  label="moreFrontCaseScrewPost004"
  Angle = 360
  Axis = (0,1,0)
  Base = (0,0,0)
  FaceMakerClass = Part::FaceMakerBullseye
  Placement = pos=(109.5,4.5,68.5) rot=(0,0,1;0rad)
  Solid = false
  Source = -> Face086
  Symmetric = false
FEATURE [Part::Fillet] Fillet026  label="top013"
  Base = -> Extrude029
  Edges = 1 edges r=2: [Edge35]
FEATURE [Sketcher::SketchObject] Sketch039
  FullyConstrained = true
  sketch-geometry (7):
    g0: LineSegment StartX=0 StartY=0 StartZ=0 EndX=0 EndY=6 EndZ=0
    g1: Circle CenterX=0 CenterY=0 CenterZ=0 NormalX=0 NormalY=0 NormalZ=1 AngleXU=0 Radius=1
    g2: Circle CenterX=8 CenterY=6 CenterZ=0 NormalX=0 NormalY=0 NormalZ=1 AngleXU=0 Radius=1
    g3: BSplineCurve PolesCount=3 KnotsCount=2 Degree=2 IsPeriodic=0
    g4: GeomPoint X=0 Y=0 Z=0
    g5: GeomPoint X=8 Y=6 Z=0
    g6: LineSegment StartX=0 StartY=6 StartZ=0 EndX=8 EndY=6 EndZ=0
  constraints (14):
    c: Coincident(g0,g-1)
    c: Distance(g0) = 6
    c: Vertical(g0)
    c: Coincident(g3,g0)
    c: Weight(g1) = 1
    c: Equal(g1,g2)
    c: InternalAlignment(g1,g3)
    c: InternalAlignment(g2,g3)
    c: InternalAlignment(g4,g3)
    c: InternalAlignment(g5,g3)
    c: Block(g3)
    c: Coincident(g6,g0)
    c: Coincident(g6,g3)
    c: Horizontal(g6)
FEATURE [Sketcher::SketchObject] Sketch040
  FullyConstrained = true
  sketch-geometry (7):
    g0: LineSegment StartX=0 StartY=0 StartZ=0 EndX=0 EndY=6 EndZ=0
    g1: Circle CenterX=0 CenterY=0 CenterZ=0 NormalX=0 NormalY=0 NormalZ=1 AngleXU=0 Radius=1
    g2: Circle CenterX=8 CenterY=6 CenterZ=0 NormalX=0 NormalY=0 NormalZ=1 AngleXU=0 Radius=1
    g3: BSplineCurve PolesCount=3 KnotsCount=2 Degree=2 IsPeriodic=0
    g4: GeomPoint X=0 Y=0 Z=0
    g5: GeomPoint X=8 Y=6 Z=0
    g6: LineSegment StartX=0 StartY=6 StartZ=0 EndX=8 EndY=6 EndZ=0
  constraints (14):
    c: Coincident(g0,g-1)
    c: Distance(g0) = 6
    c: Vertical(g0)
    c: Coincident(g3,g0)
    c: Weight(g1) = 1
    c: Equal(g1,g2)
    c: InternalAlignment(g1,g3)
    c: InternalAlignment(g2,g3)
    c: InternalAlignment(g4,g3)
    c: InternalAlignment(g5,g3)
    c: Block(g3)
    c: Coincident(g6,g0)
    c: Coincident(g6,g3)
    c: Horizontal(g6)
FEATURE [Sketcher::SketchObject] Sketch041
  FullyConstrained = true
  sketch-geometry (7):
    g0: LineSegment StartX=0 StartY=0 StartZ=0 EndX=0 EndY=6 EndZ=0
    g1: Circle CenterX=0 CenterY=0 CenterZ=0 NormalX=0 NormalY=0 NormalZ=1 AngleXU=0 Radius=1
    g2: Circle CenterX=8 CenterY=6 CenterZ=0 NormalX=0 NormalY=0 NormalZ=1 AngleXU=0 Radius=1
    g3: BSplineCurve PolesCount=3 KnotsCount=2 Degree=2 IsPeriodic=0
    g4: GeomPoint X=0 Y=0 Z=0
    g5: GeomPoint X=8 Y=6 Z=0
    g6: LineSegment StartX=0 StartY=6 StartZ=0 EndX=8 EndY=6 EndZ=0
  constraints (14):
    c: Coincident(g0,g-1)
    c: Distance(g0) = 6
    c: Vertical(g0)
    c: Coincident(g3,g0)
    c: Weight(g1) = 1
    c: Equal(g1,g2)
    c: InternalAlignment(g1,g3)
    c: InternalAlignment(g2,g3)
    c: InternalAlignment(g4,g3)
    c: InternalAlignment(g5,g3)
    c: Block(g3)
    c: Coincident(g6,g0)
    c: Coincident(g6,g3)
    c: Horizontal(g6)
FEATURE [Sketcher::SketchObject] Sketch042
  FullyConstrained = true
  sketch-geometry (7):
    g0: LineSegment StartX=0 StartY=0 StartZ=0 EndX=0 EndY=6 EndZ=0
    g1: Circle CenterX=0 CenterY=0 CenterZ=0 NormalX=0 NormalY=0 NormalZ=1 AngleXU=0 Radius=1
    g2: Circle CenterX=8 CenterY=6 CenterZ=0 NormalX=0 NormalY=0 NormalZ=1 AngleXU=0 Radius=1
    g3: BSplineCurve PolesCount=3 KnotsCount=2 Degree=2 IsPeriodic=0
    g4: GeomPoint X=0 Y=0 Z=0
    g5: GeomPoint X=8 Y=6 Z=0
    g6: LineSegment StartX=0 StartY=6 StartZ=0 EndX=8 EndY=6 EndZ=0
  constraints (14):
    c: Coincident(g0,g-1)
    c: Distance(g0) = 6
    c: Vertical(g0)
    c: Coincident(g3,g0)
    c: Weight(g1) = 1
    c: Equal(g1,g2)
    c: InternalAlignment(g1,g3)
    c: InternalAlignment(g2,g3)
    c: InternalAlignment(g4,g3)
    c: InternalAlignment(g5,g3)
    c: Block(g3)
    c: Coincident(g6,g0)
    c: Coincident(g6,g3)
    c: Horizontal(g6)
FEATURE [Part::Extrusion] Extrude030  label="caseScrewPillarBracket008"
  Base = -> Sketch039
  Dir = (0,0,1)
  DirMode = 2
  FaceMakerClass = Part::FaceMakerBullseye
  LengthFwd = 2.4
  LengthRev = 0
  Placement = pos=(15.76,29,8.8) rot=(0,1,0;0rad)
  Solid = true
  Symmetric = false
FEATURE [Part::Extrusion] Extrude031  label="caseScrewPillarBracket009"
  Base = -> Sketch040
  Dir = (0,0,1)
  DirMode = 2
  FaceMakerClass = Part::FaceMakerBullseye
  LengthFwd = 2.4
  LengthRev = 0
  Placement = pos=(15.76,29,60.8) rot=(0,0,1;0rad)
  Solid = true
  Symmetric = false
FEATURE [Part::Extrusion] Extrude032  label="caseScrewPillarBracket010"
  Base = -> Sketch041
  Dir = (0,0,1)
  DirMode = 2
  FaceMakerClass = Part::FaceMakerBullseye
  LengthFwd = 2.4
  LengthRev = 0
  Placement = pos=(13.7,29,13.26) rot=(0,-1,0;1.5708rad)
  Solid = true
  Symmetric = false
FEATURE [Part::Extrusion] Extrude033  label="caseScrewPillarBracket011"
  Base = -> Sketch042
  Dir = (0,0,1)
  DirMode = 2
  FaceMakerClass = Part::FaceMakerBullseye
  LengthFwd = 2.4
  LengthRev = 0
  Placement = pos=(11.3,29,58.74) rot=(0,1,0;1.5708rad)
  Solid = true
  Symmetric = false
FEATURE [Sketcher::SketchObject] Sketch043
  FullyConstrained = true
  sketch-geometry (7):
    g0: LineSegment StartX=0 StartY=0 StartZ=0 EndX=0 EndY=6 EndZ=0
    g1: Circle CenterX=0 CenterY=0 CenterZ=0 NormalX=0 NormalY=0 NormalZ=1 AngleXU=0 Radius=1
    g2: Circle CenterX=8 CenterY=6 CenterZ=0 NormalX=0 NormalY=0 NormalZ=1 AngleXU=0 Radius=1
    g3: BSplineCurve PolesCount=3 KnotsCount=2 Degree=2 IsPeriodic=0
    g4: GeomPoint X=0 Y=0 Z=0
    g5: GeomPoint X=8 Y=6 Z=0
    g6: LineSegment StartX=0 StartY=6 StartZ=0 EndX=8 EndY=6 EndZ=0
  constraints (14):
    c: Coincident(g0,g-1)
    c: Distance(g0) = 6
    c: Vertical(g0)
    c: Coincident(g3,g0)
    c: Weight(g1) = 1
    c: Equal(g1,g2)
    c: InternalAlignment(g1,g3)
    c: InternalAlignment(g2,g3)
    c: InternalAlignment(g4,g3)
    c: InternalAlignment(g5,g3)
    c: Block(g3)
    c: Coincident(g6,g0)
    c: Coincident(g6,g3)
    c: Horizontal(g6)
FEATURE [Part::Extrusion] Extrude034  label="caseScrewPillarBracket012"
  Base = -> Sketch043
  Dir = (0,0,1)
  DirMode = 2
  FaceMakerClass = Part::FaceMakerBullseye
  LengthFwd = 2.4
  LengthRev = 0
  Placement = pos=(88.3,29,65.23) rot=(0,1,0;1.5708rad)
  Solid = true
  Symmetric = false
FEATURE [Sketcher::SketchObject] Sketch044
  FullyConstrained = true
  sketch-geometry (7):
    g0: LineSegment StartX=0 StartY=0 StartZ=0 EndX=0 EndY=6 EndZ=0
    g1: Circle CenterX=0 CenterY=0 CenterZ=0 NormalX=0 NormalY=0 NormalZ=1 AngleXU=0 Radius=1
    g2: Circle CenterX=8 CenterY=6 CenterZ=0 NormalX=0 NormalY=0 NormalZ=1 AngleXU=0 Radius=1
    g3: BSplineCurve PolesCount=3 KnotsCount=2 Degree=2 IsPeriodic=0
    g4: GeomPoint X=0 Y=0 Z=0
    g5: GeomPoint X=8 Y=6 Z=0
    g6: LineSegment StartX=0 StartY=6 StartZ=0 EndX=8 EndY=6 EndZ=0
  constraints (14):
    c: Coincident(g0,g-1)
    c: Distance(g0) = 6
    c: Vertical(g0)
    c: Coincident(g3,g0)
    c: Weight(g1) = 1
    c: Equal(g1,g2)
    c: InternalAlignment(g1,g3)
    c: InternalAlignment(g2,g3)
    c: InternalAlignment(g4,g3)
    c: InternalAlignment(g5,g3)
    c: Block(g3)
    c: Coincident(g6,g0)
    c: Coincident(g6,g3)
    c: Horizontal(g6)
FEATURE [Part::Extrusion] Extrude035  label="caseScrewPillarBracket013"
  Base = -> Sketch044
  Dir = (0,0,1)
  DirMode = 2
  FaceMakerClass = Part::FaceMakerBullseye
  LengthFwd = 2.4
  LengthRev = 0
  Placement = pos=(90.7,29,6.77) rot=(0,-1,0;1.5708rad)
  Solid = true
  Symmetric = false
FEATURE [Sketcher::SketchObject] Sketch045
  FullyConstrained = true
  sketch-geometry (7):
    g0: LineSegment StartX=0 StartY=0 StartZ=0 EndX=0 EndY=6 EndZ=0
    g1: Circle CenterX=0 CenterY=0 CenterZ=0 NormalX=0 NormalY=0 NormalZ=1 AngleXU=0 Radius=1
    g2: Circle CenterX=8 CenterY=6 CenterZ=0 NormalX=0 NormalY=0 NormalZ=1 AngleXU=0 Radius=1
    g3: BSplineCurve PolesCount=3 KnotsCount=2 Degree=2 IsPeriodic=0
    g4: GeomPoint X=0 Y=0 Z=0
    g5: GeomPoint X=8 Y=6 Z=0
    g6: LineSegment StartX=0 StartY=6 StartZ=0 EndX=8 EndY=6 EndZ=0
  constraints (14):
    c: Coincident(g0,g-1)
    c: Distance(g0) = 6
    c: Vertical(g0)
    c: Coincident(g3,g0)
    c: Weight(g1) = 1
    c: Equal(g1,g2)
    c: InternalAlignment(g1,g3)
    c: InternalAlignment(g2,g3)
    c: InternalAlignment(g4,g3)
    c: InternalAlignment(g5,g3)
    c: Block(g3)
    c: Coincident(g6,g0)
    c: Coincident(g6,g3)
    c: Horizontal(g6)
FEATURE [Sketcher::SketchObject] Sketch046
  FullyConstrained = true
  sketch-geometry (7):
    g0: LineSegment StartX=0 StartY=0 StartZ=0 EndX=0 EndY=6 EndZ=0
    g1: Circle CenterX=0 CenterY=0 CenterZ=0 NormalX=0 NormalY=0 NormalZ=1 AngleXU=0 Radius=1
    g2: Circle CenterX=8 CenterY=6 CenterZ=0 NormalX=0 NormalY=0 NormalZ=1 AngleXU=0 Radius=1
    g3: BSplineCurve PolesCount=3 KnotsCount=2 Degree=2 IsPeriodic=0
    g4: GeomPoint X=0 Y=0 Z=0
    g5: GeomPoint X=8 Y=6 Z=0
    g6: LineSegment StartX=0 StartY=6 StartZ=0 EndX=8 EndY=6 EndZ=0
  constraints (14):
    c: Coincident(g0,g-1)
    c: Distance(g0) = 6
    c: Vertical(g0)
    c: Coincident(g3,g0)
    c: Weight(g1) = 1
    c: Equal(g1,g2)
    c: InternalAlignment(g1,g3)
    c: InternalAlignment(g2,g3)
    c: InternalAlignment(g4,g3)
    c: InternalAlignment(g5,g3)
    c: Block(g3)
    c: Coincident(g6,g0)
    c: Coincident(g6,g3)
    c: Horizontal(g6)
FEATURE [Part::Extrusion] Extrude036  label="caseScrewPillarBracket014"
  Base = -> Sketch045
  Dir = (0,0,1)
  DirMode = 2
  FaceMakerClass = Part::FaceMakerBullseye
  LengthFwd = 2.4
  LengthRev = 0
  Placement = pos=(110.7,29,6.77) rot=(0,-1,0;1.5708rad)
  Solid = true
  Symmetric = false
FEATURE [Part::Extrusion] Extrude037  label="caseScrewPillarBracket015"
  Base = -> Sketch046
  Dir = (0,0,1)
  DirMode = 2
  FaceMakerClass = Part::FaceMakerBullseye
  LengthFwd = 2.4
  LengthRev = 0
  Placement = pos=(108.3,29,65.23) rot=(0,1,0;1.5708rad)
  Solid = true
  Symmetric = false
FEATURE [Part::Box] Box013  label="frontCaseScrewPillarBracket002"
  AttacherType = Attacher::AttachEngine3D
  Height = 2.4
  Length = 22
  Placement = pos=(87,28,2.3) rot=(0,0,1;0rad)
  Width = 7
FEATURE [Part::Box] Box014  label="frontCaseScrewPillarBracket003"
  AttacherType = Attacher::AttachEngine3D
  Height = 2.4
  Length = 22
  Placement = pos=(87,28,67.3) rot=(0,0,1;0rad)
  Width = 7
FEATURE [Part::Feature] Face087
  shape: bbox 4.8 x 30.2 x 2e-07 mm, 1 faces, 0 solids (baked)
FEATURE [Part::Revolution] Revolve091  label="frontCaseScrewPost004"
  Angle = 360
  Axis = (0,1,0)
  Base = (0,0,0)
  FaceMakerClass = Part::FaceMakerBullseye
  Placement = pos=(89.5,4.5,3.5) rot=(0,0,1;0rad)
  Solid = false
  Source = -> Face087
  Symmetric = false
FEATURE [Part::Feature] Face088
  shape: bbox 4.8 x 30.2 x 2e-07 mm, 1 faces, 0 solids (baked)
FEATURE [Part::Revolution] Revolve092  label="frontCaseScrewPost005"
  Angle = 360
  Axis = (0,1,0)
  Base = (0,0,0)
  FaceMakerClass = Part::FaceMakerBullseye
  Placement = pos=(89.5,4.5,68.5) rot=(0,0,1;0rad)
  Solid = false
  Source = -> Face088
  Symmetric = false
FEATURE [Part::Feature] Face089
  shape: bbox 3.5 x 30.2 x 2e-07 mm, 1 faces, 0 solids (baked)
FEATURE [Part::Revolution] Revolve093  label="backCaseScrewPost002"
  Angle = 360
  Axis = (0,1,0)
  Base = (0,0,0)
  FaceMakerClass = Part::FaceMakerBullseye
  Placement = pos=(12.5,4.5,10) rot=(0,0,1;0rad)
  Solid = false
  Source = -> Face089
  Symmetric = false
FEATURE [Part::Feature] Face090
  shape: bbox 3.5 x 30.2 x 2e-07 mm, 1 faces, 0 solids (baked)
FEATURE [Part::Revolution] Revolve094  label="backCaseScrewPost003"
  Angle = 360
  Axis = (0,1,0)
  Base = (0,0,0)
  FaceMakerClass = Part::FaceMakerBullseye
  Placement = pos=(12.5,4.5,62) rot=(0,0,1;0rad)
  Solid = false
  Source = -> Face090
  Symmetric = false
FEATURE [Part::Box] Box015  label="Cube011"
  AttacherType = Attacher::AttachEngine3D
  Height = 28.8
  Length = 3
  Placement = pos=(107.3,28,21.6) rot=(0,0,1;0rad)
  Width = 7
FEATURE [Part::Box] Box016  label="Cube012"
  AttacherType = Attacher::AttachEngine3D
  Height = 3
  Length = 7.4
  Placement = pos=(107.3,28,18.6) rot=(0,0,1;0rad)
  Width = 7
FEATURE [Part::Box] Box017  label="Cube013"
  AttacherType = Attacher::AttachEngine3D
  Height = 3
  Length = 7.4
  Placement = pos=(107.3,28,50.4) rot=(0,0,1;0rad)
  Width = 7
FEATURE [Part::Cylinder] Cylinder024
  Angle = 360
  AttacherType = Attacher::AttachEngine3D
  Height = 20
  Placement = pos=(0,0,36.15) rot=(0,0,1;0rad)
  Radius = 14.3
FEATURE [Part::Cylinder] Cylinder025
  Angle = 360
  AttacherType = Attacher::AttachEngine3D
  Height = 10
  Placement = pos=(0,0,36.15) rot=(0,0,1;0rad)
  Radius = 4
FEATURE [Part::MultiFuse] Fusion066  label="removeToCreteHoleForPlugHousing009"
  Placement = pos=(70,19,36) rot=(0,1,0;1.5708rad)
  Shapes = -> [Cylinder024,Cylinder025]
FEATURE [Part::MultiFuse] Fusion065  label="plugHousingBracketHolder002"
  Shapes = -> [Box017,Box015,Box016]
FEATURE [Part::Cut] Cut025  label="plugHousingBracketHolder003"
  Base = -> Fusion065
  Placement = pos=(7,0,0) rot=(0,0,1;0rad)
  Tool = -> Fusion066
FEATURE [Sketcher::SketchObject] Sketch047
  FullyConstrained = false
  Placement = pos=(0,0,0) rot=(1,0,0;1.5708rad)
  sketch-geometry (24):
    g0: ArcOfCircle CenterX=-4 CenterY=-10.5 CenterZ=0 NormalX=0 NormalY=0 NormalZ=1 AngleXU=0 Radius=1.5 StartAngle=6e-16 EndAngle=3.14159
    g1: ArcOfCircle CenterX=-34.2 CenterY=-10.5 CenterZ=0 NormalX=0 NormalY=0 NormalZ=1 AngleXU=0 Radius=1.5 StartAngle=0 EndAngle=3.14159
    g2: ArcOfCircle CenterX=-34.2 CenterY=-27.7 CenterZ=0 NormalX=0 NormalY=0 NormalZ=1 AngleXU=0 Radius=1.5 StartAngle=3.14159 EndAngle=6.28319
    g3: ArcOfCircle CenterX=-4 CenterY=-27.7 CenterZ=0 NormalX=0 NormalY=0 NormalZ=1 AngleXU=0 Radius=1.5 StartAngle=3.1416 EndAngle=6.28319
    g4: ArcOfCircle CenterX=-10 CenterY=-4.3 CenterZ=0 NormalX=0 NormalY=0 NormalZ=1 AngleXU=0 Radius=1.5 StartAngle=2e-16 EndAngle=3.14159
    g5: ArcOfCircle CenterX=-16.1 CenterY=-1.8 CenterZ=0 NormalX=0 NormalY=0 NormalZ=1 AngleXU=0 Radius=1.5 StartAngle=5e-16 EndAngle=3.14159
    g6: ArcOfCircle CenterX=-22.1 CenterY=-1.8 CenterZ=0 NormalX=0 NormalY=0 NormalZ=1 AngleXU=0 Radius=1.5 StartAngle=5e-16 EndAngle=3.14159
    g7: ArcOfCircle CenterX=-28.2 CenterY=-4.3 CenterZ=0 NormalX=0 NormalY=0 NormalZ=1 AngleXU=0 Radius=1.5 StartAngle=2e-16 EndAngle=3.14159
    g8: ArcOfCircle CenterX=-10 CenterY=-33.9 CenterZ=0 NormalX=0 NormalY=0 NormalZ=1 AngleXU=0 Radius=1.5 StartAngle=3.14159 EndAngle=6.28319
    g9: ArcOfCircle CenterX=-16.1 CenterY=-36.4 CenterZ=0 NormalX=0 NormalY=0 NormalZ=1 AngleXU=0 Radius=1.5 StartAngle=3.14159 EndAngle=6.28319
    g10: ArcOfCircle CenterX=-22.1 CenterY=-36.4 CenterZ=0 NormalX=0 NormalY=0 NormalZ=1 AngleXU=0 Radius=1.5 StartAngle=3.14159 EndAngle=6.28319
    g11: ArcOfCircle CenterX=-28.2 CenterY=-33.9 CenterZ=0 NormalX=0 NormalY=0 NormalZ=1 AngleXU=0 Radius=1.5 StartAngle=3.14159 EndAngle=6.28319
    g12: LineSegment StartX=-35.7 StartY=-10.5 StartZ=0 EndX=-35.7 EndY=-27.7 EndZ=0
    g13: LineSegment StartX=-32.7 StartY=-10.5 StartZ=0 EndX=-32.7 EndY=-27.7 EndZ=0
    g14: LineSegment StartX=-29.7 StartY=-33.9 StartZ=0 EndX=-29.7 EndY=-4.3 EndZ=0
    g15: LineSegment StartX=-26.7 StartY=-33.9 StartZ=0 EndX=-26.7 EndY=-4.3 EndZ=0
    g16: LineSegment StartX=-2.5 StartY=-10.5 StartZ=0 EndX=-2.5 EndY=-27.7 EndZ=0
    g17: LineSegment StartX=-8.5 StartY=-4.3 StartZ=0 EndX=-8.5 EndY=-33.9 EndZ=0
    g18: LineSegment StartX=-5.5 StartY=-10.5 StartZ=0 EndX=-5.5 EndY=-27.7 EndZ=0
    g19: LineSegment StartX=-11.5 StartY=-4.3 StartZ=0 EndX=-11.5 EndY=-33.9 EndZ=0
    g20: LineSegment StartX=-14.6 StartY=-1.8 StartZ=0 EndX=-14.6 EndY=-36.4 EndZ=0
    g21: LineSegment StartX=-17.6 StartY=-1.8 StartZ=0 EndX=-17.6 EndY=-36.4 EndZ=0
    g22: LineSegment StartX=-20.6 StartY=-36.4 StartZ=0 EndX=-20.6 EndY=-1.8 EndZ=0
    g23: LineSegment StartX=-23.6 StartY=-1.8 StartZ=0 EndX=-23.6 EndY=-36.4 EndZ=0
  constraints (48):
    c: Block(g0)
    c: Block(g1)
    c: Block(g2)
    c: Block(g3)
    c: Block(g4)
    c: Block(g5)
    c: Block(g6)
    c: Block(g7)
    c: Block(g8)
    c: Block(g9)
    c: Block(g10)
    c: Block(g11)
    c: Coincident(g12,g1)
    c: Coincident(g12,g2)
    c: Vertical(g12)
    c: Coincident(g13,g1)
    c: Coincident(g13,g2)
    c: Vertical(g13)
    c: Coincident(g14,g11)
    c: Coincident(g14,g7)
    c: Vertical(g14)
    c: Coincident(g15,g11)
    c: Coincident(g15,g7)
    c: Vertical(g15)
    c: Coincident(g16,g0)
    c: Coincident(g16,g3)
    c: Vertical(g16)
    c: Coincident(g17,g4)
    c: Coincident(g17,g8)
    c: Vertical(g17)
    c: Coincident(g18,g0)
    c: Coincident(g18,g3)
    c: Vertical(g18)
    c: Coincident(g19,g4)
    c: Coincident(g19,g8)
    c: Vertical(g19)
    c: Coincident(g20,g5)
    c: Coincident(g20,g9)
    c: Vertical(g20)
    c: Coincident(g21,g5)
    c: Coincident(g21,g9)
    c: Vertical(g21)
    c: Coincident(g22,g10)
    c: Coincident(g22,g6)
    c: Vertical(g22)
    c: Coincident(g23,g6)
    c: Coincident(g23,g10)
    c: Vertical(g23)
FEATURE [Part::Extrusion] Extrude038  label="removeToCreateFanGrillHoles001"
  Base = -> Sketch047
  Dir = (0,-1,6e-16)
  DirMode = 2
  FaceMakerClass = Part::FaceMakerBullseye
  LengthFwd = 10
  LengthRev = 0
  Placement = pos=(65.4,44,54.82) rot=(0,0,1;0rad)
  Solid = true
  Symmetric = false
FEATURE [Part::Feature] Wire004
  shape: bbox 11 x 5.2 x 2e-07 mm, 0 faces, 0 solids (baked)
FEATURE [Part::Revolution] Revolve095
  Angle = 360
  Axis = (0,1,0)
  Base = (0,0,0)
  FaceMakerClass = Part::FaceMakerBullseye
  Placement = pos=(30.3,38,19.7) rot=(0,0,1;0rad)
  Solid = true
  Source = -> Wire004
  Symmetric = false
FEATURE [Part::Feature] Wire005
  shape: bbox 11 x 5.2 x 2e-07 mm, 0 faces, 0 solids (baked)
FEATURE [Part::Revolution] Revolve096
  Angle = 360
  Axis = (0,1,0)
  Base = (0,0,0)
  FaceMakerClass = Part::FaceMakerBullseye
  Placement = pos=(30.3,38,51.7) rot=(0,0,1;0rad)
  Solid = true
  Source = -> Wire005
  Symmetric = false
FEATURE [Part::Feature] Wire006
  shape: bbox 11 x 5.2 x 2e-07 mm, 0 faces, 0 solids (baked)
FEATURE [Part::Revolution] Revolve097
  Angle = 360
  Axis = (0,1,0)
  Base = (0,0,0)
  FaceMakerClass = Part::FaceMakerBullseye
  Placement = pos=(62.3,38,51.7) rot=(0,0,1;0rad)
  Solid = true
  Source = -> Wire006
  Symmetric = false
FEATURE [Part::Feature] Wire007
  shape: bbox 11 x 5.2 x 2e-07 mm, 0 faces, 0 solids (baked)
FEATURE [Part::Revolution] Revolve098
  Angle = 360
  Axis = (0,1,0)
  Base = (0,0,0)
  FaceMakerClass = Part::FaceMakerBullseye
  Placement = pos=(62.3,38,19.7) rot=(0,0,1;0rad)
  Solid = true
  Source = -> Wire007
  Symmetric = false
FEATURE [Part::MultiFuse] Fusion067  label="fanScrewHousing002"
  Shapes = -> [Revolve098,Revolve097,Revolve096,Revolve095]
FEATURE [Part::Feature] Face091 .. Face094  x4 (patterned run collapsed; names and placements below)
  shape: bbox 3.5 x 17.8 x 2e-07 mm, 1 faces, 0 solids (baked)
FEATURE [Part::Revolution] Revolve099  label="removeToCreateScrewAndThreadedInsertHole026"
  Angle = 360
  Axis = (0,1,0)
  Base = (0,0,0)
  FaceMakerClass = Part::FaceMakerBullseye
  Placement = pos=(62.3,30.3,19.7) rot=(0,0,1;0rad)
  Solid = false
  Source = -> Face091
  Symmetric = false
FEATURE [Part::Revolution] Revolve100  label="removeToCreateScrewAndThreadedInsertHole027"
  Angle = 360
  Axis = (0,1,0)
  Base = (0,0,0)
  FaceMakerClass = Part::FaceMakerBullseye
  Placement = pos=(62.3,30.3,51.7) rot=(0,0,1;0rad)
  Solid = false
  Source = -> Face092
  Symmetric = false
FEATURE [Part::Revolution] Revolve101  label="removeToCreateScrewAndThreadedInsertHole028"
  Angle = 360
  Axis = (0,1,0)
  Base = (0,0,0)
  FaceMakerClass = Part::FaceMakerBullseye
  Placement = pos=(30.3,30.3,19.7) rot=(0,0,1;0rad)
  Solid = false
  Source = -> Face093
  Symmetric = false
FEATURE [Part::Revolution] Revolve102  label="removeToCreateScrewAndThreadedInsertHole029"
  Angle = 360
  Axis = (0,1,0)
  Base = (0,0,0)
  FaceMakerClass = Part::FaceMakerBullseye
  Placement = pos=(30.3,30.3,51.7) rot=(0,0,1;0rad)
  Solid = false
  Source = -> Face094
  Symmetric = false
FEATURE [Part::MultiFuse] Fusion068  label="createThreadedInsertHolesForFan002"
  Shapes = -> [Revolve099,Revolve100,Revolve101,Revolve102]
FEATURE [Part::Cut] Cut026  label="fanScrewHousing003"
  Base = -> Fusion067
  Tool = -> Fusion068
FEATURE [Sketcher::SketchObject] Sketch048
  FullyConstrained = false
  Placement = pos=(0,0,0) rot=(1,0,0;1.5708rad)
  sketch-geometry (24):
    g0: ArcOfCircle CenterX=-4 CenterY=-10.5 CenterZ=0 NormalX=0 NormalY=0 NormalZ=1 AngleXU=0 Radius=1.5 StartAngle=6e-16 EndAngle=3.14159
    g1: ArcOfCircle CenterX=-34.2 CenterY=-10.5 CenterZ=0 NormalX=0 NormalY=0 NormalZ=1 AngleXU=0 Radius=1.5 StartAngle=0 EndAngle=3.14159
    g2: ArcOfCircle CenterX=-34.2 CenterY=-27.7 CenterZ=0 NormalX=0 NormalY=0 NormalZ=1 AngleXU=0 Radius=1.5 StartAngle=3.14159 EndAngle=6.28319
    g3: ArcOfCircle CenterX=-4 CenterY=-27.7 CenterZ=0 NormalX=0 NormalY=0 NormalZ=1 AngleXU=0 Radius=1.5 StartAngle=3.1416 EndAngle=6.28319
    g4: ArcOfCircle CenterX=-10 CenterY=-4.3 CenterZ=0 NormalX=0 NormalY=0 NormalZ=1 AngleXU=0 Radius=1.5 StartAngle=2e-16 EndAngle=3.14159
    g5: ArcOfCircle CenterX=-16.1 CenterY=-1.8 CenterZ=0 NormalX=0 NormalY=0 NormalZ=1 AngleXU=0 Radius=1.5 StartAngle=5e-16 EndAngle=3.14159
    g6: ArcOfCircle CenterX=-22.1 CenterY=-1.8 CenterZ=0 NormalX=0 NormalY=0 NormalZ=1 AngleXU=0 Radius=1.5 StartAngle=5e-16 EndAngle=3.14159
    g7: ArcOfCircle CenterX=-28.2 CenterY=-4.3 CenterZ=0 NormalX=0 NormalY=0 NormalZ=1 AngleXU=0 Radius=1.5 StartAngle=2e-16 EndAngle=3.14159
    g8: ArcOfCircle CenterX=-10 CenterY=-33.9 CenterZ=0 NormalX=0 NormalY=0 NormalZ=1 AngleXU=0 Radius=1.5 StartAngle=3.14159 EndAngle=6.28319
    g9: ArcOfCircle CenterX=-16.1 CenterY=-36.4 CenterZ=0 NormalX=0 NormalY=0 NormalZ=1 AngleXU=0 Radius=1.5 StartAngle=3.14159 EndAngle=6.28319
    g10: ArcOfCircle CenterX=-22.1 CenterY=-36.4 CenterZ=0 NormalX=0 NormalY=0 NormalZ=1 AngleXU=0 Radius=1.5 StartAngle=3.14159 EndAngle=6.28319
    g11: ArcOfCircle CenterX=-28.2 CenterY=-33.9 CenterZ=0 NormalX=0 NormalY=0 NormalZ=1 AngleXU=0 Radius=1.5 StartAngle=3.14159 EndAngle=6.28319
    g12: LineSegment StartX=-35.7 StartY=-10.5 StartZ=0 EndX=-35.7 EndY=-27.7 EndZ=0
    g13: LineSegment StartX=-32.7 StartY=-10.5 StartZ=0 EndX=-32.7 EndY=-27.7 EndZ=0
    g14: LineSegment StartX=-29.7 StartY=-33.9 StartZ=0 EndX=-29.7 EndY=-4.3 EndZ=0
    g15: LineSegment StartX=-26.7 StartY=-33.9 StartZ=0 EndX=-26.7 EndY=-4.3 EndZ=0
    g16: LineSegment StartX=-2.5 StartY=-10.5 StartZ=0 EndX=-2.5 EndY=-27.7 EndZ=0
    g17: LineSegment StartX=-8.5 StartY=-4.3 StartZ=0 EndX=-8.5 EndY=-33.9 EndZ=0
    g18: LineSegment StartX=-5.5 StartY=-10.5 StartZ=0 EndX=-5.5 EndY=-27.7 EndZ=0
    g19: LineSegment StartX=-11.5 StartY=-4.3 StartZ=0 EndX=-11.5 EndY=-33.9 EndZ=0
    g20: LineSegment StartX=-14.6 StartY=-1.8 StartZ=0 EndX=-14.6 EndY=-36.4 EndZ=0
    g21: LineSegment StartX=-17.6 StartY=-1.8 StartZ=0 EndX=-17.6 EndY=-36.4 EndZ=0
    g22: LineSegment StartX=-20.6 StartY=-36.4 StartZ=0 EndX=-20.6 EndY=-1.8 EndZ=0
    g23: LineSegment StartX=-23.6 StartY=-1.8 StartZ=0 EndX=-23.6 EndY=-36.4 EndZ=0
  constraints (48):
    c: Block(g0)
    c: Block(g1)
    c: Block(g2)
    c: Block(g3)
    c: Block(g4)
    c: Block(g5)
    c: Block(g6)
    c: Block(g7)
    c: Block(g8)
    c: Block(g9)
    c: Block(g10)
    c: Block(g11)
    c: Coincident(g12,g1)
    c: Coincident(g12,g2)
    c: Vertical(g12)
    c: Coincident(g13,g1)
    c: Coincident(g13,g2)
    c: Vertical(g13)
    c: Coincident(g14,g11)
    c: Coincident(g14,g7)
    c: Vertical(g14)
    c: Coincident(g15,g11)
    c: Coincident(g15,g7)
    c: Vertical(g15)
    c: Coincident(g16,g0)
    c: Coincident(g16,g3)
    c: Vertical(g16)
    c: Coincident(g17,g4)
    c: Coincident(g17,g8)
    c: Vertical(g17)
    c: Coincident(g18,g0)
    c: Coincident(g18,g3)
    c: Vertical(g18)
    c: Coincident(g19,g4)
    c: Coincident(g19,g8)
    c: Vertical(g19)
    c: Coincident(g20,g5)
    c: Coincident(g20,g9)
    c: Vertical(g20)
    c: Coincident(g21,g5)
    c: Coincident(g21,g9)
    c: Vertical(g21)
    c: Coincident(g22,g10)
    c: Coincident(g22,g6)
    c: Vertical(g22)
    c: Coincident(g23,g6)
    c: Coincident(g23,g10)
    c: Vertical(g23)
FEATURE [Part::Extrusion] Extrude039  label="removeToCreateFanGrillHoles002"
  Base = -> Sketch048
  Dir = (0,-1,6e-16)
  DirMode = 2
  FaceMakerClass = Part::FaceMakerBullseye
  LengthFwd = 10
  LengthRev = 0
  Placement = pos=(65.4,44,54.82) rot=(0,0,1;0rad)
  Solid = true
  Symmetric = false
FEATURE [Part::Cut] Cut027  label="fanScrewHousing004"
  Base = -> Cut026
  Tool = -> Extrude038
FEATURE [Part::Cut] Cut028  label="top014"
  Base = -> Fillet026
  Tool = -> Extrude039
FEATURE [Part::Feature] Face095 .. Face098  x4 (patterned run collapsed; names and placements below)
  shape: bbox 3.5 x 17.8 x 2e-07 mm, 1 faces, 0 solids (baked)
FEATURE [Part::Revolution] Revolve103  label="removeToCreateScrewAndThreadedInsertHole030"
  Angle = 360
  Axis = (0,1,0)
  Base = (0,0,0)
  FaceMakerClass = Part::FaceMakerBullseye
  Placement = pos=(62.3,30.3,19.7) rot=(0,0,1;0rad)
  Solid = false
  Source = -> Face095
  Symmetric = false
FEATURE [Part::Revolution] Revolve104  label="removeToCreateScrewAndThreadedInsertHole031"
  Angle = 360
  Axis = (0,1,0)
  Base = (0,0,0)
  FaceMakerClass = Part::FaceMakerBullseye
  Placement = pos=(62.3,30.3,51.7) rot=(0,0,1;0rad)
  Solid = false
  Source = -> Face096
  Symmetric = false
FEATURE [Part::Revolution] Revolve105  label="removeToCreateScrewAndThreadedInsertHole032"
  Angle = 360
  Axis = (0,1,0)
  Base = (0,0,0)
  FaceMakerClass = Part::FaceMakerBullseye
  Placement = pos=(30.3,30.3,19.7) rot=(0,0,1;0rad)
  Solid = false
  Source = -> Face097
  Symmetric = false
FEATURE [Part::Revolution] Revolve106  label="removeToCreateScrewAndThreadedInsertHole033"
  Angle = 360
  Axis = (0,1,0)
  Base = (0,0,0)
  FaceMakerClass = Part::FaceMakerBullseye
  Placement = pos=(30.3,30.3,51.7) rot=(0,0,1;0rad)
  Solid = false
  Source = -> Face098
  Symmetric = false
FEATURE [Part::MultiFuse] Fusion069  label="createThreadedInsertHolesForFan003"
  Shapes = -> [Revolve103,Revolve104,Revolve105,Revolve106]
FEATURE [Part::Cut] Cut029  label="top015"
  Base = -> Cut028
  Tool = -> Fusion054
FEATURE [Part::Cut] Cut030  label="fanScrewHousing005"
  Base = -> Cut027
  Tool = -> Fusion069
FEATURE [Part::Cylinder] Cylinder026  label="removeToCreteHoleForPlugHousing010"
  Angle = 360
  AttacherType = Attacher::AttachEngine3D
  Height = 20
  Placement = pos=(-2,19,36) rot=(0,1,0;1.5708rad)
  Radius = 14.3
FEATURE [Part::Box] Box018  label="removeToCreteHoleForPlugHousing011"
  AttacherType = Attacher::AttachEngine3D
  Height = 28.6
  Length = 10
  Placement = pos=(-2,0,21.7) rot=(0,0,1;0rad)
  Width = 19
FEATURE [Part::Box] Box019  label="wireHolderBottomCaseBit"
  AttacherType = Attacher::AttachEngine3D
  Height = 28
  Length = 3
  Placement = pos=(0,0,22) rot=(0,0,1;0rad)
  Width = 21
FEATURE [Part::Cylinder] Cylinder027  label="removeToCreteHoleForPlugHousing012"
  Angle = 360
  AttacherType = Attacher::AttachEngine3D
  Height = 20
  Placement = pos=(-2,19,36) rot=(0,1,0;1.5708rad)
  Radius = 14.3
FEATURE [Part::Cut] Cut031  label="wireHolderBottomCaseBit001"
  Base = -> Box019
  Tool = -> Cylinder027
FEATURE [Part::MultiFuse] Fusion070  label="removeToCreteHoleForPlugHousing013"
  Shapes = -> [Box018,Cylinder026]
FEATURE [Part::Cut] Cut032  label="top016"
  Base = -> Cut029
  Tool = -> Fusion070
FEATURE [Part::Cylinder] Cylinder028
  Angle = 360
  AttacherType = Attacher::AttachEngine3D
  Height = 20
  Placement = pos=(0,0,36.15) rot=(0,0,1;0rad)
  Radius = 14.3
FEATURE [Part::Cylinder] Cylinder029
  Angle = 360
  AttacherType = Attacher::AttachEngine3D
  Height = 10
  Placement = pos=(0,0,36.15) rot=(0,0,1;0rad)
  Radius = 4
FEATURE [Part::MultiFuse] Fusion071  label="removeToCreteHoleForPlugHousing014"
  Placement = pos=(70,19,36) rot=(0,1,0;1.5708rad)
  Shapes = -> [Cylinder028,Cylinder029]
FEATURE [Sketcher::SketchObject] Sketch049  label="topSketch011"
  FullyConstrained = true
  sketch-geometry (4):
    g0: ArcOfCircle CenterX=105 CenterY=19 CenterZ=0 NormalX=0 NormalY=0 NormalZ=1 AngleXU=0 Radius=20.6155 StartAngle=5.54125 EndAngle=6.28319
    g1: ArcOfCircle CenterX=105 CenterY=19 CenterZ=0 NormalX=0 NormalY=0 NormalZ=1 AngleXU=0 Radius=13 StartAngle=5.54125 EndAngle=6.28319
    g2: LineSegment StartX=118 StartY=19 StartZ=0 EndX=125.616 EndY=19 EndZ=0
    g3: LineSegment StartX=114.583 StartY=10.2157 StartZ=0 EndX=120.197 EndY=5.06982 EndZ=0
  constraints (7):
    c: Block(g0)
    c: Block(g1)
    c: Coincident(g2,g1)
    c: Coincident(g2,g0)
    c: Horizontal(g2)
    c: Coincident(g3,g1)
    c: Coincident(g3,g0)
FEATURE [Part::Box] Box020  label="removeToCreteHoleForPlugHousing015"
  AttacherType = Attacher::AttachEngine3D
  Height = 28.6
  Length = 20
  Placement = pos=(106.15,0,21.7) rot=(0,0,1;0rad)
  Width = 19
FEATURE [Part::MultiFuse] Fusion072  label="removeToCreteHoleForPlugHousing016"
  Shapes = -> [Box020,Fusion071]
FEATURE [Part::Cut] Cut033  label="removeToCreteHoleForPlugHousing017"
  Base = -> Cut032
  Tool = -> Fusion072
FEATURE [Part::Cylinder] Cylinder030
  Angle = 360
  AttacherType = Attacher::AttachEngine3D
  Height = 20
  Placement = pos=(0,0,36.15) rot=(0,0,1;0rad)
  Radius = 14.3
FEATURE [Part::Cylinder] Cylinder031
  Angle = 360
  AttacherType = Attacher::AttachEngine3D
  Height = 10
  Placement = pos=(0,0,36.15) rot=(0,0,1;0rad)
  Radius = 4
FEATURE [Part::Box] Box021  label="removeToCreteHoleForPlugHousing019"
  AttacherType = Attacher::AttachEngine3D
  Height = 28.6
  Length = 20
  Placement = pos=(106.15,0,21.7) rot=(0,0,1;0rad)
  Width = 19
FEATURE [Part::MultiFuse] Fusion074  label="removeToCreteHoleForPlugHousing020"
  Placement = pos=(70,19,36) rot=(0,1,0;1.5708rad)
  Shapes = -> [Cylinder030,Cylinder031]
FEATURE [Part::MultiFuse] Fusion073  label="removeToCreteHoleForPlugHousing018"
  Placement = pos=(0,0,28.3) rot=(0,0,1;0rad)
  Shapes = -> [Box021,Fusion074]
FEATURE [Part::Cylinder] Cylinder032
  Angle = 360
  AttacherType = Attacher::AttachEngine3D
  Height = 20
  Placement = pos=(0,0,36.15) rot=(0,0,1;0rad)
  Radius = 14.3
FEATURE [Part::Cylinder] Cylinder033
  Angle = 360
  AttacherType = Attacher::AttachEngine3D
  Height = 10
  Placement = pos=(0,0,36.15) rot=(0,0,1;0rad)
  Radius = 4
FEATURE [Part::Box] Box022  label="removeToCreteHoleForPlugHousing021"
  AttacherType = Attacher::AttachEngine3D
  Height = 28.6
  Length = 20
  Placement = pos=(106.15,0,21.7) rot=(0,0,1;0rad)
  Width = 19
FEATURE [Part::MultiFuse] Fusion076  label="removeToCreteHoleForPlugHousing023"
  Placement = pos=(70,19,36) rot=(0,1,0;1.5708rad)
  Shapes = -> [Cylinder032,Cylinder033]
FEATURE [Part::MultiFuse] Fusion075  label="removeToCreteHoleForPlugHousing022"
  Placement = pos=(0,0,-28.3) rot=(0,0,1;0rad)
  Shapes = -> [Box022,Fusion076]
FEATURE [Part::MultiFuse] Fusion077  label="removeToCreatePlugHousingBottomBit"
  Shapes = -> [Fusion075,Fusion073]
FEATURE [Part::Cylinder] Cylinder034
  Angle = 360
  AttacherType = Attacher::AttachEngine3D
  Height = 20
  Placement = pos=(0,0,36.15) rot=(0,0,1;0rad)
  Radius = 14.3
FEATURE [Part::Cylinder] Cylinder035
  Angle = 360
  AttacherType = Attacher::AttachEngine3D
  Height = 10
  Placement = pos=(0,0,36.15) rot=(0,0,1;0rad)
  Radius = 4
FEATURE [Part::MultiFuse] Fusion078  label="removeToCreteHoleForPlugHousing024"
  Placement = pos=(70,19,36) rot=(0,1,0;1.5708rad)
  Shapes = -> [Cylinder034,Cylinder035]
FEATURE [Part::MultiFuse] Fusion079  label="removeToCreatePlugHousingBottomBit001"
  Shapes = -> [Fusion078,Fusion077]
FEATURE [Part::Extrusion] Extrude040  label="bottomPlugHousingBit"
  Base = -> Sketch049
  Dir = (0,0,1)
  DirMode = 2
  FaceMakerClass = Part::FaceMakerBullseye
  LengthFwd = 72
  LengthRev = 0
  Solid = true
  Symmetric = false
FEATURE [Part::Cut] Cut034  label="bottomPlugHousingBit001"
  Base = -> Extrude040
  Tool = -> Fusion079
FEATURE [Part::Box] Box023  label="Cube014"
  AttacherType = Attacher::AttachEngine3D
  Height = 16
  Length = 8
  Placement = pos=(12.7,31.52,28) rot=(0,0,1;0rad)
  Width = 4
FEATURE [Part::Cylinder] Cylinder036
  Angle = 360
  AttacherType = Attacher::AttachEngine3D
  Height = 10
  Placement = pos=(0,0,36.15) rot=(0,0,1;0rad)
  Radius = 4
FEATURE [Part::Cylinder] Cylinder037
  Angle = 360
  AttacherType = Attacher::AttachEngine3D
  Height = 20
  Placement = pos=(0,0,36.15) rot=(0,0,1;0rad)
  Radius = 8.2
FEATURE [Part::MultiFuse] Fusion080  label="removeToCreteHoleForPlugHousing025"
  Placement = pos=(-42,19,36) rot=(0,1,0;1.5708rad)
  Shapes = -> [Cylinder037,Cylinder036]
FEATURE [Sketcher::SketchObject] Sketch050  label="topSketch012"
  FullyConstrained = true
  sketch-geometry (4):
    g0: LineSegment StartX=16.8446 StartY=31.512 StartZ=0 EndX=16.3251 EndY=34.4666 EndZ=0
    g1: ArcOfCircle CenterX=19 CenterY=19.2524 CenterZ=0 NormalX=0 NormalY=0 NormalZ=1 AngleXU=0 Radius=15.4476 StartAngle=1.74483 EndAngle=2.72717
    g2: ArcOfCircle CenterX=19 CenterY=19.2524 CenterZ=0 NormalX=0 NormalY=0 NormalZ=1 AngleXU=0 Radius=12.4476 StartAngle=1.74483 EndAngle=2.73189
    g3: LineSegment StartX=4.86004 StartY=25.4725 StartZ=0 EndX=7.58253 EndY=24.2107 EndZ=0
  constraints (7):
    c: Block(g0)
    c: Coincident(g1,g0)
    c: Coincident(g2,g0)
    c: Coincident(g3,g1)
    c: Coincident(g3,g2)
    c: Block(g1)
    c: Block(g2)
FEATURE [Part::Extrusion] Extrude041
  Base = -> Sketch050
  Dir = (0,0,1)
  DirMode = 2
  FaceMakerClass = Part::FaceMakerBullseye
  LengthFwd = 10.6
  LengthRev = 0
  Placement = pos=(0,0,31) rot=(0,0,1;0rad)
  Solid = true
  Symmetric = false
FEATURE [Part::Cut] Cut035
  Base = -> Extrude041
  Placement = pos=(0,0,-0.3) rot=(0,0,1;0rad)
  Tool = -> Fusion080
FEATURE [Part::Cut] Cut036
  Base = -> Box023
  Tool = -> Cut035
FEATURE [Part::Fillet] Fillet027
  Base = -> Cut036
  Edges = 1 edges r=0.7: [Edge13]
FEATURE [Part::Fillet] Fillet028
  Base = -> Fillet027
  Edges = 1 edges r=0.7: [Edge13]
FEATURE [Part::Fillet] Fillet029
  Base = -> Fillet028
  Edges = 1 edges r=0.7: [Edge16]
FEATURE [Part::Fillet] Fillet030
  Base = -> Fillet029
  Edges = 1 edges r=0.7: [Edge11]
FEATURE [Part::Fillet] Fillet031
  Base = -> Fillet030
  Edges = 1 edges r=0.7: [Edge10]
FEATURE [Part::Fillet] Fillet032
  Base = -> Fillet031
  Edges = 1 edges r=1.2: [Edge5]
FEATURE [Part::Fillet] Fillet033
  Base = -> Fillet032
  Edges = 1 edges r=1.2: [Edge12]
FEATURE [Part::Fillet] Fillet034  label="wireHousingRetainer"
  Base = -> Fillet033
  Edges = 1 edges r=2: [Edge1]
  Placement = pos=(0.3,0,0) rot=(0,0,1;0rad)
FEATURE [Part::Feature] Face099
  shape: bbox 3.5 x 17.8 x 2e-07 mm, 1 faces, 0 solids (baked)
FEATURE [Part::Revolution] Revolve107  label="removeToCreateScrewAndThreadedInsertHole034"
  Angle = 360
  Axis = (0,1,0)
  Base = (0,0,0)
  FaceMakerClass = Part::FaceMakerBullseye
  Placement = pos=(12.5,0,10) rot=(0,0,1;0rad)
  Solid = false
  Source = -> Face099
  Symmetric = false
FEATURE [Part::Feature] Face100
  shape: bbox 3.5 x 17.8 x 2e-07 mm, 1 faces, 0 solids (baked)
FEATURE [Part::Revolution] Revolve108  label="removeToCreateScrewAndThreadedInsertHole035"
  Angle = 360
  Axis = (0,1,0)
  Base = (0,0,0)
  FaceMakerClass = Part::FaceMakerBullseye
  Placement = pos=(12.5,0,62) rot=(0,0,1;0rad)
  Solid = false
  Source = -> Face100
  Symmetric = false
FEATURE [Part::Feature] Face101
  shape: bbox 3.5 x 17.8 x 2e-07 mm, 1 faces, 0 solids (baked)
FEATURE [Part::Revolution] Revolve109  label="removeToCreateScrewAndThreadedInsertHole036"
  Angle = 360
  Axis = (0,1,0)
  Base = (0,0,0)
  FaceMakerClass = Part::FaceMakerBullseye
  Placement = pos=(89.5,0,68.5) rot=(0,0,1;0rad)
  Solid = false
  Source = -> Face101
  Symmetric = false
FEATURE [Part::Feature] Face102
  shape: bbox 3.5 x 17.8 x 2e-07 mm, 1 faces, 0 solids (baked)
FEATURE [Part::Revolution] Revolve110  label="removeToCreateScrewAndThreadedInsertHole037"
  Angle = 360
  Axis = (0,1,0)
  Base = (0,0,0)
  FaceMakerClass = Part::FaceMakerBullseye
  Placement = pos=(89.5,0,3.5) rot=(0,0,1;0rad)
  Solid = false
  Source = -> Face102
  Symmetric = false
FEATURE [Part::Feature] Face103
  shape: bbox 3.5 x 17.8 x 2e-07 mm, 1 faces, 0 solids (baked)
FEATURE [Part::Revolution] Revolve111  label="removeToCreateScrewAndThreadedInsertHole038"
  Angle = 360
  Axis = (0,1,0)
  Base = (0,0,0)
  FaceMakerClass = Part::FaceMakerBullseye
  Placement = pos=(109.5,4.7,3.5) rot=(0,0,1;0rad)
  Solid = false
  Source = -> Face103
  Symmetric = false
FEATURE [Part::Feature] Face104
  shape: bbox 3.5 x 17.8 x 2e-07 mm, 1 faces, 0 solids (baked)
FEATURE [Part::Revolution] Revolve112  label="removeToCreateScrewAndThreadedInsertHole039"
  Angle = 360
  Axis = (0,1,0)
  Base = (0,0,0)
  FaceMakerClass = Part::FaceMakerBullseye
  Placement = pos=(109.5,4.7,68.5) rot=(0,0,1;0rad)
  Solid = false
  Source = -> Face104
  Symmetric = false
FEATURE [Part::MultiFuse] Fusion081  label="removeToCreateScrewAndThreadedInsertHole040"
  Shapes = -> [Revolve107,Revolve108,Revolve109,Revolve110,Revolve111,Revolve112]
FEATURE [Part::MultiFuse] Fusion082  label="casePillars002"
  Shapes = -> [Revolve094,Revolve092,Revolve090,Revolve089,Revolve091,Revolve093]
FEATURE [Part::Cut] Cut037  label="casePillars003"
  Base = -> Fusion082
  Tool = -> Fusion081
FEATURE [Sketcher::SketchObject] Sketch051
  FullyConstrained = true
  Placement = pos=(117,19,0) rot=(0.57735,0.57735,0.57735;2.0944rad)
  sketch-geometry (48):
    g0: LineSegment StartX=-49.19 StartY=69.25 StartZ=0 EndX=-49.19 EndY=66.25 EndZ=0
    g1: LineSegment StartX=-49.19 StartY=63.5 StartZ=0 EndX=-49.19 EndY=60.5 EndZ=0
    g2: LineSegment StartX=-49.19 StartY=57.75 StartZ=0 EndX=-49.19 EndY=54.75 EndZ=0
    g3: LineSegment StartX=-49.19 StartY=52 StartZ=0 EndX=-49.19 EndY=49 EndZ=0
    g4: LineSegment StartX=-49.19 StartY=46.25 StartZ=0 EndX=-49.19 EndY=43.25 EndZ=0
    g5: LineSegment StartX=-49.19 StartY=40.5 StartZ=0 EndX=-49.19 EndY=37.5 EndZ=0
    g6: LineSegment StartX=-49.19 StartY=34.5 StartZ=0 EndX=-49.19 EndY=31.5 EndZ=0
    g7: LineSegment StartX=-49.19 StartY=28.75 StartZ=0 EndX=-49.19 EndY=25.75 EndZ=0
    g8: LineSegment StartX=-49.19 StartY=23 StartZ=0 EndX=-49.19 EndY=20 EndZ=0
    g9: LineSegment StartX=-49.19 StartY=17.25 StartZ=0 EndX=-49.19 EndY=14.25 EndZ=0
    g10: LineSegment StartX=-49.19 StartY=11.5 StartZ=0 EndX=-49.19 EndY=8.5 EndZ=0
    g11: LineSegment StartX=-49.19 StartY=5.75 StartZ=0 EndX=-49.19 EndY=2.75 EndZ=0
    g12: ArcOfCircle CenterX=-1.5 CenterY=67.75 CenterZ=0 NormalX=0 NormalY=0 NormalZ=1 AngleXU=0 Radius=1.5 StartAngle=4.71239 EndAngle=7.85398
    g13: ArcOfCircle CenterX=-1.5 CenterY=62 CenterZ=0 NormalX=0 NormalY=0 NormalZ=1 AngleXU=0 Radius=1.5 StartAngle=4.71239 EndAngle=7.85398
    g14: ArcOfCircle CenterX=-1.5 CenterY=56.25 CenterZ=0 NormalX=0 NormalY=0 NormalZ=1 AngleXU=0 Radius=1.5 StartAngle=4.71239 EndAngle=7.85398
    g15: ArcOfCircle CenterX=-11.49 CenterY=50.5 CenterZ=0 NormalX=0 NormalY=0 NormalZ=1 AngleXU=0 Radius=1.5 StartAngle=4.71239 EndAngle=7.85398
    g16: ArcOfCircle CenterX=-16.28 CenterY=44.75 CenterZ=0 NormalX=0 NormalY=0 NormalZ=1 AngleXU=0 Radius=1.5 StartAngle=4.71239 EndAngle=7.85398
    g17: ArcOfCircle CenterX=-18.2337 CenterY=39 CenterZ=0 NormalX=0 NormalY=0 NormalZ=1 AngleXU=0 Radius=1.5 StartAngle=4.71485 EndAngle=7.85398
    g18: ArcOfCircle CenterX=-16.2837 CenterY=27.25 CenterZ=0 NormalX=0 NormalY=0 NormalZ=1 AngleXU=0 Radius=1.5 StartAngle=4.71485 EndAngle=7.85398
    g19: ArcOfCircle CenterX=-18.2337 CenterY=33 CenterZ=0 NormalX=0 NormalY=0 NormalZ=1 AngleXU=0 Radius=1.5 StartAngle=4.71485 EndAngle=7.85398
    g20: ArcOfCircle CenterX=-11.49 CenterY=21.5 CenterZ=0 NormalX=0 NormalY=0 NormalZ=1 AngleXU=0 Radius=1.5 StartAngle=4.71239 EndAngle=7.85398
    g21: ArcOfCircle CenterX=-1.5 CenterY=4.25 CenterZ=0 NormalX=0 NormalY=0 NormalZ=1 AngleXU=0 Radius=1.5 StartAngle=4.71239 EndAngle=7.85398
    g22: ArcOfCircle CenterX=-1.5 CenterY=10 CenterZ=0 NormalX=0 NormalY=0 NormalZ=1 AngleXU=0 Radius=1.5 StartAngle=4.71239 EndAngle=7.85398
    g23: ArcOfCircle CenterX=-1.5 CenterY=15.75 CenterZ=0 NormalX=0 NormalY=0 NormalZ=1 AngleXU=0 Radius=1.5 StartAngle=4.71239 EndAngle=7.85398
    g24: LineSegment StartX=-49.19 StartY=69.25 StartZ=0 EndX=-1.5 EndY=69.25 EndZ=0
    g25: LineSegment StartX=-49.19 StartY=66.25 StartZ=0 EndX=-1.5 EndY=66.25 EndZ=0
    g26: LineSegment StartX=-49.19 StartY=63.5 StartZ=0 EndX=-1.5 EndY=63.5 EndZ=0
    g27: LineSegment StartX=-49.19 StartY=60.5 StartZ=0 EndX=-1.5 EndY=60.5 EndZ=0
    g28: LineSegment StartX=-49.19 StartY=57.75 StartZ=0 EndX=-1.5 EndY=57.75 EndZ=0
    g29: LineSegment StartX=-49.19 StartY=54.75 StartZ=0 EndX=-1.5 EndY=54.75 EndZ=0
    g30: LineSegment StartX=-49.19 StartY=52 StartZ=0 EndX=-11.49 EndY=52 EndZ=0
    g31: LineSegment StartX=-49.19 StartY=49 StartZ=0 EndX=-11.49 EndY=49 EndZ=0
    g32: LineSegment StartX=-49.19 StartY=46.25 StartZ=0 EndX=-16.28 EndY=46.25 EndZ=0
    g33: LineSegment StartX=-49.19 StartY=43.25 StartZ=0 EndX=-16.28 EndY=43.25 EndZ=0
    g34: LineSegment StartX=-49.19 StartY=40.5 StartZ=0 EndX=-18.2337 EndY=40.5 EndZ=0
    g35: LineSegment StartX=-49.19 StartY=37.5 StartZ=0 EndX=-18.23 EndY=37.5 EndZ=0
    g36: LineSegment StartX=-49.19 StartY=34.5 StartZ=0 EndX=-18.2337 EndY=34.5 EndZ=0
    g37: LineSegment StartX=-49.19 StartY=31.5 StartZ=0 EndX=-18.23 EndY=31.5 EndZ=0
    g38: LineSegment StartX=-49.19 StartY=28.75 StartZ=0 EndX=-16.2837 EndY=28.75 EndZ=0
    g39: LineSegment StartX=-49.19 StartY=25.75 StartZ=0 EndX=-16.28 EndY=25.75 EndZ=0
    g40: LineSegment StartX=-49.19 StartY=23 StartZ=0 EndX=-11.49 EndY=23 EndZ=0
    g41: LineSegment StartX=-49.19 StartY=20 StartZ=0 EndX=-11.49 EndY=20 EndZ=0
    g42: LineSegment StartX=-49.19 StartY=17.25 StartZ=0 EndX=-1.5 EndY=17.25 EndZ=0
    g43: LineSegment StartX=-49.19 StartY=14.25 StartZ=0 EndX=-1.5 EndY=14.25 EndZ=0
    g44: LineSegment StartX=-49.19 StartY=11.5 StartZ=0 EndX=-1.5 EndY=11.5 EndZ=0
    g45: LineSegment StartX=-49.19 StartY=8.5 StartZ=0 EndX=-1.5 EndY=8.5 EndZ=0
    g46: LineSegment StartX=-49.19 StartY=5.75 StartZ=0 EndX=-1.5 EndY=5.75 EndZ=0
    g47: LineSegment StartX=-49.19 StartY=2.75 StartZ=0 EndX=-1.5 EndY=2.75 EndZ=0
  constraints (120):
    c: Vertical(g0)
    c: Distance(g0) = 3
    c: Block(g0)
    c: Vertical(g1)
    c: Distance(g1) = 3
    c: Vertical(g2)
    c: Equal(g0,g2) = 3
    c: Block(g2)
    c: Vertical(g3)
    c: Equal(g1,g3) = 3
    c: Vertical(g4)
    c: Equal(g0,g4) = 3
    c: Block(g4)
    c: Vertical(g5)
    c: Equal(g1,g5) = 3
    c: Vertical(g6)
    c: Equal(g0,g6) = 3
    c: Block(g6)
    c: Vertical(g7)
    c: Equal(g1,g7) = 3
    c: Vertical(g8)
    c: Equal(g0,g8) = 3
    c: Block(g8)
    c: Vertical(g9)
    c: Equal(g1,g9) = 3
    c: Vertical(g10)
    c: Equal(g0,g10) = 3
    c: Block(g10)
    c: Vertical(g11)
    c: Equal(g1,g11) = 3
    c: Block(g12)
    c: Block(g13)
    c: Block(g14)
    c: Block(g15)
    c: Block(g16)
    c: Block(g17)
    c: Block(g18)
    c: Block(g19)
    c: Block(g20)
    c: Block(g21)
    c: Block(g22)
    c: Block(g23)
    c: Block(g11)
    c: Block(g9)
    c: Block(g7)
    c: Block(g5)
    c: Block(g3)
    c: Block(g1)
    c: Coincident(g24,g0)
    c: Coincident(g24,g12)
    c: Horizontal(g24)
    c: Coincident(g25,g0)
    c: Coincident(g25,g12)
    c: Horizontal(g25)
    c: Coincident(g26,g1)
    c: Coincident(g26,g13)
    c: Horizontal(g26)
    c: Coincident(g27,g1)
    c: Coincident(g27,g13)
    c: Horizontal(g27)
    c: Coincident(g28,g2)
    c: Coincident(g28,g14)
    c: Horizontal(g28)
    c: Coincident(g29,g2)
    c: Coincident(g29,g14)
    c: Horizontal(g29)
    c: Coincident(g30,g3)
    c: Coincident(g30,g15)
    c: Horizontal(g30)
    c: Coincident(g31,g3)
    c: Coincident(g31,g15)
    c: Horizontal(g31)
    c: Coincident(g32,g4)
    c: Coincident(g32,g16)
    c: Horizontal(g32)
    c: Coincident(g33,g4)
    c: Coincident(g33,g16)
    c: Horizontal(g33)
    c: Coincident(g34,g5)
    c: Coincident(g34,g17)
    c: Horizontal(g34)
    c: Coincident(g35,g5)
    c: Coincident(g35,g17)
    c: Horizontal(g35)
    c: Coincident(g36,g6)
    c: Coincident(g36,g19)
    c: Horizontal(g36)
    c: Coincident(g37,g6)
    c: Coincident(g37,g19)
    c: Horizontal(g37)
    c: Coincident(g38,g7)
    c: Coincident(g38,g18)
    c: Horizontal(g38)
    c: Coincident(g39,g7)
    c: Coincident(g39,g18)
    c: Horizontal(g39)
    c: Coincident(g40,g8)
    c: Coincident(g40,g20)
    c: Horizontal(g40)
    c: Coincident(g41,g8)
    c: Coincident(g41,g20)
    c: Horizontal(g41)
    c: Coincident(g42,g9)
    c: Coincident(g42,g23)
    c: Horizontal(g42)
    c: Coincident(g43,g9)
    c: Coincident(g43,g23)
    c: Horizontal(g43)
    c: Coincident(g44,g10)
    c: Coincident(g44,g22)
    c: Horizontal(g44)
    c: Coincident(g45,g10)
    c: Coincident(g45,g22)
    c: Horizontal(g45)
    c: Coincident(g46,g11)
    c: Coincident(g46,g21)
    c: Horizontal(g46)
    c: Coincident(g47,g11)
    c: Coincident(g47,g21)
    c: Horizontal(g47)
FEATURE [Part::Extrusion] Extrude042
  Base = -> Sketch051
  Dir = (1,-2e-16,2e-16)
  DirMode = 2
  FaceMakerClass = Part::FaceMakerBullseye
  LengthFwd = 19
  LengthRev = 0
  Placement = pos=(-19,0,0) rot=(0,0,1;0rad)
  Solid = true
  Symmetric = false
FEATURE [Part::Fillet] Fillet035  label="removeToCreateVentalationHoles"
  Base = -> Extrude042
  Edges = <same value as first occurrence — deduplicated (x4 in doc)>
  Placement = pos=(7,0,0) rot=(0,0,1;0rad)
FEATURE [Part::Cut] Cut038  label="top017"
  Base = -> Cut033
  Tool = -> Fillet035
FEATURE [Sketcher::SketchObject] Sketch052  label="bottomSketch001"
  FullyConstrained = true
  sketch-geometry (26):
    g0: LineSegment StartX=6.29999 StartY=8 StartZ=0 EndX=3.29999 EndY=8 EndZ=0
    g1: LineSegment StartX=3.29999 StartY=8 StartZ=0 EndX=3.29999 EndY=-6.03275e-07 EndZ=0
    g2: ArcOfCircle CenterX=8.29999 CenterY=5 CenterZ=0 NormalX=0 NormalY=0 NormalZ=1 AngleXU=0 Radius=2 StartAngle=3.14159 EndAngle=4.71239
    g3: LineSegment StartX=6.29999 StartY=8 StartZ=0 EndX=6.29999 EndY=5 EndZ=0
    g4: ArcOfCircle CenterX=105 CenterY=19 CenterZ=0 NormalX=0 NormalY=0 NormalZ=1 AngleXU=0 Radius=12.7 StartAngle=4.71239 EndAngle=6.28319
    g5-g11: Circle x7 (B-spline internal-alignment scaffolding for g12; pole/knot coordinates omitted)
    g12: BSplineCurve PolesCount=7 KnotsCount=5 Degree=3 IsPeriodic=0
    g13-g17: GeomPoint x5 (B-spline internal-alignment scaffolding for g12; pole/knot coordinates omitted)
    g18: ArcOfCircle CenterX=105 CenterY=19 CenterZ=0 NormalX=0 NormalY=0 NormalZ=1 AngleXU=0 Radius=15.7 StartAngle=5.81226 EndAngle=6.28319
    g19: LineSegment StartX=117.7 StartY=19 StartZ=0 EndX=120.7 EndY=19 EndZ=0
    g20: BSplineCurve PolesCount=5 KnotsCount=3 Degree=3 IsPeriodic=0
    g21: LineSegment StartX=8.29999 StartY=3 StartZ=0 EndX=101.7 EndY=3 EndZ=0
    g22: LineSegment StartX=3.29999 StartY=-6.03275e-07 StartZ=0 EndX=105 EndY=-6.03275e-07 EndZ=0
    g23: LineSegment StartX=120.974 StartY=8.71251 StartZ=0 EndX=122.332 EndY=7.83778 EndZ=0
    g24: LineSegment StartX=105 StartY=-6.03274e-07 StartZ=0 EndX=113 EndY=-6.03274e-07 EndZ=0
    g25: ArcOfCircle CenterX=105 CenterY=19 CenterZ=0 NormalX=0 NormalY=0 NormalZ=1 AngleXU=0 Radius=20.6155 StartAngle=5.11091 EndAngle=5.71103
  constraints (38):
    c: Horizontal(g0)
    c: Distance(g0) = 3
    c: Coincident(g1,g0)
    c: Vertical(g1)
    c: Block(g2)
    c: Block(g0)
    c: Coincident(g3,g0)
    c: Coincident(g3,g2)
    c: Vertical(g3)
    c: Block(g1)
    c: Block(g4)
    c: Coincident(g20,g4)
    c: Block(g20)
    c: Equal(g5, g6-g11) x6
    c: InternalAlignment(g5-g11 -> g12) x7
    c: InternalAlignment(g13-g17 -> g12) x5
    c: Block(g12)
    c: Coincident(g18,g12)
    c: Coincident(g19,g4)
    c: Coincident(g19,g18)
    c: Horizontal(g19)
    c: Block(g19)
    c: Block(g18)
    c: Coincident(g21,g2)
    c: Coincident(g21,g20)
    c: Horizontal(g21)
    c: Distance(g21) = 93.4
    c: Coincident(g22,g1)
    c: Horizontal(g22)
    c: Distance(g22) = 101.7
    c: Horizontal(g24)
    c: Distance(g24) = 8
    c: Coincident(g25,g24)
    c: Block(g24)
    c: Coincident(g23,g25)
    c: Block(g25)
    c: Block(g23)
    c: Distance(g23) = 1.61553
FEATURE [Part::Extrusion] Extrude043  label="bottom010"
  Base = -> Sketch052
  Dir = (0,0,1)
  DirMode = 2
  FaceMakerClass = Part::FaceMakerBullseye
  LengthFwd = 71.4
  LengthRev = 0
  Placement = pos=(0,0,0.3) rot=(0,0,1;0rad)
  Solid = true
  Symmetric = false
FEATURE [Sketcher::SketchObject] Sketch053  label="topSketch013"
  FullyConstrained = true
  sketch-geometry (22):
    g0: LineSegment StartX=5.21097e-06 StartY=3 StartZ=0 EndX=5.21097e-06 EndY=19 EndZ=0
    g1: ArcOfCircle CenterX=19 CenterY=19 CenterZ=0 NormalX=0 NormalY=0 NormalZ=1 AngleXU=0 Radius=19 StartAngle=1.5708 EndAngle=3.14159
    g2: ArcOfCircle CenterX=19 CenterY=19 CenterZ=0 NormalX=0 NormalY=0 NormalZ=1 AngleXU=0 Radius=16 StartAngle=1.5708 EndAngle=3.14159
    g3: LineSegment StartX=114 StartY=35 StartZ=0 EndX=19 EndY=35 EndZ=0
    g4: LineSegment StartX=5.21097e-06 StartY=3 StartZ=0 EndX=5.21097e-06 EndY=0 EndZ=0
    g5: LineSegment StartX=3 StartY=0 StartZ=0 EndX=5.21097e-06 EndY=0 EndZ=0
    g6: LineSegment StartX=3 StartY=19 StartZ=0 EndX=3 EndY=0 EndZ=0
    g7: LineSegment StartX=19 StartY=38 StartZ=0 EndX=124 EndY=38 EndZ=0
    g8: Circle CenterX=119 CenterY=35 CenterZ=0 NormalX=0 NormalY=0 NormalZ=1 AngleXU=0 Radius=1
    g9: Circle CenterX=121 CenterY=35 CenterZ=0 NormalX=0 NormalY=0 NormalZ=1 AngleXU=0 Radius=1
    g10: Circle CenterX=121 CenterY=33 CenterZ=0 NormalX=0 NormalY=0 NormalZ=1 AngleXU=0 Radius=1
    g11: BSplineCurve PolesCount=3 KnotsCount=2 Degree=2 IsPeriodic=0
    g12: GeomPoint X=119 Y=35 Z=0
    g13: GeomPoint X=121 Y=33 Z=0
    g14: LineSegment StartX=119 StartY=35 StartZ=0 EndX=114 EndY=35 EndZ=0
    g15: ArcOfCircle CenterX=105 CenterY=19 CenterZ=0 NormalX=0 NormalY=0 NormalZ=1 AngleXU=0 Radius=16 StartAngle=5.60905 EndAngle=6.28319
    g16: LineSegment StartX=121 StartY=33 StartZ=0 EndX=121 EndY=19 EndZ=0
    g17: LineSegment StartX=117.5 StartY=9.01251 StartZ=0 EndX=121.163 EndY=9.0125 EndZ=0
    g18: ArcOfCircle CenterX=105 CenterY=19 CenterZ=0 NormalX=0 NormalY=0 NormalZ=1 AngleXU=0 Radius=20.6155 StartAngle=5.7297 EndAngle=6.28319
    g19: LineSegment StartX=121.163 StartY=9.0125 StartZ=0 EndX=122.538 EndY=8.16329 EndZ=0
    g20: LineSegment StartX=124 StartY=38 StartZ=0 EndX=125.616 EndY=38 EndZ=0
    g21: LineSegment StartX=125.616 StartY=19 StartZ=0 EndX=125.616 EndY=38 EndZ=0
  constraints (50):
    c: Vertical(g0)
    c: Block(g0)
    c: Coincident(g1,g0)
    c: Block(g1)
    c: Coincident(g2,g1)
    c: Block(g2)
    c: Coincident(g3,g2)
    c: Horizontal(g3)
    c: Tangent(g3,g2)
    c: Coincident(g4,g0)
    c: Distance(g4) = 3
    c: Vertical(g4)
    c: Coincident(g5,g4)
    c: Horizontal(g5)
    c: Coincident(g6,g2)
    c: Coincident(g6,g5)
    c: Vertical(g6)
    c: Horizontal(g7)
    c: Distance(g7) = 105
    c: Coincident(g7,g1)
    c: Block(g3)
    c: Weight(g8) = 1
    c: Equal(g8,g9)
    c: Equal(g8,g10)
    c: InternalAlignment(g8,g11)
    c: InternalAlignment(g9,g11)
    c: InternalAlignment(g10,g11)
    c: InternalAlignment(g12,g11)
    c: InternalAlignment(g13,g11)
    c: Block(g11)
    c: Coincident(g14,g11)
    c: Coincident(g14,g3)
    c: Horizontal(g14)
    c: Block(g15)
    c: Coincident(g16,g11)
    c: Coincident(g16,g15)
    c: Vertical(g16)
    c: Distance(g16) = 14
    c: Coincident(g17,g15)
    c: Block(g18)
    c: Coincident(g19,g18)
    c: Coincident(g20,g7)
    c: Horizontal(g20)
    c: Vertical(g21)
    c: Coincident(g20,g21)
    c: Block(g20)
    c: Block(g21)
    c: Block(g19)
    c: Block(g17)
    c: Distance(g20) = 1.61553
FEATURE [Part::Extrusion] Extrude044
  Base = -> Sketch053
  Dir = (0,0,1)
  DirMode = 2
  FaceMakerClass = Part::FaceMakerBullseye
  LengthFwd = 72
  LengthRev = 0
  Solid = true
  Symmetric = false
FEATURE [Part::Fillet] Fillet036  label="top018"
  Base = -> Extrude044
  Edges = 1 edges r=2: [Edge41]
FEATURE [Part::Fillet] Fillet037  label="bottom011"
  Base = -> Extrude043
  Edges = 1 edges r=2.4: [Edge26]
FEATURE [Sketcher::SketchObject] Sketch054
  FullyConstrained = false
  Placement = pos=(0,0,0) rot=(1,0,0;1.5708rad)
  sketch-geometry (24):
    g0: ArcOfCircle CenterX=-4 CenterY=-10.5 CenterZ=0 NormalX=0 NormalY=0 NormalZ=1 AngleXU=0 Radius=1.5 StartAngle=6e-16 EndAngle=3.14159
    g1: ArcOfCircle CenterX=-34.2 CenterY=-10.5 CenterZ=0 NormalX=0 NormalY=0 NormalZ=1 AngleXU=0 Radius=1.5 StartAngle=0 EndAngle=3.14159
    g2: ArcOfCircle CenterX=-34.2 CenterY=-27.7 CenterZ=0 NormalX=0 NormalY=0 NormalZ=1 AngleXU=0 Radius=1.5 StartAngle=3.14159 EndAngle=6.28319
    g3: ArcOfCircle CenterX=-4 CenterY=-27.7 CenterZ=0 NormalX=0 NormalY=0 NormalZ=1 AngleXU=0 Radius=1.5 StartAngle=3.1416 EndAngle=6.28319
    g4: ArcOfCircle CenterX=-10 CenterY=-4.3 CenterZ=0 NormalX=0 NormalY=0 NormalZ=1 AngleXU=0 Radius=1.5 StartAngle=2e-16 EndAngle=3.14159
    g5: ArcOfCircle CenterX=-16.1 CenterY=-1.8 CenterZ=0 NormalX=0 NormalY=0 NormalZ=1 AngleXU=0 Radius=1.5 StartAngle=5e-16 EndAngle=3.14159
    g6: ArcOfCircle CenterX=-22.1 CenterY=-1.8 CenterZ=0 NormalX=0 NormalY=0 NormalZ=1 AngleXU=0 Radius=1.5 StartAngle=5e-16 EndAngle=3.14159
    g7: ArcOfCircle CenterX=-28.2 CenterY=-4.3 CenterZ=0 NormalX=0 NormalY=0 NormalZ=1 AngleXU=0 Radius=1.5 StartAngle=2e-16 EndAngle=3.14159
    g8: ArcOfCircle CenterX=-10 CenterY=-33.9 CenterZ=0 NormalX=0 NormalY=0 NormalZ=1 AngleXU=0 Radius=1.5 StartAngle=3.14159 EndAngle=6.28319
    g9: ArcOfCircle CenterX=-16.1 CenterY=-36.4 CenterZ=0 NormalX=0 NormalY=0 NormalZ=1 AngleXU=0 Radius=1.5 StartAngle=3.14159 EndAngle=6.28319
    g10: ArcOfCircle CenterX=-22.1 CenterY=-36.4 CenterZ=0 NormalX=0 NormalY=0 NormalZ=1 AngleXU=0 Radius=1.5 StartAngle=3.14159 EndAngle=6.28319
    g11: ArcOfCircle CenterX=-28.2 CenterY=-33.9 CenterZ=0 NormalX=0 NormalY=0 NormalZ=1 AngleXU=0 Radius=1.5 StartAngle=3.14159 EndAngle=6.28319
    g12: LineSegment StartX=-35.7 StartY=-10.5 StartZ=0 EndX=-35.7 EndY=-27.7 EndZ=0
    g13: LineSegment StartX=-32.7 StartY=-10.5 StartZ=0 EndX=-32.7 EndY=-27.7 EndZ=0
    g14: LineSegment StartX=-29.7 StartY=-33.9 StartZ=0 EndX=-29.7 EndY=-4.3 EndZ=0
    g15: LineSegment StartX=-26.7 StartY=-33.9 StartZ=0 EndX=-26.7 EndY=-4.3 EndZ=0
    g16: LineSegment StartX=-2.5 StartY=-10.5 StartZ=0 EndX=-2.5 EndY=-27.7 EndZ=0
    g17: LineSegment StartX=-8.5 StartY=-4.3 StartZ=0 EndX=-8.5 EndY=-33.9 EndZ=0
    g18: LineSegment StartX=-5.5 StartY=-10.5 StartZ=0 EndX=-5.5 EndY=-27.7 EndZ=0
    g19: LineSegment StartX=-11.5 StartY=-4.3 StartZ=0 EndX=-11.5 EndY=-33.9 EndZ=0
    g20: LineSegment StartX=-14.6 StartY=-1.8 StartZ=0 EndX=-14.6 EndY=-36.4 EndZ=0
    g21: LineSegment StartX=-17.6 StartY=-1.8 StartZ=0 EndX=-17.6 EndY=-36.4 EndZ=0
    g22: LineSegment StartX=-20.6 StartY=-36.4 StartZ=0 EndX=-20.6 EndY=-1.8 EndZ=0
    g23: LineSegment StartX=-23.6 StartY=-1.8 StartZ=0 EndX=-23.6 EndY=-36.4 EndZ=0
  constraints (48):
    c: Block(g0)
    c: Block(g1)
    c: Block(g2)
    c: Block(g3)
    c: Block(g4)
    c: Block(g5)
    c: Block(g6)
    c: Block(g7)
    c: Block(g8)
    c: Block(g9)
    c: Block(g10)
    c: Block(g11)
    c: Coincident(g12,g1)
    c: Coincident(g12,g2)
    c: Vertical(g12)
    c: Coincident(g13,g1)
    c: Coincident(g13,g2)
    c: Vertical(g13)
    c: Coincident(g14,g11)
    c: Coincident(g14,g7)
    c: Vertical(g14)
    c: Coincident(g15,g11)
    c: Coincident(g15,g7)
    c: Vertical(g15)
    c: Coincident(g16,g0)
    c: Coincident(g16,g3)
    c: Vertical(g16)
    c: Coincident(g17,g4)
    c: Coincident(g17,g8)
    c: Vertical(g17)
    c: Coincident(g18,g0)
    c: Coincident(g18,g3)
    c: Vertical(g18)
    c: Coincident(g19,g4)
    c: Coincident(g19,g8)
    c: Vertical(g19)
    c: Coincident(g20,g5)
    c: Coincident(g20,g9)
    c: Vertical(g20)
    c: Coincident(g21,g5)
    c: Coincident(g21,g9)
    c: Vertical(g21)
    c: Coincident(g22,g10)
    c: Coincident(g22,g6)
    c: Vertical(g22)
    c: Coincident(g23,g6)
    c: Coincident(g23,g10)
    c: Vertical(g23)
FEATURE [Part::Extrusion] Extrude045  label="removeToCreateFanGrillHoles003"
  Base = -> Sketch054
  Dir = (0,-1,6e-16)
  DirMode = 2
  FaceMakerClass = Part::FaceMakerBullseye
  LengthFwd = 10
  LengthRev = 0
  Placement = pos=(65.4,44,54.82) rot=(0,0,1;0rad)
  Solid = true
  Symmetric = false
FEATURE [Part::Feature] Face105 .. Face108  x4 (patterned run collapsed; names and placements below)
  shape: bbox 3.5 x 17.8 x 2e-07 mm, 1 faces, 0 solids (baked)
FEATURE [Part::Revolution] Revolve113  label="removeToCreateScrewAndThreadedInsertHole041"
  Angle = 360
  Axis = (0,1,0)
  Base = (0,0,0)
  FaceMakerClass = Part::FaceMakerBullseye
  Placement = pos=(62.3,30.3,19.7) rot=(0,0,1;0rad)
  Solid = false
  Source = -> Face105
  Symmetric = false
FEATURE [Part::Revolution] Revolve114  label="removeToCreateScrewAndThreadedInsertHole042"
  Angle = 360
  Axis = (0,1,0)
  Base = (0,0,0)
  FaceMakerClass = Part::FaceMakerBullseye
  Placement = pos=(62.3,30.3,51.7) rot=(0,0,1;0rad)
  Solid = false
  Source = -> Face106
  Symmetric = false
FEATURE [Part::Revolution] Revolve115  label="removeToCreateScrewAndThreadedInsertHole043"
  Angle = 360
  Axis = (0,1,0)
  Base = (0,0,0)
  FaceMakerClass = Part::FaceMakerBullseye
  Placement = pos=(30.3,30.3,19.7) rot=(0,0,1;0rad)
  Solid = false
  Source = -> Face107
  Symmetric = false
FEATURE [Part::Revolution] Revolve116  label="removeToCreateScrewAndThreadedInsertHole044"
  Angle = 360
  Axis = (0,1,0)
  Base = (0,0,0)
  FaceMakerClass = Part::FaceMakerBullseye
  Placement = pos=(30.3,30.3,51.7) rot=(0,0,1;0rad)
  Solid = false
  Source = -> Face108
  Symmetric = false
FEATURE [Part::MultiFuse] Fusion083  label="createThreadedInsertHolesForFan004"
  Shapes = -> [Revolve113,Revolve114,Revolve115,Revolve116]
FEATURE [Part::Box] Box024  label="removeToCreteHoleForPlugHousing026"
  AttacherType = Attacher::AttachEngine3D
  Height = 28.6
  Length = 10
  Placement = pos=(-2,0,21.7) rot=(0,0,1;0rad)
  Width = 19
FEATURE [Part::Cylinder] Cylinder038  label="removeToCreteHoleForPlugHousing027"
  Angle = 360
  AttacherType = Attacher::AttachEngine3D
  Height = 20
  Placement = pos=(-2,19,36) rot=(0,1,0;1.5708rad)
  Radius = 14.3
FEATURE [Part::MultiFuse] Fusion084  label="removeToCreteHoleForPlugHousing028"
  Shapes = -> [Box024,Cylinder038]
FEATURE [Part::Cylinder] Cylinder039
  Angle = 360
  AttacherType = Attacher::AttachEngine3D
  Height = 20
  Placement = pos=(0,0,36.15) rot=(0,0,1;0rad)
  Radius = 14.3
FEATURE [Part::Cylinder] Cylinder040
  Angle = 360
  AttacherType = Attacher::AttachEngine3D
  Height = 10
  Placement = pos=(0,0,36.15) rot=(0,0,1;0rad)
  Radius = 4
FEATURE [Part::Box] Box025  label="removeToCreteHoleForPlugHousing030"
  AttacherType = Attacher::AttachEngine3D
  Height = 28.6
  Length = 20
  Placement = pos=(106.15,0,21.7) rot=(0,0,1;0rad)
  Width = 19
FEATURE [Part::MultiFuse] Fusion086  label="removeToCreteHoleForPlugHousing031"
  Placement = pos=(70,19,36) rot=(0,1,0;1.5708rad)
  Shapes = -> [Cylinder039,Cylinder040]
FEATURE [Part::MultiFuse] Fusion085  label="removeToCreteHoleForPlugHousing029"
  Shapes = -> [Box025,Fusion086]
FEATURE [Sketcher::SketchObject] Sketch055
  FullyConstrained = true
  Placement = pos=(117,19,0) rot=(0.57735,0.57735,0.57735;2.0944rad)
  sketch-geometry (48):
    g0: LineSegment StartX=-49.19 StartY=69.25 StartZ=0 EndX=-49.19 EndY=66.25 EndZ=0
    g1: LineSegment StartX=-49.19 StartY=63.5 StartZ=0 EndX=-49.19 EndY=60.5 EndZ=0
    g2: LineSegment StartX=-49.19 StartY=57.75 StartZ=0 EndX=-49.19 EndY=54.75 EndZ=0
    g3: LineSegment StartX=-49.19 StartY=52 StartZ=0 EndX=-49.19 EndY=49 EndZ=0
    g4: LineSegment StartX=-49.19 StartY=46.25 StartZ=0 EndX=-49.19 EndY=43.25 EndZ=0
    g5: LineSegment StartX=-49.19 StartY=40.5 StartZ=0 EndX=-49.19 EndY=37.5 EndZ=0
    g6: LineSegment StartX=-49.19 StartY=34.5 StartZ=0 EndX=-49.19 EndY=31.5 EndZ=0
    g7: LineSegment StartX=-49.19 StartY=28.75 StartZ=0 EndX=-49.19 EndY=25.75 EndZ=0
    g8: LineSegment StartX=-49.19 StartY=23 StartZ=0 EndX=-49.19 EndY=20 EndZ=0
    g9: LineSegment StartX=-49.19 StartY=17.25 StartZ=0 EndX=-49.19 EndY=14.25 EndZ=0
    g10: LineSegment StartX=-49.19 StartY=11.5 StartZ=0 EndX=-49.19 EndY=8.5 EndZ=0
    g11: LineSegment StartX=-49.19 StartY=5.75 StartZ=0 EndX=-49.19 EndY=2.75 EndZ=0
    g12: ArcOfCircle CenterX=-1.5 CenterY=67.75 CenterZ=0 NormalX=0 NormalY=0 NormalZ=1 AngleXU=0 Radius=1.5 StartAngle=4.71239 EndAngle=7.85398
    g13: ArcOfCircle CenterX=-1.5 CenterY=62 CenterZ=0 NormalX=0 NormalY=0 NormalZ=1 AngleXU=0 Radius=1.5 StartAngle=4.71239 EndAngle=7.85398
    g14: ArcOfCircle CenterX=-1.5 CenterY=56.25 CenterZ=0 NormalX=0 NormalY=0 NormalZ=1 AngleXU=0 Radius=1.5 StartAngle=4.71239 EndAngle=7.85398
    g15: ArcOfCircle CenterX=-11.49 CenterY=50.5 CenterZ=0 NormalX=0 NormalY=0 NormalZ=1 AngleXU=0 Radius=1.5 StartAngle=4.71239 EndAngle=7.85398
    g16: ArcOfCircle CenterX=-16.28 CenterY=44.75 CenterZ=0 NormalX=0 NormalY=0 NormalZ=1 AngleXU=0 Radius=1.5 StartAngle=4.71239 EndAngle=7.85398
    g17: ArcOfCircle CenterX=-18.2337 CenterY=39 CenterZ=0 NormalX=0 NormalY=0 NormalZ=1 AngleXU=0 Radius=1.5 StartAngle=4.71485 EndAngle=7.85398
    g18: ArcOfCircle CenterX=-16.2837 CenterY=27.25 CenterZ=0 NormalX=0 NormalY=0 NormalZ=1 AngleXU=0 Radius=1.5 StartAngle=4.71485 EndAngle=7.85398
    g19: ArcOfCircle CenterX=-18.2337 CenterY=33 CenterZ=0 NormalX=0 NormalY=0 NormalZ=1 AngleXU=0 Radius=1.5 StartAngle=4.71485 EndAngle=7.85398
    g20: ArcOfCircle CenterX=-11.49 CenterY=21.5 CenterZ=0 NormalX=0 NormalY=0 NormalZ=1 AngleXU=0 Radius=1.5 StartAngle=4.71239 EndAngle=7.85398
    g21: ArcOfCircle CenterX=-1.5 CenterY=4.25 CenterZ=0 NormalX=0 NormalY=0 NormalZ=1 AngleXU=0 Radius=1.5 StartAngle=4.71239 EndAngle=7.85398
    g22: ArcOfCircle CenterX=-1.5 CenterY=10 CenterZ=0 NormalX=0 NormalY=0 NormalZ=1 AngleXU=0 Radius=1.5 StartAngle=4.71239 EndAngle=7.85398
    g23: ArcOfCircle CenterX=-1.5 CenterY=15.75 CenterZ=0 NormalX=0 NormalY=0 NormalZ=1 AngleXU=0 Radius=1.5 StartAngle=4.71239 EndAngle=7.85398
    g24: LineSegment StartX=-49.19 StartY=69.25 StartZ=0 EndX=-1.5 EndY=69.25 EndZ=0
    g25: LineSegment StartX=-49.19 StartY=66.25 StartZ=0 EndX=-1.5 EndY=66.25 EndZ=0
    g26: LineSegment StartX=-49.19 StartY=63.5 StartZ=0 EndX=-1.5 EndY=63.5 EndZ=0
    g27: LineSegment StartX=-49.19 StartY=60.5 StartZ=0 EndX=-1.5 EndY=60.5 EndZ=0
    g28: LineSegment StartX=-49.19 StartY=57.75 StartZ=0 EndX=-1.5 EndY=57.75 EndZ=0
    g29: LineSegment StartX=-49.19 StartY=54.75 StartZ=0 EndX=-1.5 EndY=54.75 EndZ=0
    g30: LineSegment StartX=-49.19 StartY=52 StartZ=0 EndX=-11.49 EndY=52 EndZ=0
    g31: LineSegment StartX=-49.19 StartY=49 StartZ=0 EndX=-11.49 EndY=49 EndZ=0
    g32: LineSegment StartX=-49.19 StartY=46.25 StartZ=0 EndX=-16.28 EndY=46.25 EndZ=0
    g33: LineSegment StartX=-49.19 StartY=43.25 StartZ=0 EndX=-16.28 EndY=43.25 EndZ=0
    g34: LineSegment StartX=-49.19 StartY=40.5 StartZ=0 EndX=-18.2337 EndY=40.5 EndZ=0
    g35: LineSegment StartX=-49.19 StartY=37.5 StartZ=0 EndX=-18.23 EndY=37.5 EndZ=0
    g36: LineSegment StartX=-49.19 StartY=34.5 StartZ=0 EndX=-18.2337 EndY=34.5 EndZ=0
    g37: LineSegment StartX=-49.19 StartY=31.5 StartZ=0 EndX=-18.23 EndY=31.5 EndZ=0
    g38: LineSegment StartX=-49.19 StartY=28.75 StartZ=0 EndX=-16.2837 EndY=28.75 EndZ=0
    g39: LineSegment StartX=-49.19 StartY=25.75 StartZ=0 EndX=-16.28 EndY=25.75 EndZ=0
    g40: LineSegment StartX=-49.19 StartY=23 StartZ=0 EndX=-11.49 EndY=23 EndZ=0
    g41: LineSegment StartX=-49.19 StartY=20 StartZ=0 EndX=-11.49 EndY=20 EndZ=0
    g42: LineSegment StartX=-49.19 StartY=17.25 StartZ=0 EndX=-1.5 EndY=17.25 EndZ=0
    g43: LineSegment StartX=-49.19 StartY=14.25 StartZ=0 EndX=-1.5 EndY=14.25 EndZ=0
    g44: LineSegment StartX=-49.19 StartY=11.5 StartZ=0 EndX=-1.5 EndY=11.5 EndZ=0
    g45: LineSegment StartX=-49.19 StartY=8.5 StartZ=0 EndX=-1.5 EndY=8.5 EndZ=0
    g46: LineSegment StartX=-49.19 StartY=5.75 StartZ=0 EndX=-1.5 EndY=5.75 EndZ=0
    g47: LineSegment StartX=-49.19 StartY=2.75 StartZ=0 EndX=-1.5 EndY=2.75 EndZ=0
  constraints (120):
    c: Vertical(g0)
    c: Distance(g0) = 3
    c: Block(g0)
    c: Vertical(g1)
    c: Distance(g1) = 3
    c: Vertical(g2)
    c: Equal(g0,g2) = 3
    c: Block(g2)
    c: Vertical(g3)
    c: Equal(g1,g3) = 3
    c: Vertical(g4)
    c: Equal(g0,g4) = 3
    c: Block(g4)
    c: Vertical(g5)
    c: Equal(g1,g5) = 3
    c: Vertical(g6)
    c: Equal(g0,g6) = 3
    c: Block(g6)
    c: Vertical(g7)
    c: Equal(g1,g7) = 3
    c: Vertical(g8)
    c: Equal(g0,g8) = 3
    c: Block(g8)
    c: Vertical(g9)
    c: Equal(g1,g9) = 3
    c: Vertical(g10)
    c: Equal(g0,g10) = 3
    c: Block(g10)
    c: Vertical(g11)
    c: Equal(g1,g11) = 3
    c: Block(g12)
    c: Block(g13)
    c: Block(g14)
    c: Block(g15)
    c: Block(g16)
    c: Block(g17)
    c: Block(g18)
    c: Block(g19)
    c: Block(g20)
    c: Block(g21)
    c: Block(g22)
    c: Block(g23)
    c: Block(g11)
    c: Block(g9)
    c: Block(g7)
    c: Block(g5)
    c: Block(g3)
    c: Block(g1)
    c: Coincident(g24,g0)
    c: Coincident(g24,g12)
    c: Horizontal(g24)
    c: Coincident(g25,g0)
    c: Coincident(g25,g12)
    c: Horizontal(g25)
    c: Coincident(g26,g1)
    c: Coincident(g26,g13)
    c: Horizontal(g26)
    c: Coincident(g27,g1)
    c: Coincident(g27,g13)
    c: Horizontal(g27)
    c: Coincident(g28,g2)
    c: Coincident(g28,g14)
    c: Horizontal(g28)
    c: Coincident(g29,g2)
    c: Coincident(g29,g14)
    c: Horizontal(g29)
    c: Coincident(g30,g3)
    c: Coincident(g30,g15)
    c: Horizontal(g30)
    c: Coincident(g31,g3)
    c: Coincident(g31,g15)
    c: Horizontal(g31)
    c: Coincident(g32,g4)
    c: Coincident(g32,g16)
    c: Horizontal(g32)
    c: Coincident(g33,g4)
    c: Coincident(g33,g16)
    c: Horizontal(g33)
    c: Coincident(g34,g5)
    c: Coincident(g34,g17)
    c: Horizontal(g34)
    c: Coincident(g35,g5)
    c: Coincident(g35,g17)
    c: Horizontal(g35)
    c: Coincident(g36,g6)
    c: Coincident(g36,g19)
    c: Horizontal(g36)
    c: Coincident(g37,g6)
    c: Coincident(g37,g19)
    c: Horizontal(g37)
    c: Coincident(g38,g7)
    c: Coincident(g38,g18)
    c: Horizontal(g38)
    c: Coincident(g39,g7)
    c: Coincident(g39,g18)
    c: Horizontal(g39)
    c: Coincident(g40,g8)
    c: Coincident(g40,g20)
    c: Horizontal(g40)
    c: Coincident(g41,g8)
    c: Coincident(g41,g20)
    c: Horizontal(g41)
    c: Coincident(g42,g9)
    c: Coincident(g42,g23)
    c: Horizontal(g42)
    c: Coincident(g43,g9)
    c: Coincident(g43,g23)
    c: Horizontal(g43)
    c: Coincident(g44,g10)
    c: Coincident(g44,g22)
    c: Horizontal(g44)
    c: Coincident(g45,g10)
    c: Coincident(g45,g22)
    c: Horizontal(g45)
    c: Coincident(g46,g11)
    c: Coincident(g46,g21)
    c: Horizontal(g46)
    c: Coincident(g47,g11)
    c: Coincident(g47,g21)
    c: Horizontal(g47)
FEATURE [Part::Extrusion] Extrude046
  Base = -> Sketch055
  Dir = (1,0,0)
  DirMode = 2
  FaceMakerClass = Part::FaceMakerBullseye
  LengthFwd = 23
  LengthRev = 0
  Placement = pos=(-19,0,0) rot=(0,0,1;0rad)
  Solid = true
  Symmetric = false
FEATURE [Part::Fillet] Fillet038  label="removeToCreateVentalationHoles001"
  Base = -> Extrude046
  Edges = <same value as first occurrence — deduplicated (x4 in doc)>
  Placement = pos=(7,0,0) rot=(0,0,1;0rad)
FEATURE [Sketcher::SketchObject] Sketch056  label="topSketch014"
  FullyConstrained = true
  sketch-geometry (22):
    g0: LineSegment StartX=5.21097e-06 StartY=3 StartZ=0 EndX=5.21097e-06 EndY=19 EndZ=0
    g1: ArcOfCircle CenterX=19 CenterY=19 CenterZ=0 NormalX=0 NormalY=0 NormalZ=1 AngleXU=0 Radius=19 StartAngle=1.5708 EndAngle=3.14159
    g2: ArcOfCircle CenterX=19 CenterY=19 CenterZ=0 NormalX=0 NormalY=0 NormalZ=1 AngleXU=0 Radius=16 StartAngle=1.5708 EndAngle=3.14159
    g3: LineSegment StartX=114 StartY=35 StartZ=0 EndX=19 EndY=35 EndZ=0
    g4: LineSegment StartX=5.21097e-06 StartY=3 StartZ=0 EndX=5.21097e-06 EndY=0 EndZ=0
    g5: LineSegment StartX=3 StartY=0 StartZ=0 EndX=5.21097e-06 EndY=0 EndZ=0
    g6: LineSegment StartX=3 StartY=19 StartZ=0 EndX=3 EndY=0 EndZ=0
    g7: LineSegment StartX=19 StartY=38 StartZ=0 EndX=124 EndY=38 EndZ=0
    g8: Circle CenterX=119 CenterY=35 CenterZ=0 NormalX=0 NormalY=0 NormalZ=1 AngleXU=0 Radius=1
    g9: Circle CenterX=121 CenterY=35 CenterZ=0 NormalX=0 NormalY=0 NormalZ=1 AngleXU=0 Radius=1
    g10: Circle CenterX=121 CenterY=33 CenterZ=0 NormalX=0 NormalY=0 NormalZ=1 AngleXU=0 Radius=1
    g11: BSplineCurve PolesCount=3 KnotsCount=2 Degree=2 IsPeriodic=0
    g12: GeomPoint X=119 Y=35 Z=0
    g13: GeomPoint X=121 Y=33 Z=0
    g14: LineSegment StartX=119 StartY=35 StartZ=0 EndX=114 EndY=35 EndZ=0
    g15: ArcOfCircle CenterX=105 CenterY=19 CenterZ=0 NormalX=0 NormalY=0 NormalZ=1 AngleXU=0 Radius=16 StartAngle=5.60905 EndAngle=6.28319
    g16: LineSegment StartX=121 StartY=33 StartZ=0 EndX=121 EndY=19 EndZ=0
    g17: LineSegment StartX=117.5 StartY=9.01251 StartZ=0 EndX=121.163 EndY=9.0125 EndZ=0
    g18: ArcOfCircle CenterX=105 CenterY=19 CenterZ=0 NormalX=0 NormalY=0 NormalZ=1 AngleXU=0 Radius=20.6155 StartAngle=5.7297 EndAngle=6.28319
    g19: LineSegment StartX=121.163 StartY=9.0125 StartZ=0 EndX=122.538 EndY=8.16329 EndZ=0
    g20: LineSegment StartX=124 StartY=38 StartZ=0 EndX=125.616 EndY=38 EndZ=0
    g21: LineSegment StartX=125.616 StartY=19 StartZ=0 EndX=125.616 EndY=38 EndZ=0
  constraints (49):
    c: Vertical(g0)
    c: Block(g0)
    c: Coincident(g1,g0)
    c: Block(g1)
    c: Coincident(g2,g1)
    c: Block(g2)
    c: Coincident(g3,g2)
    c: Horizontal(g3)
    c: Tangent(g3,g2)
    c: Coincident(g4,g0)
    c: Distance(g4) = 3
    c: Vertical(g4)
    c: Coincident(g5,g4)
    c: Horizontal(g5)
    c: Coincident(g6,g2)
    c: Coincident(g6,g5)
    c: Vertical(g6)
    c: Horizontal(g7)
    c: Distance(g7) = 105
    c: Coincident(g7,g1)
    c: Block(g3)
    c: Weight(g8) = 1
    c: Equal(g8,g9)
    c: Equal(g8,g10)
    c: InternalAlignment(g8,g11)
    c: InternalAlignment(g9,g11)
    c: InternalAlignment(g10,g11)
    c: InternalAlignment(g12,g11)
    c: InternalAlignment(g13,g11)
    c: Block(g11)
    c: Coincident(g14,g11)
    c: Coincident(g14,g3)
    c: Horizontal(g14)
    c: Block(g15)
    c: Coincident(g16,g11)
    c: Coincident(g16,g15)
    c: Vertical(g16)
    c: Distance(g16) = 14
    c: Coincident(g17,g15)
    c: Block(g18)
    c: Coincident(g19,g18)
    c: Coincident(g20,g7)
    c: Horizontal(g20)
    c: Vertical(g21)
    c: Coincident(g20,g21)
    c: Block(g20)
    c: Block(g21)
    c: Block(g19)
    c: Block(g17)
FEATURE [Part::Box] Box026  label="removeToCreteHoleForPlugHousing032"
  AttacherType = Attacher::AttachEngine3D
  Height = 28.6
  Length = 10
  Placement = pos=(-2,0,21.7) rot=(0,0,1;0rad)
  Width = 19
FEATURE [Part::Feature] Face109 .. Face112  x4 (patterned run collapsed; names and placements below)
  shape: bbox 3.5 x 17.8 x 2e-07 mm, 1 faces, 0 solids (baked)
FEATURE [Part::Revolution] Revolve117  label="removeToCreateScrewAndThreadedInsertHole045"
  Angle = 360
  Axis = (0,1,0)
  Base = (0,0,0)
  FaceMakerClass = Part::FaceMakerBullseye
  Placement = pos=(62.3,30.3,19.7) rot=(0,0,1;0rad)
  Solid = false
  Source = -> Face109
  Symmetric = false
FEATURE [Part::Revolution] Revolve118  label="removeToCreateScrewAndThreadedInsertHole046"
  Angle = 360
  Axis = (0,1,0)
  Base = (0,0,0)
  FaceMakerClass = Part::FaceMakerBullseye
  Placement = pos=(62.3,30.3,51.7) rot=(0,0,1;0rad)
  Solid = false
  Source = -> Face110
  Symmetric = false
FEATURE [Part::Revolution] Revolve119  label="removeToCreateScrewAndThreadedInsertHole047"
  Angle = 360
  Axis = (0,1,0)
  Base = (0,0,0)
  FaceMakerClass = Part::FaceMakerBullseye
  Placement = pos=(30.3,30.3,19.7) rot=(0,0,1;0rad)
  Solid = false
  Source = -> Face111
  Symmetric = false
FEATURE [Part::Revolution] Revolve120  label="removeToCreateScrewAndThreadedInsertHole048"
  Angle = 360
  Axis = (0,1,0)
  Base = (0,0,0)
  FaceMakerClass = Part::FaceMakerBullseye
  Placement = pos=(30.3,30.3,51.7) rot=(0,0,1;0rad)
  Solid = false
  Source = -> Face112
  Symmetric = false
FEATURE [Part::MultiFuse] Fusion087  label="createThreadedInsertHolesForFan005"
  Shapes = -> [Revolve117,Revolve118,Revolve119,Revolve120]
FEATURE [Part::Extrusion] Extrude047
  Base = -> Sketch056
  Dir = (0,0,1)
  DirMode = 2
  FaceMakerClass = Part::FaceMakerBullseye
  LengthFwd = 72
  LengthRev = 0
  Solid = true
  Symmetric = false
FEATURE [Part::Fillet] Fillet039  label="top019"
  Base = -> Extrude047
  Edges = 1 edges r=2: [Edge35]
FEATURE [Sketcher::SketchObject] Sketch057
  FullyConstrained = false
  Placement = pos=(0,0,0) rot=(1,0,0;1.5708rad)
  sketch-geometry (24):
    g0: ArcOfCircle CenterX=-4 CenterY=-10.5 CenterZ=0 NormalX=0 NormalY=0 NormalZ=1 AngleXU=0 Radius=1.5 StartAngle=6e-16 EndAngle=3.14159
    g1: ArcOfCircle CenterX=-34.2 CenterY=-10.5 CenterZ=0 NormalX=0 NormalY=0 NormalZ=1 AngleXU=0 Radius=1.5 StartAngle=0 EndAngle=3.14159
    g2: ArcOfCircle CenterX=-34.2 CenterY=-27.7 CenterZ=0 NormalX=0 NormalY=0 NormalZ=1 AngleXU=0 Radius=1.5 StartAngle=3.14159 EndAngle=6.28319
    g3: ArcOfCircle CenterX=-4 CenterY=-27.7 CenterZ=0 NormalX=0 NormalY=0 NormalZ=1 AngleXU=0 Radius=1.5 StartAngle=3.1416 EndAngle=6.28319
    g4: ArcOfCircle CenterX=-10 CenterY=-4.3 CenterZ=0 NormalX=0 NormalY=0 NormalZ=1 AngleXU=0 Radius=1.5 StartAngle=2e-16 EndAngle=3.14159
    g5: ArcOfCircle CenterX=-16.1 CenterY=-1.8 CenterZ=0 NormalX=0 NormalY=0 NormalZ=1 AngleXU=0 Radius=1.5 StartAngle=5e-16 EndAngle=3.14159
    g6: ArcOfCircle CenterX=-22.1 CenterY=-1.8 CenterZ=0 NormalX=0 NormalY=0 NormalZ=1 AngleXU=0 Radius=1.5 StartAngle=5e-16 EndAngle=3.14159
    g7: ArcOfCircle CenterX=-28.2 CenterY=-4.3 CenterZ=0 NormalX=0 NormalY=0 NormalZ=1 AngleXU=0 Radius=1.5 StartAngle=2e-16 EndAngle=3.14159
    g8: ArcOfCircle CenterX=-10 CenterY=-33.9 CenterZ=0 NormalX=0 NormalY=0 NormalZ=1 AngleXU=0 Radius=1.5 StartAngle=3.14159 EndAngle=6.28319
    g9: ArcOfCircle CenterX=-16.1 CenterY=-36.4 CenterZ=0 NormalX=0 NormalY=0 NormalZ=1 AngleXU=0 Radius=1.5 StartAngle=3.14159 EndAngle=6.28319
    g10: ArcOfCircle CenterX=-22.1 CenterY=-36.4 CenterZ=0 NormalX=0 NormalY=0 NormalZ=1 AngleXU=0 Radius=1.5 StartAngle=3.14159 EndAngle=6.28319
    g11: ArcOfCircle CenterX=-28.2 CenterY=-33.9 CenterZ=0 NormalX=0 NormalY=0 NormalZ=1 AngleXU=0 Radius=1.5 StartAngle=3.14159 EndAngle=6.28319
    g12: LineSegment StartX=-35.7 StartY=-10.5 StartZ=0 EndX=-35.7 EndY=-27.7 EndZ=0
    g13: LineSegment StartX=-32.7 StartY=-10.5 StartZ=0 EndX=-32.7 EndY=-27.7 EndZ=0
    g14: LineSegment StartX=-29.7 StartY=-33.9 StartZ=0 EndX=-29.7 EndY=-4.3 EndZ=0
    g15: LineSegment StartX=-26.7 StartY=-33.9 StartZ=0 EndX=-26.7 EndY=-4.3 EndZ=0
    g16: LineSegment StartX=-2.5 StartY=-10.5 StartZ=0 EndX=-2.5 EndY=-27.7 EndZ=0
    g17: LineSegment StartX=-8.5 StartY=-4.3 StartZ=0 EndX=-8.5 EndY=-33.9 EndZ=0
    g18: LineSegment StartX=-5.5 StartY=-10.5 StartZ=0 EndX=-5.5 EndY=-27.7 EndZ=0
    g19: LineSegment StartX=-11.5 StartY=-4.3 StartZ=0 EndX=-11.5 EndY=-33.9 EndZ=0
    g20: LineSegment StartX=-14.6 StartY=-1.8 StartZ=0 EndX=-14.6 EndY=-36.4 EndZ=0
    g21: LineSegment StartX=-17.6 StartY=-1.8 StartZ=0 EndX=-17.6 EndY=-36.4 EndZ=0
    g22: LineSegment StartX=-20.6 StartY=-36.4 StartZ=0 EndX=-20.6 EndY=-1.8 EndZ=0
    g23: LineSegment StartX=-23.6 StartY=-1.8 StartZ=0 EndX=-23.6 EndY=-36.4 EndZ=0
  constraints (48):
    c: Block(g0)
    c: Block(g1)
    c: Block(g2)
    c: Block(g3)
    c: Block(g4)
    c: Block(g5)
    c: Block(g6)
    c: Block(g7)
    c: Block(g8)
    c: Block(g9)
    c: Block(g10)
    c: Block(g11)
    c: Coincident(g12,g1)
    c: Coincident(g12,g2)
    c: Vertical(g12)
    c: Coincident(g13,g1)
    c: Coincident(g13,g2)
    c: Vertical(g13)
    c: Coincident(g14,g11)
    c: Coincident(g14,g7)
    c: Vertical(g14)
    c: Coincident(g15,g11)
    c: Coincident(g15,g7)
    c: Vertical(g15)
    c: Coincident(g16,g0)
    c: Coincident(g16,g3)
    c: Vertical(g16)
    c: Coincident(g17,g4)
    c: Coincident(g17,g8)
    c: Vertical(g17)
    c: Coincident(g18,g0)
    c: Coincident(g18,g3)
    c: Vertical(g18)
    c: Coincident(g19,g4)
    c: Coincident(g19,g8)
    c: Vertical(g19)
    c: Coincident(g20,g5)
    c: Coincident(g20,g9)
    c: Vertical(g20)
    c: Coincident(g21,g5)
    c: Coincident(g21,g9)
    c: Vertical(g21)
    c: Coincident(g22,g10)
    c: Coincident(g22,g6)
    c: Vertical(g22)
    c: Coincident(g23,g6)
    c: Coincident(g23,g10)
    c: Vertical(g23)
FEATURE [Part::Extrusion] Extrude048  label="removeToCreateFanGrillHoles004"
  Base = -> Sketch057
  Dir = (0,-1,6e-16)
  DirMode = 2
  FaceMakerClass = Part::FaceMakerBullseye
  LengthFwd = 10
  LengthRev = 0
  Placement = pos=(65.4,44,54.82) rot=(0,0,1;0rad)
  Solid = true
  Symmetric = false
FEATURE [Part::Cut] Cut040  label="top021"
  Base = -> Fillet039
  Tool = -> Extrude048
FEATURE [Part::Cylinder] Cylinder041  label="removeToCreteHoleForPlugHousing034"
  Angle = 360
  AttacherType = Attacher::AttachEngine3D
  Height = 20
  Placement = pos=(-2,19,36) rot=(0,1,0;1.5708rad)
  Radius = 14.3
FEATURE [Part::MultiFuse] Fusion089  label="removeToCreteHoleForPlugHousing035"
  Shapes = -> [Box026,Cylinder041]
FEATURE [Part::Cylinder] Cylinder042
  Angle = 360
  AttacherType = Attacher::AttachEngine3D
  Height = 20
  Placement = pos=(0,0,36.15) rot=(0,0,1;0rad)
  Radius = 14.3
FEATURE [Part::Cylinder] Cylinder043
  Angle = 360
  AttacherType = Attacher::AttachEngine3D
  Height = 10
  Placement = pos=(0,0,36.15) rot=(0,0,1;0rad)
  Radius = 4
FEATURE [Part::Box] Box027  label="removeToCreteHoleForPlugHousing036"
  AttacherType = Attacher::AttachEngine3D
  Height = 28.6
  Length = 20
  Placement = pos=(106.15,0,21.7) rot=(0,0,1;0rad)
  Width = 19
FEATURE [Part::Cut] Cut041  label="top022"
  Base = -> Cut040
  Tool = -> Fusion087
FEATURE [Part::Cut] Cut039  label="top020"
  Base = -> Cut041
  Tool = -> Fusion089
FEATURE [Part::MultiFuse] Fusion090  label="removeToCreteHoleForPlugHousing037"
  Placement = pos=(70,19,36) rot=(0,1,0;1.5708rad)
  Shapes = -> [Cylinder042,Cylinder043]
FEATURE [Part::MultiFuse] Fusion088  label="removeToCreteHoleForPlugHousing033"
  Shapes = -> [Box027,Fusion090]
FEATURE [Part::Cut] Cut042  label="removeToCreteHoleForPlugHousing038"
  Base = -> Cut039
  Tool = -> Fusion088
FEATURE [Part::MultiFuse] Fusion091  label="removeFromTop"
  Shapes = -> [Fillet038,Fusion085,Fusion084,Fusion083,Extrude045]
FEATURE [Part::Cut] Cut043  label="removeToCreteHoleForPlugHousing039"
  Base = -> Fillet036
  Tool = -> Fusion091
FEATURE [Part::MultiFuse] Fusion092  label="caseScrewPillarBracket016"
  Shapes = -> [Extrude030,Extrude031,Extrude032,Extrude033,Extrude034,Extrude035,Extrude036,Extrude037,Box013,Box014]
FEATURE [Part::MultiFuse] Fusion093  label="bottom012"
  Shapes = -> [Cut034,Fillet037]
FEATURE [Sketcher::SketchObject] Sketch058  label="topSketch015"
  FullyConstrained = true
  sketch-geometry (20):
    g0: LineSegment StartX=5.21097e-06 StartY=3 StartZ=0 EndX=5.21097e-06 EndY=19 EndZ=0
    g1: ArcOfCircle CenterX=19 CenterY=19 CenterZ=0 NormalX=0 NormalY=0 NormalZ=1 AngleXU=0 Radius=19 StartAngle=1.5708 EndAngle=3.14159
    g2: ArcOfCircle CenterX=19 CenterY=19 CenterZ=0 NormalX=0 NormalY=0 NormalZ=1 AngleXU=0 Radius=16 StartAngle=1.5708 EndAngle=3.14159
    g3: LineSegment StartX=114 StartY=35 StartZ=0 EndX=19 EndY=35 EndZ=0
    g4: LineSegment StartX=5.21097e-06 StartY=3 StartZ=0 EndX=5.21097e-06 EndY=0 EndZ=0
    g5: LineSegment StartX=3 StartY=0 StartZ=0 EndX=5.21097e-06 EndY=0 EndZ=0
    g6: LineSegment StartX=3 StartY=19 StartZ=0 EndX=3 EndY=0 EndZ=0
    g7: LineSegment StartX=19 StartY=38 StartZ=0 EndX=124 EndY=38 EndZ=0
    g8: Circle CenterX=119 CenterY=35 CenterZ=0 NormalX=0 NormalY=0 NormalZ=1 AngleXU=0 Radius=1
    g9: Circle CenterX=121 CenterY=35 CenterZ=0 NormalX=0 NormalY=0 NormalZ=1 AngleXU=0 Radius=1
    g10: Circle CenterX=121 CenterY=33 CenterZ=0 NormalX=0 NormalY=0 NormalZ=1 AngleXU=0 Radius=1
    g11: BSplineCurve PolesCount=3 KnotsCount=2 Degree=2 IsPeriodic=0
    g12: GeomPoint X=119 Y=35 Z=0
    g13: GeomPoint X=121 Y=33 Z=0
    g14: LineSegment StartX=119 StartY=35 StartZ=0 EndX=114 EndY=35 EndZ=0
    g15: ArcOfCircle CenterX=105 CenterY=19 CenterZ=0 NormalX=0 NormalY=0 NormalZ=1 AngleXU=0 Radius=19 StartAngle=5.7297 EndAngle=6.28319
    g16: ArcOfCircle CenterX=105 CenterY=19 CenterZ=0 NormalX=0 NormalY=0 NormalZ=1 AngleXU=0 Radius=16 StartAngle=5.60905 EndAngle=6.28319
    g17: LineSegment StartX=121 StartY=33 StartZ=0 EndX=121 EndY=19 EndZ=0
    g18: LineSegment StartX=124 StartY=38 StartZ=0 EndX=124 EndY=19 EndZ=0
    g19: LineSegment StartX=117.5 StartY=9.01251 StartZ=0 EndX=121.163 EndY=9.0125 EndZ=0
  constraints (46):
    c: Vertical(g0)
    c: Block(g0)
    c: Coincident(g1,g0)
    c: Block(g1)
    c: Coincident(g2,g1)
    c: Block(g2)
    c: Coincident(g3,g2)
    c: Horizontal(g3)
    c: Tangent(g3,g2)
    c: Coincident(g4,g0)
    c: Distance(g4) = 3
    c: Vertical(g4)
    c: Coincident(g5,g4)
    c: Horizontal(g5)
    c: Coincident(g6,g2)
    c: Coincident(g6,g5)
    c: Vertical(g6)
    c: Horizontal(g7)
    c: Distance(g7) = 105
    c: Coincident(g7,g1)
    c: Block(g3)
    c: Weight(g8) = 1
    c: Equal(g8,g9)
    c: Equal(g8,g10)
    c: InternalAlignment(g8,g11)
    c: InternalAlignment(g9,g11)
    c: InternalAlignment(g10,g11)
    c: InternalAlignment(g12,g11)
    c: InternalAlignment(g13,g11)
    c: Block(g11)
    c: Coincident(g14,g11)
    c: Coincident(g14,g3)
    c: Horizontal(g14)
    c: Block(g15)
    c: Coincident(g16,g15)
    c: Block(g16)
    c: Coincident(g17,g11)
    c: Coincident(g17,g16)
    c: Vertical(g17)
    c: Distance(g17) = 14
    c: Coincident(g18,g7)
    c: Coincident(g18,g15)
    c: Vertical(g18)
    c: Distance(g18) = 19
    c: Coincident(g19,g16)
    c: Coincident(g19,g15)
FEATURE [Part::Extrusion] Extrude049  label="top023"
  Base = -> Sketch058
  Dir = (0,0,1)
  DirMode = 2
  FaceMakerClass = Part::FaceMakerBullseye
  LengthFwd = 72
  LengthRev = 0
  Solid = true
  Symmetric = false
FEATURE [Sketcher::SketchObject] Sketch059
  FullyConstrained = true
  MapMode = 3
  Placement = pos=(0,0,0) rot=(1,0,0;1.5708rad)
  Support = -> [Extrude049]
  sketch-geometry (8):
    g0: Circle CenterX=80.351 CenterY=-67.6202 CenterZ=0 NormalX=0 NormalY=0 NormalZ=1 AngleXU=0 Radius=2
    g1: Circle CenterX=80.351 CenterY=-67.6202 CenterZ=0 NormalX=0 NormalY=0 NormalZ=1 AngleXU=0 Radius=3
    g2: Circle CenterX=80.351 CenterY=-4.92017 CenterZ=0 NormalX=0 NormalY=0 NormalZ=1 AngleXU=0 Radius=2
    g3: Circle CenterX=80.351 CenterY=-4.92017 CenterZ=0 NormalX=0 NormalY=0 NormalZ=1 AngleXU=0 Radius=3
    g4: Circle CenterX=23.851 CenterY=-4.92017 CenterZ=0 NormalX=0 NormalY=0 NormalZ=1 AngleXU=0 Radius=2
    g5: Circle CenterX=23.851 CenterY=-4.92017 CenterZ=0 NormalX=0 NormalY=0 NormalZ=1 AngleXU=0 Radius=3
    g6: Circle CenterX=23.851 CenterY=-67.6202 CenterZ=0 NormalX=0 NormalY=0 NormalZ=1 AngleXU=0 Radius=2
    g7: Circle CenterX=23.851 CenterY=-67.6202 CenterZ=0 NormalX=0 NormalY=0 NormalZ=1 AngleXU=0 Radius=3
  constraints (8):
    c: Block(g3)
    c: Block(g2)
    c: Block(g1)
    c: Block(g0)
    c: Block(g6)
    c: Block(g7)
    c: Block(g4)
    c: Block(g5)
FEATURE [Sketcher::SketchObject] Sketch060
  FullyConstrained = true
  MapMode = 3
  Placement = pos=(0,0,0) rot=(1,0,0;1.5708rad)
  Support = -> [Extrude049]
  sketch-geometry (8):
    g0: Circle CenterX=80.351 CenterY=-67.6202 CenterZ=0 NormalX=0 NormalY=0 NormalZ=1 AngleXU=0 Radius=3
    g1: Circle CenterX=80.351 CenterY=-4.92017 CenterZ=0 NormalX=0 NormalY=0 NormalZ=1 AngleXU=0 Radius=3
    g2: Circle CenterX=23.851 CenterY=-4.92017 CenterZ=0 NormalX=0 NormalY=0 NormalZ=1 AngleXU=0 Radius=3
    g3: Circle CenterX=23.851 CenterY=-67.6202 CenterZ=0 NormalX=0 NormalY=0 NormalZ=1 AngleXU=0 Radius=3
    g4: Circle CenterX=23.851 CenterY=-67.6202 CenterZ=0 NormalX=0 NormalY=0 NormalZ=1 AngleXU=0 Radius=5
    g5: Circle CenterX=80.351 CenterY=-67.6202 CenterZ=0 NormalX=0 NormalY=0 NormalZ=1 AngleXU=0 Radius=5
    g6: Circle CenterX=23.851 CenterY=-4.92017 CenterZ=0 NormalX=0 NormalY=0 NormalZ=1 AngleXU=0 Radius=5
    g7: Circle CenterX=80.351 CenterY=-4.92017 CenterZ=0 NormalX=0 NormalY=0 NormalZ=1 AngleXU=0 Radius=5
  constraints (8):
    c: Block(g1)
    c: Block(g0)
    c: Block(g3)
    c: Block(g2)
    c: Block(g5)
    c: Block(g4)
    c: Block(g6)
    c: Block(g7)
FEATURE [Sketcher::SketchObject] Sketch061
  FullyConstrained = true
  MapMode = 3
  Placement = pos=(0,0,0) rot=(1,0,0;1.5708rad)
  sketch-geometry (8):
    g0: Circle CenterX=80.351 CenterY=-67.6202 CenterZ=0 NormalX=0 NormalY=0 NormalZ=1 AngleXU=0 Radius=3
    g1: Circle CenterX=80.351 CenterY=-4.92017 CenterZ=0 NormalX=0 NormalY=0 NormalZ=1 AngleXU=0 Radius=3
    g2: Circle CenterX=23.851 CenterY=-4.92017 CenterZ=0 NormalX=0 NormalY=0 NormalZ=1 AngleXU=0 Radius=3
    g3: Circle CenterX=23.851 CenterY=-67.6202 CenterZ=0 NormalX=0 NormalY=0 NormalZ=1 AngleXU=0 Radius=3
    g4: Circle CenterX=23.851 CenterY=-67.6202 CenterZ=0 NormalX=0 NormalY=0 NormalZ=1 AngleXU=0 Radius=5
    g5: Circle CenterX=80.351 CenterY=-67.6202 CenterZ=0 NormalX=0 NormalY=0 NormalZ=1 AngleXU=0 Radius=5
    g6: Circle CenterX=23.851 CenterY=-4.92017 CenterZ=0 NormalX=0 NormalY=0 NormalZ=1 AngleXU=0 Radius=5
    g7: Circle CenterX=80.351 CenterY=-4.92017 CenterZ=0 NormalX=0 NormalY=0 NormalZ=1 AngleXU=0 Radius=5
  constraints (8):
    c: Block(g1)
    c: Block(g0)
    c: Block(g3)
    c: Block(g2)
    c: Block(g5)
    c: Block(g4)
    c: Block(g6)
    c: Block(g7)
FEATURE [Sketcher::SketchObject] Sketch062  label="topSketch016"
  FullyConstrained = true
  sketch-geometry (20):
    g0: LineSegment StartX=5.21097e-06 StartY=3 StartZ=0 EndX=5.21097e-06 EndY=19 EndZ=0
    g1: ArcOfCircle CenterX=19 CenterY=19 CenterZ=0 NormalX=0 NormalY=0 NormalZ=1 AngleXU=0 Radius=19 StartAngle=1.5708 EndAngle=3.14159
    g2: ArcOfCircle CenterX=19 CenterY=19 CenterZ=0 NormalX=0 NormalY=0 NormalZ=1 AngleXU=0 Radius=16 StartAngle=1.5708 EndAngle=3.14159
    g3: LineSegment StartX=114 StartY=35 StartZ=0 EndX=19 EndY=35 EndZ=0
    g4: LineSegment StartX=5.21097e-06 StartY=3 StartZ=0 EndX=5.21097e-06 EndY=0 EndZ=0
    g5: LineSegment StartX=3 StartY=0 StartZ=0 EndX=5.21097e-06 EndY=0 EndZ=0
    g6: LineSegment StartX=3 StartY=19 StartZ=0 EndX=3 EndY=0 EndZ=0
    g7: LineSegment StartX=19 StartY=38 StartZ=0 EndX=124 EndY=38 EndZ=0
    g8: Circle CenterX=119 CenterY=35 CenterZ=0 NormalX=0 NormalY=0 NormalZ=1 AngleXU=0 Radius=1
    g9: Circle CenterX=121 CenterY=35 CenterZ=0 NormalX=0 NormalY=0 NormalZ=1 AngleXU=0 Radius=1
    g10: Circle CenterX=121 CenterY=33 CenterZ=0 NormalX=0 NormalY=0 NormalZ=1 AngleXU=0 Radius=1
    g11: BSplineCurve PolesCount=3 KnotsCount=2 Degree=2 IsPeriodic=0
    g12: GeomPoint X=119 Y=35 Z=0
    g13: GeomPoint X=121 Y=33 Z=0
    g14: LineSegment StartX=119 StartY=35 StartZ=0 EndX=114 EndY=35 EndZ=0
    g15: ArcOfCircle CenterX=105 CenterY=19 CenterZ=0 NormalX=0 NormalY=0 NormalZ=1 AngleXU=0 Radius=19 StartAngle=5.7297 EndAngle=6.28319
    g16: ArcOfCircle CenterX=105 CenterY=19 CenterZ=0 NormalX=0 NormalY=0 NormalZ=1 AngleXU=0 Radius=16 StartAngle=5.60905 EndAngle=6.28319
    g17: LineSegment StartX=121 StartY=33 StartZ=0 EndX=121 EndY=19 EndZ=0
    g18: LineSegment StartX=124 StartY=38 StartZ=0 EndX=124 EndY=19 EndZ=0
    g19: LineSegment StartX=117.5 StartY=9.01251 StartZ=0 EndX=121.163 EndY=9.0125 EndZ=0
  constraints (46):
    c: Vertical(g0)
    c: Block(g0)
    c: Coincident(g1,g0)
    c: Block(g1)
    c: Coincident(g2,g1)
    c: Block(g2)
    c: Coincident(g3,g2)
    c: Horizontal(g3)
    c: Tangent(g3,g2)
    c: Coincident(g4,g0)
    c: Distance(g4) = 3
    c: Vertical(g4)
    c: Coincident(g5,g4)
    c: Horizontal(g5)
    c: Coincident(g6,g2)
    c: Coincident(g6,g5)
    c: Vertical(g6)
    c: Horizontal(g7)
    c: Distance(g7) = 105
    c: Coincident(g7,g1)
    c: Block(g3)
    c: Weight(g8) = 1
    c: Equal(g8,g9)
    c: Equal(g8,g10)
    c: InternalAlignment(g8,g11)
    c: InternalAlignment(g9,g11)
    c: InternalAlignment(g10,g11)
    c: InternalAlignment(g12,g11)
    c: InternalAlignment(g13,g11)
    c: Block(g11)
    c: Coincident(g14,g11)
    c: Coincident(g14,g3)
    c: Horizontal(g14)
    c: Block(g15)
    c: Coincident(g16,g15)
    c: Block(g16)
    c: Coincident(g17,g11)
    c: Coincident(g17,g16)
    c: Vertical(g17)
    c: Distance(g17) = 14
    c: Coincident(g18,g7)
    c: Coincident(g18,g15)
    c: Vertical(g18)
    c: Distance(g18) = 19
    c: Coincident(g19,g16)
    c: Coincident(g19,g15)
FEATURE [Part::Extrusion] Extrude053  label="top024"
  Base = -> Sketch062
  Dir = (0,0,1)
  DirMode = 2
  FaceMakerClass = Part::FaceMakerBullseye
  LengthFwd = 72
  LengthRev = 0
  Solid = true
  Symmetric = false
FEATURE [Sketcher::SketchObject] Sketch063
  FullyConstrained = true
  MapMode = 3
  Placement = pos=(0,0,0) rot=(1,0,0;1.5708rad)
  Support = -> [Extrude053]
  sketch-geometry (8):
    g0: Circle CenterX=80.351 CenterY=-67.6202 CenterZ=0 NormalX=0 NormalY=0 NormalZ=1 AngleXU=0 Radius=2
    g1: Circle CenterX=80.351 CenterY=-67.6202 CenterZ=0 NormalX=0 NormalY=0 NormalZ=1 AngleXU=0 Radius=3
    g2: Circle CenterX=80.351 CenterY=-4.92017 CenterZ=0 NormalX=0 NormalY=0 NormalZ=1 AngleXU=0 Radius=2
    g3: Circle CenterX=80.351 CenterY=-4.92017 CenterZ=0 NormalX=0 NormalY=0 NormalZ=1 AngleXU=0 Radius=3
    g4: Circle CenterX=23.851 CenterY=-4.92017 CenterZ=0 NormalX=0 NormalY=0 NormalZ=1 AngleXU=0 Radius=2
    g5: Circle CenterX=23.851 CenterY=-4.92017 CenterZ=0 NormalX=0 NormalY=0 NormalZ=1 AngleXU=0 Radius=3
    g6: Circle CenterX=23.851 CenterY=-67.6202 CenterZ=0 NormalX=0 NormalY=0 NormalZ=1 AngleXU=0 Radius=2
    g7: Circle CenterX=23.851 CenterY=-67.6202 CenterZ=0 NormalX=0 NormalY=0 NormalZ=1 AngleXU=0 Radius=3
  constraints (8):
    c: Block(g3)
    c: Block(g2)
    c: Block(g1)
    c: Block(g0)
    c: Block(g6)
    c: Block(g7)
    c: Block(g4)
    c: Block(g5)
FEATURE [Part::Extrusion] Extrude054
  Base = -> Sketch063
  Dir = (0,-1,2e-16)
  DirMode = 2
  FaceMakerClass = Part::FaceMakerBullseye
  LengthFwd = 6
  LengthRev = 0
  Placement = pos=(0,9,0) rot=(0,0,1;0rad)
  Solid = true
  Symmetric = false
FEATURE [Sketcher::SketchObject] Sketch064  label="topSketch017"
  FullyConstrained = true
  sketch-geometry (20):
    g0: LineSegment StartX=5.21097e-06 StartY=3 StartZ=0 EndX=5.21097e-06 EndY=19 EndZ=0
    g1: ArcOfCircle CenterX=19 CenterY=19 CenterZ=0 NormalX=0 NormalY=0 NormalZ=1 AngleXU=0 Radius=19 StartAngle=1.5708 EndAngle=3.14159
    g2: ArcOfCircle CenterX=19 CenterY=19 CenterZ=0 NormalX=0 NormalY=0 NormalZ=1 AngleXU=0 Radius=16 StartAngle=1.5708 EndAngle=3.14159
    g3: LineSegment StartX=114 StartY=35 StartZ=0 EndX=19 EndY=35 EndZ=0
    g4: LineSegment StartX=5.21097e-06 StartY=3 StartZ=0 EndX=5.21097e-06 EndY=0 EndZ=0
    g5: LineSegment StartX=3 StartY=0 StartZ=0 EndX=5.21097e-06 EndY=0 EndZ=0
    g6: LineSegment StartX=3 StartY=19 StartZ=0 EndX=3 EndY=0 EndZ=0
    g7: LineSegment StartX=19 StartY=38 StartZ=0 EndX=124 EndY=38 EndZ=0
    g8: Circle CenterX=119 CenterY=35 CenterZ=0 NormalX=0 NormalY=0 NormalZ=1 AngleXU=0 Radius=1
    g9: Circle CenterX=121 CenterY=35 CenterZ=0 NormalX=0 NormalY=0 NormalZ=1 AngleXU=0 Radius=1
    g10: Circle CenterX=121 CenterY=33 CenterZ=0 NormalX=0 NormalY=0 NormalZ=1 AngleXU=0 Radius=1
    g11: BSplineCurve PolesCount=3 KnotsCount=2 Degree=2 IsPeriodic=0
    g12: GeomPoint X=119 Y=35 Z=0
    g13: GeomPoint X=121 Y=33 Z=0
    g14: LineSegment StartX=119 StartY=35 StartZ=0 EndX=114 EndY=35 EndZ=0
    g15: ArcOfCircle CenterX=105 CenterY=19 CenterZ=0 NormalX=0 NormalY=0 NormalZ=1 AngleXU=0 Radius=19 StartAngle=5.7297 EndAngle=6.28319
    g16: ArcOfCircle CenterX=105 CenterY=19 CenterZ=0 NormalX=0 NormalY=0 NormalZ=1 AngleXU=0 Radius=16 StartAngle=5.60905 EndAngle=6.28319
    g17: LineSegment StartX=121 StartY=33 StartZ=0 EndX=121 EndY=19 EndZ=0
    g18: LineSegment StartX=124 StartY=38 StartZ=0 EndX=124 EndY=19 EndZ=0
    g19: LineSegment StartX=117.5 StartY=9.01251 StartZ=0 EndX=121.163 EndY=9.0125 EndZ=0
  constraints (46):
    c: Vertical(g0)
    c: Block(g0)
    c: Coincident(g1,g0)
    c: Block(g1)
    c: Coincident(g2,g1)
    c: Block(g2)
    c: Coincident(g3,g2)
    c: Horizontal(g3)
    c: Tangent(g3,g2)
    c: Coincident(g4,g0)
    c: Distance(g4) = 3
    c: Vertical(g4)
    c: Coincident(g5,g4)
    c: Horizontal(g5)
    c: Coincident(g6,g2)
    c: Coincident(g6,g5)
    c: Vertical(g6)
    c: Horizontal(g7)
    c: Distance(g7) = 105
    c: Coincident(g7,g1)
    c: Block(g3)
    c: Weight(g8) = 1
    c: Equal(g8,g9)
    c: Equal(g8,g10)
    c: InternalAlignment(g8,g11)
    c: InternalAlignment(g9,g11)
    c: InternalAlignment(g10,g11)
    c: InternalAlignment(g12,g11)
    c: InternalAlignment(g13,g11)
    c: Block(g11)
    c: Coincident(g14,g11)
    c: Coincident(g14,g3)
    c: Horizontal(g14)
    c: Block(g15)
    c: Coincident(g16,g15)
    c: Block(g16)
    c: Coincident(g17,g11)
    c: Coincident(g17,g16)
    c: Vertical(g17)
    c: Distance(g17) = 14
    c: Coincident(g18,g7)
    c: Coincident(g18,g15)
    c: Vertical(g18)
    c: Distance(g18) = 19
    c: Coincident(g19,g16)
    c: Coincident(g19,g15)
FEATURE [Sketcher::SketchObject] Sketch065
  FullyConstrained = true
  MapMode = 3
  Placement = pos=(0,0,0) rot=(1,0,0;1.5708rad)
  sketch-geometry (8):
    g0: Circle CenterX=80.351 CenterY=-67.6202 CenterZ=0 NormalX=0 NormalY=0 NormalZ=1 AngleXU=0 Radius=3
    g1: Circle CenterX=80.351 CenterY=-4.92017 CenterZ=0 NormalX=0 NormalY=0 NormalZ=1 AngleXU=0 Radius=3
    g2: Circle CenterX=23.851 CenterY=-4.92017 CenterZ=0 NormalX=0 NormalY=0 NormalZ=1 AngleXU=0 Radius=3
    g3: Circle CenterX=23.851 CenterY=-67.6202 CenterZ=0 NormalX=0 NormalY=0 NormalZ=1 AngleXU=0 Radius=3
    g4: Circle CenterX=23.851 CenterY=-67.6202 CenterZ=0 NormalX=0 NormalY=0 NormalZ=1 AngleXU=0 Radius=5
    g5: Circle CenterX=80.351 CenterY=-67.6202 CenterZ=0 NormalX=0 NormalY=0 NormalZ=1 AngleXU=0 Radius=5
    g6: Circle CenterX=23.851 CenterY=-4.92017 CenterZ=0 NormalX=0 NormalY=0 NormalZ=1 AngleXU=0 Radius=5
    g7: Circle CenterX=80.351 CenterY=-4.92017 CenterZ=0 NormalX=0 NormalY=0 NormalZ=1 AngleXU=0 Radius=5
  constraints (8):
    c: Block(g1)
    c: Block(g0)
    c: Block(g3)
    c: Block(g2)
    c: Block(g5)
    c: Block(g4)
    c: Block(g6)
    c: Block(g7)
FEATURE [Part::Extrusion] Extrude056
  Base = -> Sketch065
  Dir = (0,-1,2e-16)
  DirMode = 2
  FaceMakerClass = Part::FaceMakerBullseye
  LengthFwd = 2
  LengthRev = 0
  Solid = true
  Symmetric = false
FEATURE [Part::Extrusion] Extrude057  label="top025"
  Base = -> Sketch064
  Dir = (0,0,1)
  DirMode = 2
  FaceMakerClass = Part::FaceMakerBullseye
  LengthFwd = 72
  LengthRev = 0
  Solid = true
  Symmetric = false
FEATURE [Sketcher::SketchObject] Sketch066
  FullyConstrained = true
  MapMode = 3
  Placement = pos=(0,0,0) rot=(1,0,0;1.5708rad)
  Support = -> [Extrude057]
  sketch-geometry (8):
    g0: Circle CenterX=80.351 CenterY=-67.6202 CenterZ=0 NormalX=0 NormalY=0 NormalZ=1 AngleXU=0 Radius=3
    g1: Circle CenterX=80.351 CenterY=-4.92017 CenterZ=0 NormalX=0 NormalY=0 NormalZ=1 AngleXU=0 Radius=3
    g2: Circle CenterX=23.851 CenterY=-4.92017 CenterZ=0 NormalX=0 NormalY=0 NormalZ=1 AngleXU=0 Radius=3
    g3: Circle CenterX=23.851 CenterY=-67.6202 CenterZ=0 NormalX=0 NormalY=0 NormalZ=1 AngleXU=0 Radius=3
    g4: Circle CenterX=23.851 CenterY=-67.6202 CenterZ=0 NormalX=0 NormalY=0 NormalZ=1 AngleXU=0 Radius=5
    g5: Circle CenterX=80.351 CenterY=-67.6202 CenterZ=0 NormalX=0 NormalY=0 NormalZ=1 AngleXU=0 Radius=5
    g6: Circle CenterX=23.851 CenterY=-4.92017 CenterZ=0 NormalX=0 NormalY=0 NormalZ=1 AngleXU=0 Radius=5
    g7: Circle CenterX=80.351 CenterY=-4.92017 CenterZ=0 NormalX=0 NormalY=0 NormalZ=1 AngleXU=0 Radius=5
  constraints (8):
    c: Block(g1)
    c: Block(g0)
    c: Block(g3)
    c: Block(g2)
    c: Block(g5)
    c: Block(g4)
    c: Block(g6)
    c: Block(g7)
FEATURE [Part::Extrusion] Extrude055
  Base = -> Sketch066
  Dir = (0,-1,2e-16)
  DirMode = 2
  FaceMakerClass = Part::FaceMakerBullseye
  LengthFwd = 2
  LengthRev = 0
  Solid = true
  Symmetric = false
FEATURE [Part::Fillet] Fillet041
  Base = -> Extrude056
  Edges = 4 edges r=1.99: [Edge6,Edge12,Edge18,Edge24]
FEATURE [Part::Cut] Cut045
  Base = -> Extrude055
  Placement = pos=(0,6,0) rot=(0,0,1;0rad)
  Tool = -> Fillet041
FEATURE [Part::MultiFuse] Fusion095  label="pcbScrewPillars"
  Placement = pos=(-3.2,-1,72.3) rot=(0,0,1;0rad)
  Shapes = -> [Cut045,Extrude054]
FEATURE [Part::Feature] Face113
  shape: bbox 3.2 x 1.5 x 2e-07 mm, 1 faces, 0 solids (baked)
FEATURE [Part::Revolution] Revolve121  label="backCaseScrewRetainer002"
  Angle = 360
  Axis = (0,1,0)
  Base = (0,0,0)
  FaceMakerClass = Part::FaceMakerBullseye
  Placement = pos=(12.5,3,62) rot=(0,0,1;0rad)
  Solid = false
  Source = -> Face113
  Symmetric = false
FEATURE [Part::Feature] Face114
  shape: bbox 3.2 x 1.5 x 2e-07 mm, 1 faces, 0 solids (baked)
FEATURE [Part::Feature] Face115
  shape: bbox 3.2 x 1.5 x 2e-07 mm, 1 faces, 0 solids (baked)
FEATURE [Part::Feature] Face116
  shape: bbox 3.2 x 1.5 x 2e-07 mm, 1 faces, 0 solids (baked)
FEATURE [Part::Revolution] Revolve122  label="frontCaseScrewRetainer004"
  Angle = 360
  Axis = (0,1,0)
  Base = (0,0,0)
  FaceMakerClass = Part::FaceMakerBullseye
  Placement = pos=(89.5,3,68.5) rot=(0,0,1;0rad)
  Solid = false
  Source = -> Face115
  Symmetric = false
FEATURE [Part::Revolution] Revolve123  label="frontCaseScrewRetainer005"
  Angle = 360
  Axis = (0,1,0)
  Base = (0,0,0)
  FaceMakerClass = Part::FaceMakerBullseye
  Placement = pos=(89.5,3,3.5) rot=(0,0,1;0rad)
  Solid = false
  Source = -> Face116
  Symmetric = false
FEATURE [Part::Revolution] Revolve124  label="backCaseScrewRetainer003"
  Angle = 360
  Axis = (0,1,0)
  Base = (0,0,0)
  FaceMakerClass = Part::FaceMakerBullseye
  Placement = pos=(12.5,3,10) rot=(0,0,1;0rad)
  Solid = false
  Source = -> Face114
  Symmetric = false
FEATURE [Part::Feature] Face117
  shape: bbox 3.6 x 3.2 x 2e-07 mm, 1 faces, 0 solids (baked)
FEATURE [Part::Revolution] Revolve125  label="moreFrontCaseScrewRetainer004"
  Angle = 360
  Axis = (0,1,0)
  Base = (0,0,0)
  FaceMakerClass = Part::FaceMakerBullseye
  Placement = pos=(109.5,4.5,68.5) rot=(0,0,1;0rad)
  Solid = false
  Source = -> Face117
  Symmetric = false
FEATURE [Part::Feature] Face118
  shape: bbox 3.6 x 3.2 x 2e-07 mm, 1 faces, 0 solids (baked)
FEATURE [Part::Revolution] Revolve126  label="moreFrontCaseScrewRetainer005"
  Angle = 360
  Axis = (0,1,0)
  Base = (0,0,0)
  FaceMakerClass = Part::FaceMakerBullseye
  Placement = pos=(109.5,4.5,3.5) rot=(0,0,1;0rad)
  Solid = false
  Source = -> Face118
  Symmetric = false
FEATURE [Part::MultiFuse] Fusion096  label="screwRetainers001"
  Shapes = -> [Revolve126,Revolve125,Revolve124,Revolve123,Revolve122,Revolve121]
FEATURE [Part::Feature] Face119
  shape: bbox 10 x 16.5 x 2e-07 mm, 1 faces, 0 solids (baked)
FEATURE [Part::Revolution] Revolve130  label="plugHousing050"
  Angle = 360
  Axis = (0,1,0)
  Base = (0,0,0)
  FaceMakerClass = Part::FaceMakerBullseye
  Placement = pos=(0,0,36.15) rot=(0,0,1;0rad)
  Solid = false
  Source = -> Face119
  Symmetric = false
FEATURE [Part::Feature] Face120
  shape: bbox 10 x 16.5 x 2e-07 mm, 1 faces, 0 solids (baked)
FEATURE [Part::Feature] Face121
  shape: bbox 10 x 16.5 x 2e-07 mm, 1 faces, 0 solids (baked)
FEATURE [Part::Revolution] Revolve127  label="plugHousing047"
  Angle = 360
  Axis = (0,1,0)
  Base = (0,0,0)
  FaceMakerClass = Part::FaceMakerBullseye
  Placement = pos=(0,0,36.15) rot=(0,0,1;0rad)
  Solid = false
  Source = -> Face121
  Symmetric = false
FEATURE [Part::Feature] Face122
  shape: bbox 10 x 16.5 x 2e-07 mm, 1 faces, 0 solids (baked)
FEATURE [Part::Feature] Face123
  shape: bbox 10 x 16.5 x 2e-07 mm, 1 faces, 0 solids (baked)
FEATURE [Part::Revolution] Revolve128  label="plugHousing048"
  Angle = 360
  Axis = (0,1,0)
  Base = (0,0,0)
  FaceMakerClass = Part::FaceMakerBullseye
  Placement = pos=(0,0,36.15) rot=(0,0,1;0rad)
  Solid = false
  Source = -> Face123
  Symmetric = false
FEATURE [Part::MultiFuse] Fusion100  label="plugHousing054"
  Placement = pos=(0,0,0) rot=(0,0,1;1.5708rad)
  Shapes = -> [Revolve130,Revolve128]
FEATURE [Part::Feature] Face124
  shape: bbox 10 x 16.5 x 2e-07 mm, 1 faces, 0 solids (baked)
FEATURE [Part::Feature] Face125
  shape: bbox 10 x 16.5 x 2e-07 mm, 1 faces, 0 solids (baked)
FEATURE [Part::Revolution] Revolve129  label="plugHousing049"
  Angle = 360
  Axis = (0,1,0)
  Base = (0,0,0)
  FaceMakerClass = Part::FaceMakerBullseye
  Placement = pos=(0,0,36.15) rot=(0,0,1;0rad)
  Solid = false
  Source = -> Face125
  Symmetric = false
FEATURE [Part::Feature] Face126
  shape: bbox 10 x 16.5 x 2e-07 mm, 1 faces, 0 solids (baked)
FEATURE [Part::Revolution] Revolve131  label="plugHousing058"
  Angle = 360
  Axis = (0,1,0)
  Base = (0,0,0)
  FaceMakerClass = Part::FaceMakerBullseye
  Placement = pos=(0,0,36.15) rot=(0,0,1;0rad)
  Solid = false
  Source = -> Face120
  Symmetric = false
FEATURE [Part::MultiFuse] Fusion099  label="plugHousing053"
  Placement = pos=(0,0,0) rot=(0,0,1;1.5708rad)
  Shapes = -> [Revolve127,Revolve131]
FEATURE [Part::MultiFuse] Fusion102  label="plugHousing056"
  Placement = pos=(0,19,0) rot=(0,0,1;3.14159rad)
  Shapes = -> [Fusion100,Fusion099]
FEATURE [Part::Revolution] Revolve132  label="plugHousing059"
  Angle = 360
  Axis = (0,1,0)
  Base = (0,0,0)
  FaceMakerClass = Part::FaceMakerBullseye
  Placement = pos=(0,0,36.15) rot=(0,0,1;0rad)
  Solid = false
  Source = -> Face126
  Symmetric = false
FEATURE [Part::Revolution] Revolve133  label="plugHousing060"
  Angle = 360
  Axis = (0,1,0)
  Base = (0,0,0)
  FaceMakerClass = Part::FaceMakerBullseye
  Placement = pos=(0,0,36.15) rot=(0,0,1;0rad)
  Solid = false
  Source = -> Face122
  Symmetric = false
FEATURE [Part::MultiFuse] Fusion097  label="plugHousing051"
  Placement = pos=(0,0,0) rot=(0,0,1;1.5708rad)
  Shapes = -> [Revolve133,Revolve132]
FEATURE [Part::Revolution] Revolve134  label="plugHousing061"
  Angle = 360
  Axis = (0,1,0)
  Base = (0,0,0)
  FaceMakerClass = Part::FaceMakerBullseye
  Placement = pos=(0,0,36.15) rot=(0,0,1;0rad)
  Solid = false
  Source = -> Face124
  Symmetric = false
FEATURE [Part::MultiFuse] Fusion101  label="plugHousing055"
  Placement = pos=(0,0,0) rot=(0,0,1;1.5708rad)
  Shapes = -> [Revolve129,Revolve134]
FEATURE [Part::MultiFuse] Fusion098  label="plugHousing052"
  Placement = pos=(0,19,0) rot=(0,0,1;3.14159rad)
  Shapes = -> [Fusion097,Fusion101]
FEATURE [Part::MultiFuse] Fusion103  label="plugHousing057"
  Placement = pos=(122.621,0,-0.15) rot=(0,0,1;0rad)
  Shapes = -> [Fusion102,Fusion098]
FEATURE [Part::Box] Box028  label="Cube015"
  AttacherType = Attacher::AttachEngine3D
  Height = 28
  Length = 3
  Placement = pos=(110.7,19,22) rot=(0,0,1;0rad)
  Width = 15.7
FEATURE [Part::Cylinder] Cylinder044
  Angle = 360
  AttacherType = Attacher::AttachEngine3D
  Height = 20
  Placement = pos=(0,0,36.15) rot=(0,0,1;0rad)
  Radius = 10.3
FEATURE [Part::Cylinder] Cylinder045
  Angle = 360
  AttacherType = Attacher::AttachEngine3D
  Height = 10
  Placement = pos=(0,0,36.15) rot=(0,0,1;0rad)
  Radius = 4
FEATURE [Part::MultiFuse] Fusion104  label="removeToCreteHoleForPlugHousing040"
  Placement = pos=(70,19,36) rot=(0,1,0;1.5708rad)
  Shapes = -> [Cylinder044,Cylinder045]
FEATURE [Part::Cut] Cut046  label="plugHousingTab003"
  Base = -> Box028
  Tool = -> Fusion104
FEATURE [Part::MultiFuse] Fusion105  label="plugHousing062"
  Shapes = -> [Fusion103,Cut046]
FEATURE [Part::Fillet] Fillet042
  Base = -> Fusion105
  Edges = 1 edges r=2: [Edge25]
FEATURE [Part::Fillet] Fillet043  label="plugHousing063"
  Base = -> Fillet042
  Edges = 1 edges r=2: [Edge8]
  Placement = pos=(7,0,0) rot=(0,0,1;0rad)
FEATURE [Part::Feature] Face127
  shape: bbox 10 x 16.5 x 2e-07 mm, 1 faces, 0 solids (baked)
FEATURE [Part::Feature] Face128
  shape: bbox 10 x 16.5 x 2e-07 mm, 1 faces, 0 solids (baked)
FEATURE [Part::Revolution] Revolve137  label="plugHousing070"
  Angle = 360
  Axis = (0,1,0)
  Base = (0,0,0)
  FaceMakerClass = Part::FaceMakerBullseye
  Placement = pos=(0,0,36.15) rot=(0,0,1;0rad)
  Solid = false
  Source = -> Face127
  Symmetric = false
FEATURE [Part::Revolution] Revolve140  label="plugHousing073"
  Angle = 360
  Axis = (0,1,0)
  Base = (0,0,0)
  FaceMakerClass = Part::FaceMakerBullseye
  Placement = pos=(0,0,36.15) rot=(0,0,1;0rad)
  Solid = false
  Source = -> Face128
  Symmetric = false
FEATURE [Part::Feature] Face129
  shape: bbox 10 x 16.5 x 2e-07 mm, 1 faces, 0 solids (baked)
FEATURE [Part::Revolution] Revolve138  label="plugHousing071"
  Angle = 360
  Axis = (0,1,0)
  Base = (0,0,0)
  FaceMakerClass = Part::FaceMakerBullseye
  Placement = pos=(0,0,36.15) rot=(0,0,1;0rad)
  Solid = false
  Source = -> Face129
  Symmetric = false
FEATURE [Part::Feature] Face130
  shape: bbox 10 x 16.5 x 2e-07 mm, 1 faces, 0 solids (baked)
FEATURE [Part::Revolution] Revolve139  label="plugHousing072"
  Angle = 360
  Axis = (0,1,0)
  Base = (0,0,0)
  FaceMakerClass = Part::FaceMakerBullseye
  Placement = pos=(0,0,36.15) rot=(0,0,1;0rad)
  Solid = false
  Source = -> Face130
  Symmetric = false
FEATURE [Part::Feature] Face131
  shape: bbox 10 x 16.5 x 2e-07 mm, 1 faces, 0 solids (baked)
FEATURE [Part::Revolution] Revolve135  label="plugHousing068"
  Angle = 360
  Axis = (0,1,0)
  Base = (0,0,0)
  FaceMakerClass = Part::FaceMakerBullseye
  Placement = pos=(0,0,36.15) rot=(0,0,1;0rad)
  Solid = false
  Source = -> Face131
  Symmetric = false
FEATURE [Part::MultiFuse] Fusion112  label="plugHousing078"
  Placement = pos=(0,0,0) rot=(0,0,1;1.5708rad)
  Shapes = -> [Revolve135,Revolve139]
FEATURE [Part::Feature] Face132
  shape: bbox 10 x 16.5 x 2e-07 mm, 1 faces, 0 solids (baked)
FEATURE [Part::Revolution] Revolve141  label="plugHousing074"
  Angle = 360
  Axis = (0,1,0)
  Base = (0,0,0)
  FaceMakerClass = Part::FaceMakerBullseye
  Placement = pos=(0,0,36.15) rot=(0,0,1;0rad)
  Solid = false
  Source = -> Face132
  Symmetric = false
FEATURE [Part::MultiFuse] Fusion110  label="plugHousing076"
  Placement = pos=(0,0,0) rot=(0,0,1;1.5708rad)
  Shapes = -> [Revolve141,Revolve140]
FEATURE [Part::Feature] Face133
  shape: bbox 10 x 16.5 x 2e-07 mm, 1 faces, 0 solids (baked)
FEATURE [Part::Revolution] Revolve136  label="plugHousing069"
  Angle = 360
  Axis = (0,1,0)
  Base = (0,0,0)
  FaceMakerClass = Part::FaceMakerBullseye
  Placement = pos=(0,0,36.15) rot=(0,0,1;0rad)
  Solid = false
  Source = -> Face133
  Symmetric = false
FEATURE [Part::MultiFuse] Fusion106  label="plugHousing064"
  Placement = pos=(0,0,0) rot=(0,0,1;1.5708rad)
  Shapes = -> [Revolve138,Revolve136]
FEATURE [Part::MultiFuse] Fusion108  label="plugHousing066"
  Placement = pos=(0,19,0) rot=(0,0,1;3.14159rad)
  Shapes = -> [Fusion106,Fusion112]
FEATURE [Part::Feature] Face134
  shape: bbox 10 x 16.5 x 2e-07 mm, 1 faces, 0 solids (baked)
FEATURE [Part::Revolution] Revolve142  label="plugHousing075"
  Angle = 360
  Axis = (0,1,0)
  Base = (0,0,0)
  FaceMakerClass = Part::FaceMakerBullseye
  Placement = pos=(0,0,36.15) rot=(0,0,1;0rad)
  Solid = false
  Source = -> Face134
  Symmetric = false
FEATURE [Part::MultiFuse] Fusion107  label="plugHousing065"
  Placement = pos=(0,0,0) rot=(0,0,1;1.5708rad)
  Shapes = -> [Revolve137,Revolve142]
FEATURE [Part::MultiFuse] Fusion111  label="plugHousing077"
  Placement = pos=(0,19,0) rot=(0,0,1;3.14159rad)
  Shapes = -> [Fusion110,Fusion107]
FEATURE [Part::MultiFuse] Fusion109  label="plugHousing067"
  Placement = pos=(131.236,0,-0.15) rot=(0,0,1;0rad)
  Shapes = -> [Fusion108,Fusion111]
FEATURE [Part::MultiFuse] Fusion113  label="plugHousing079"
  Shapes = -> [Fillet043,Fusion109]
FEATURE [Part::Feature] Face135
  shape: bbox 3.5 x 17.8 x 2e-07 mm, 1 faces, 0 solids (baked)
FEATURE [Part::Revolution] Revolve143  label="removeToCreateScrewAndThreadedInsertHole049"
  Angle = 360
  Axis = (0,1,0)
  Base = (0,0,0)
  FaceMakerClass = Part::FaceMakerBullseye
  Placement = pos=(12.5,0,10) rot=(0,0,1;0rad)
  Solid = false
  Source = -> Face135
  Symmetric = false
FEATURE [Part::Feature] Face136
  shape: bbox 3.5 x 17.8 x 2e-07 mm, 1 faces, 0 solids (baked)
FEATURE [Part::Revolution] Revolve144  label="removeToCreateScrewAndThreadedInsertHole050"
  Angle = 360
  Axis = (0,1,0)
  Base = (0,0,0)
  FaceMakerClass = Part::FaceMakerBullseye
  Placement = pos=(12.5,0,62) rot=(0,0,1;0rad)
  Solid = false
  Source = -> Face136
  Symmetric = false
FEATURE [Part::Feature] Face137
  shape: bbox 3.5 x 17.8 x 2e-07 mm, 1 faces, 0 solids (baked)
FEATURE [Part::Revolution] Revolve145  label="removeToCreateScrewAndThreadedInsertHole051"
  Angle = 360
  Axis = (0,1,0)
  Base = (0,0,0)
  FaceMakerClass = Part::FaceMakerBullseye
  Placement = pos=(89.5,0,68.5) rot=(0,0,1;0rad)
  Solid = false
  Source = -> Face137
  Symmetric = false
FEATURE [Part::Feature] Face138
  shape: bbox 3.5 x 17.8 x 2e-07 mm, 1 faces, 0 solids (baked)
FEATURE [Part::Revolution] Revolve146  label="removeToCreateScrewAndThreadedInsertHole052"
  Angle = 360
  Axis = (0,1,0)
  Base = (0,0,0)
  FaceMakerClass = Part::FaceMakerBullseye
  Placement = pos=(89.5,0,3.5) rot=(0,0,1;0rad)
  Solid = false
  Source = -> Face138
  Symmetric = false
FEATURE [Part::Feature] Face139
  shape: bbox 3.5 x 17.8 x 2e-07 mm, 1 faces, 0 solids (baked)
FEATURE [Part::Revolution] Revolve147  label="removeToCreateScrewAndThreadedInsertHole053"
  Angle = 360
  Axis = (0,1,0)
  Base = (0,0,0)
  FaceMakerClass = Part::FaceMakerBullseye
  Placement = pos=(109.5,4.7,3.5) rot=(0,0,1;0rad)
  Solid = false
  Source = -> Face139
  Symmetric = false
FEATURE [Part::Feature] Face140
  shape: bbox 3.5 x 17.8 x 2e-07 mm, 1 faces, 0 solids (baked)
FEATURE [Part::Revolution] Revolve148  label="removeToCreateScrewAndThreadedInsertHole054"
  Angle = 360
  Axis = (0,1,0)
  Base = (0,0,0)
  FaceMakerClass = Part::FaceMakerBullseye
  Placement = pos=(109.5,4.7,68.5) rot=(0,0,1;0rad)
  Solid = false
  Source = -> Face140
  Symmetric = false
FEATURE [Part::MultiFuse] Fusion114  label="removeToCreateScrewAndThreadedInsertHole055"
  Shapes = -> [Revolve148,Revolve147,Revolve146,Revolve145,Revolve144,Revolve143]
FEATURE [Part::Cut] Cut047  label="casePillars004"
  Base = -> Cut037
  Tool = -> Fusion114
FEATURE [Part::Feature] Face141
  shape: bbox 3.5 x 17.8 x 2e-07 mm, 1 faces, 0 solids (baked)
FEATURE [Part::Feature] Face142
  shape: bbox 3.5 x 17.8 x 2e-07 mm, 1 faces, 0 solids (baked)
FEATURE [Part::Feature] Face143
  shape: bbox 3.5 x 17.8 x 2e-07 mm, 1 faces, 0 solids (baked)
FEATURE [Part::Revolution] Revolve149  label="removeToCreateScrewAndThreadedInsertHole057"
  Angle = 360
  Axis = (0,1,0)
  Base = (0,0,0)
  FaceMakerClass = Part::FaceMakerBullseye
  Placement = pos=(12.5,0,10) rot=(0,0,1;0rad)
  Solid = false
  Source = -> Face141
  Symmetric = false
FEATURE [Part::Feature] Face144
  shape: bbox 3.5 x 17.8 x 2e-07 mm, 1 faces, 0 solids (baked)
FEATURE [Part::Feature] Face145
  shape: bbox 3.5 x 17.8 x 2e-07 mm, 1 faces, 0 solids (baked)
FEATURE [Part::Feature] Face146
  shape: bbox 3.5 x 17.8 x 2e-07 mm, 1 faces, 0 solids (baked)
FEATURE [Part::Revolution] Revolve150  label="removeToCreateScrewAndThreadedInsertHole058"
  Angle = 360
  Axis = (0,1,0)
  Base = (0,0,0)
  FaceMakerClass = Part::FaceMakerBullseye
  Placement = pos=(12.5,0,62) rot=(0,0,1;0rad)
  Solid = false
  Source = -> Face146
  Symmetric = false
FEATURE [Part::Revolution] Revolve151  label="removeToCreateScrewAndThreadedInsertHole059"
  Angle = 360
  Axis = (0,1,0)
  Base = (0,0,0)
  FaceMakerClass = Part::FaceMakerBullseye
  Placement = pos=(89.5,0,68.5) rot=(0,0,1;0rad)
  Solid = false
  Source = -> Face143
  Symmetric = false
FEATURE [Part::Revolution] Revolve152  label="removeToCreateScrewAndThreadedInsertHole060"
  Angle = 360
  Axis = (0,1,0)
  Base = (0,0,0)
  FaceMakerClass = Part::FaceMakerBullseye
  Placement = pos=(89.5,0,3.5) rot=(0,0,1;0rad)
  Solid = false
  Source = -> Face142
  Symmetric = false
FEATURE [Part::Revolution] Revolve153  label="removeToCreateScrewAndThreadedInsertHole061"
  Angle = 360
  Axis = (0,1,0)
  Base = (0,0,0)
  FaceMakerClass = Part::FaceMakerBullseye
  Placement = pos=(109.5,4.7,3.5) rot=(0,0,1;0rad)
  Solid = false
  Source = -> Face145
  Symmetric = false
FEATURE [Part::Revolution] Revolve154  label="removeToCreateScrewAndThreadedInsertHole062"
  Angle = 360
  Axis = (0,1,0)
  Base = (0,0,0)
  FaceMakerClass = Part::FaceMakerBullseye
  Placement = pos=(109.5,4.7,68.5) rot=(0,0,1;0rad)
  Solid = false
  Source = -> Face144
  Symmetric = false
FEATURE [Part::MultiFuse] Fusion115  label="removeToCreateScrewAndThreadedInsertHole056"
  Shapes = -> [Revolve154,Revolve153,Revolve152,Revolve151,Revolve150,Revolve149]
FEATURE [Part::Cut] Cut048  label="bottom013"
  Base = -> Fusion093
  Tool = -> Fusion115
